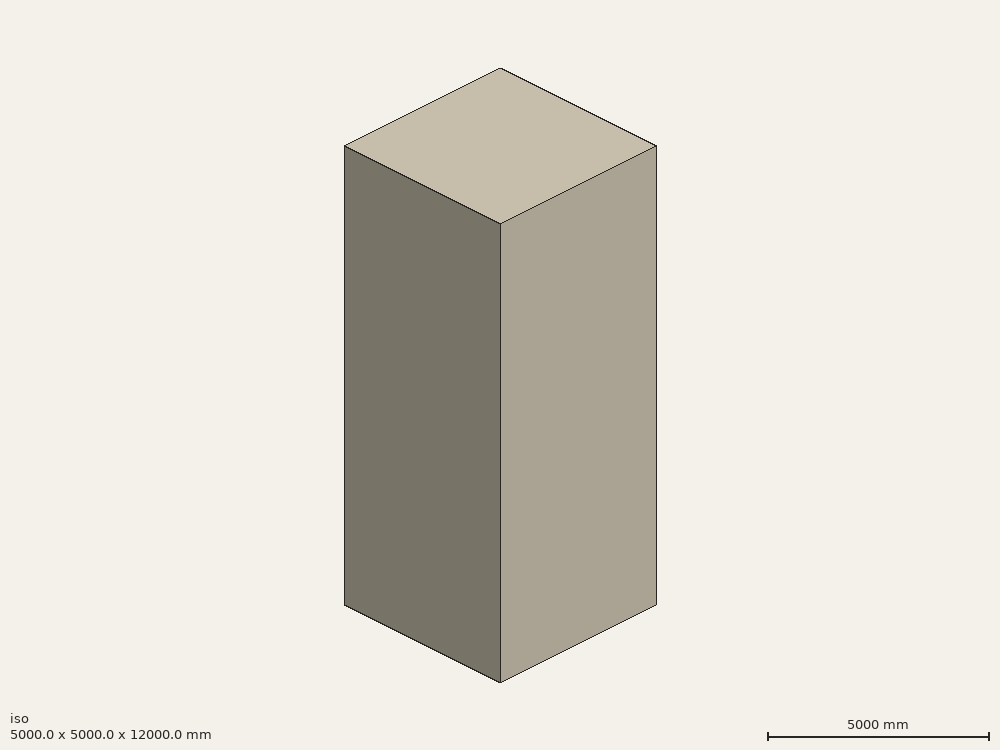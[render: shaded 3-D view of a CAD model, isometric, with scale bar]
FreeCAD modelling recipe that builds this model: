
FCSTD DOCUMENT  (FreeCAD 1.0R39109 (Git))
Label: revolveTester-6
License: All rights reserved
LicenseURL: http://en.wikipedia.org/wiki/All_rights_reserved
objects: App::DocumentObjectGroupPython×1248, App::Part×2, Part::FeaturePython×1, Sketcher::SketchObject×1, Part::Revolution×1, Part::Cylinder×1, Part::Cut×1
note: 6 computed .brp shape members not serialized (recipe doc carries the construction recipe); baked Part::Feature solids carry a one-line shape summary decoded from their .brp

FEATURE [App::DocumentObjectGroupPython] HALFPI  # scripted group (container) (typed FeaturePython)
  name = HALFPI
  value = pi/2.
FEATURE [App::DocumentObjectGroupPython] PI  # scripted group (container) (typed FeaturePython)
  name = PI
  value = 1.*pi
FEATURE [App::DocumentObjectGroupPython] TWOPI  # scripted group (container) (typed FeaturePython)
  name = TWOPI
  value = 2.*pi
FEATURE [App::DocumentObjectGroupPython] Constants  # scripted group (container) (typed FeaturePython)
  Group = -> [HALFPI,PI,TWOPI]
FEATURE [App::DocumentObjectGroupPython] Variables  # scripted group (container) (typed FeaturePython)
FEATURE [App::DocumentObjectGroupPython] Quantities  # scripted group (container) (typed FeaturePython)
FEATURE [App::DocumentObjectGroupPython] Isotopes  # scripted group (container) (typed FeaturePython)
FEATURE [App::DocumentObjectGroupPython] Elements  # scripted group (container) (typed FeaturePython)
FEATURE [App::DocumentObjectGroupPython] G4Isotopes  # scripted group (container) (typed FeaturePython)
FEATURE [App::DocumentObjectGroupPython] H_element  # scripted group (container) (typed FeaturePython)
  Z = 1
  atom_value = 1.008
  formula = H
  name = H_element
FEATURE [App::DocumentObjectGroupPython] He_element  # scripted group (container) (typed FeaturePython)
  Z = 2
  atom_value = 4.0026
  formula = He
  name = He_element
FEATURE [App::DocumentObjectGroupPython] Li_element  # scripted group (container) (typed FeaturePython)
  Z = 3
  atom_value = 6.94
  formula = Li
  name = Li_element
FEATURE [App::DocumentObjectGroupPython] Be_element  # scripted group (container) (typed FeaturePython)
  Z = 4
  atom_value = 9.01218
  formula = Be
  name = Be_element
FEATURE [App::DocumentObjectGroupPython] B_element  # scripted group (container) (typed FeaturePython)
  Z = 5
  atom_value = 10.81
  formula = B
  name = B_element
FEATURE [App::DocumentObjectGroupPython] C_element  # scripted group (container) (typed FeaturePython)
  Z = 6
  atom_value = 12.011
  formula = C
  name = C_element
FEATURE [App::DocumentObjectGroupPython] N_element  # scripted group (container) (typed FeaturePython)
  Z = 7
  atom_value = 14.007
  formula = N
  name = N_element
FEATURE [App::DocumentObjectGroupPython] O_element  # scripted group (container) (typed FeaturePython)
  Z = 8
  atom_value = 15.999
  formula = O
  name = O_element
FEATURE [App::DocumentObjectGroupPython] F_element  # scripted group (container) (typed FeaturePython)
  Z = 9
  atom_value = 18.9984
  formula = F
  name = F_element
FEATURE [App::DocumentObjectGroupPython] Ne_element  # scripted group (container) (typed FeaturePython)
  Z = 10
  atom_value = 20.1797
  formula = Ne
  name = Ne_element
FEATURE [App::DocumentObjectGroupPython] Na_element  # scripted group (container) (typed FeaturePython)
  Z = 11
  atom_value = 22.9898
  formula = Na
  name = Na_element
FEATURE [App::DocumentObjectGroupPython] Mg_element  # scripted group (container) (typed FeaturePython)
  Z = 12
  atom_value = 24.305
  formula = Mg
  name = Mg_element
FEATURE [App::DocumentObjectGroupPython] Al_element  # scripted group (container) (typed FeaturePython)
  Z = 13
  atom_value = 26.9815
  formula = Al
  name = Al_element
FEATURE [App::DocumentObjectGroupPython] Si_element  # scripted group (container) (typed FeaturePython)
  Z = 14
  atom_value = 28.085
  formula = Si
  name = Si_element
FEATURE [App::DocumentObjectGroupPython] P_element  # scripted group (container) (typed FeaturePython)
  Z = 15
  atom_value = 30.9738
  formula = P
  name = P_element
FEATURE [App::DocumentObjectGroupPython] S_element  # scripted group (container) (typed FeaturePython)
  Z = 16
  atom_value = 32.06
  formula = S
  name = S_element
FEATURE [App::DocumentObjectGroupPython] Cl_element  # scripted group (container) (typed FeaturePython)
  Z = 17
  atom_value = 35.45
  formula = Cl
  name = Cl_element
FEATURE [App::DocumentObjectGroupPython] Ar_element  # scripted group (container) (typed FeaturePython)
  Z = 18
  atom_value = 39.95
  formula = Ar
  name = Ar_element
FEATURE [App::DocumentObjectGroupPython] K_element  # scripted group (container) (typed FeaturePython)
  Z = 19
  atom_value = 39.0983
  formula = K
  name = K_element
FEATURE [App::DocumentObjectGroupPython] Ca_element  # scripted group (container) (typed FeaturePython)
  Z = 20
  atom_value = 40.078
  formula = Ca
  name = Ca_element
FEATURE [App::DocumentObjectGroupPython] Sc_element  # scripted group (container) (typed FeaturePython)
  Z = 21
  atom_value = 44.9559
  formula = Sc
  name = Sc_element
FEATURE [App::DocumentObjectGroupPython] Ti_element  # scripted group (container) (typed FeaturePython)
  Z = 22
  atom_value = 47.867
  formula = Ti
  name = Ti_element
FEATURE [App::DocumentObjectGroupPython] V_element  # scripted group (container) (typed FeaturePython)
  Z = 23
  atom_value = 50.9415
  formula = V
  name = V_element
FEATURE [App::DocumentObjectGroupPython] Cr_element  # scripted group (container) (typed FeaturePython)
  Z = 24
  atom_value = 51.9961
  formula = Cr
  name = Cr_element
FEATURE [App::DocumentObjectGroupPython] Mn_element  # scripted group (container) (typed FeaturePython)
  Z = 25
  atom_value = 54.938
  formula = Mn
  name = Mn_element
FEATURE [App::DocumentObjectGroupPython] Fe_element  # scripted group (container) (typed FeaturePython)
  Z = 26
  atom_value = 55.845
  formula = Fe
  name = Fe_element
FEATURE [App::DocumentObjectGroupPython] Co_element  # scripted group (container) (typed FeaturePython)
  Z = 27
  atom_value = 58.9332
  formula = Co
  name = Co_element
FEATURE [App::DocumentObjectGroupPython] Ni_element  # scripted group (container) (typed FeaturePython)
  Z = 28
  atom_value = 58.6934
  formula = Ni
  name = Ni_element
FEATURE [App::DocumentObjectGroupPython] Cu_element  # scripted group (container) (typed FeaturePython)
  Z = 29
  atom_value = 63.546
  formula = Cu
  name = Cu_element
FEATURE [App::DocumentObjectGroupPython] Zn_element  # scripted group (container) (typed FeaturePython)
  Z = 30
  atom_value = 65.38
  formula = Zn
  name = Zn_element
FEATURE [App::DocumentObjectGroupPython] Ga_element  # scripted group (container) (typed FeaturePython)
  Z = 31
  atom_value = 69.723
  formula = Ga
  name = Ga_element
FEATURE [App::DocumentObjectGroupPython] Ge_element  # scripted group (container) (typed FeaturePython)
  Z = 32
  atom_value = 72.63
  formula = Ge
  name = Ge_element
FEATURE [App::DocumentObjectGroupPython] As_element  # scripted group (container) (typed FeaturePython)
  Z = 33
  atom_value = 74.9216
  formula = As
  name = As_element
FEATURE [App::DocumentObjectGroupPython] Se_element  # scripted group (container) (typed FeaturePython)
  Z = 34
  atom_value = 78.971
  formula = Se
  name = Se_element
FEATURE [App::DocumentObjectGroupPython] Br_element  # scripted group (container) (typed FeaturePython)
  Z = 35
  atom_value = 79.904
  formula = Br
  name = Br_element
FEATURE [App::DocumentObjectGroupPython] Kr_element  # scripted group (container) (typed FeaturePython)
  Z = 36
  atom_value = 83.798
  formula = Kr
  name = Kr_element
FEATURE [App::DocumentObjectGroupPython] Rb_element  # scripted group (container) (typed FeaturePython)
  Z = 37
  atom_value = 85.4678
  formula = Rb
  name = Rb_element
FEATURE [App::DocumentObjectGroupPython] Sr_element  # scripted group (container) (typed FeaturePython)
  Z = 38
  atom_value = 87.62
  formula = Sr
  name = Sr_element
FEATURE [App::DocumentObjectGroupPython] Y_element  # scripted group (container) (typed FeaturePython)
  Z = 39
  atom_value = 88.9058
  formula = Y
  name = Y_element
FEATURE [App::DocumentObjectGroupPython] Zr_element  # scripted group (container) (typed FeaturePython)
  Z = 40
  atom_value = 91.224
  formula = Zr
  name = Zr_element
FEATURE [App::DocumentObjectGroupPython] Nb_element  # scripted group (container) (typed FeaturePython)
  Z = 41
  atom_value = 92.9064
  formula = Nb
  name = Nb_element
FEATURE [App::DocumentObjectGroupPython] Mo_element  # scripted group (container) (typed FeaturePython)
  Z = 42
  atom_value = 95.95
  formula = Mo
  name = Mo_element
FEATURE [App::DocumentObjectGroupPython] Tc_element  # scripted group (container) (typed FeaturePython)
  Z = 43
  atom_value = 97
  formula = Tc
  name = Tc_element
FEATURE [App::DocumentObjectGroupPython] Ru_element  # scripted group (container) (typed FeaturePython)
  Z = 44
  atom_value = 101.07
  formula = Ru
  name = Ru_element
FEATURE [App::DocumentObjectGroupPython] Rh_element  # scripted group (container) (typed FeaturePython)
  Z = 45
  atom_value = 102.905
  formula = Rh
  name = Rh_element
FEATURE [App::DocumentObjectGroupPython] Pd_element  # scripted group (container) (typed FeaturePython)
  Z = 46
  atom_value = 106.42
  formula = Pd
  name = Pd_element
FEATURE [App::DocumentObjectGroupPython] Ag_element  # scripted group (container) (typed FeaturePython)
  Z = 47
  atom_value = 107.868
  formula = Ag
  name = Ag_element
FEATURE [App::DocumentObjectGroupPython] Cd_element  # scripted group (container) (typed FeaturePython)
  Z = 48
  atom_value = 112.414
  formula = Cd
  name = Cd_element
FEATURE [App::DocumentObjectGroupPython] In_element  # scripted group (container) (typed FeaturePython)
  Z = 49
  atom_value = 114.818
  formula = In
  name = In_element
FEATURE [App::DocumentObjectGroupPython] Sn_element  # scripted group (container) (typed FeaturePython)
  Z = 50
  atom_value = 118.71
  formula = Sn
  name = Sn_element
FEATURE [App::DocumentObjectGroupPython] Sb_element  # scripted group (container) (typed FeaturePython)
  Z = 51
  atom_value = 121.76
  formula = Sb
  name = Sb_element
FEATURE [App::DocumentObjectGroupPython] Te_element  # scripted group (container) (typed FeaturePython)
  Z = 52
  atom_value = 127.6
  formula = Te
  name = Te_element
FEATURE [App::DocumentObjectGroupPython] I_element  # scripted group (container) (typed FeaturePython)
  Z = 53
  atom_value = 126.904
  formula = I
  name = I_element
FEATURE [App::DocumentObjectGroupPython] Xe_element  # scripted group (container) (typed FeaturePython)
  Z = 54
  atom_value = 131.293
  formula = Xe
  name = Xe_element
FEATURE [App::DocumentObjectGroupPython] Cs_element  # scripted group (container) (typed FeaturePython)
  Z = 55
  atom_value = 132.905
  formula = Cs
  name = Cs_element
FEATURE [App::DocumentObjectGroupPython] Ba_element  # scripted group (container) (typed FeaturePython)
  Z = 56
  atom_value = 137.327
  formula = Ba
  name = Ba_element
FEATURE [App::DocumentObjectGroupPython] La_element  # scripted group (container) (typed FeaturePython)
  Z = 57
  atom_value = 138.905
  formula = La
  name = La_element
FEATURE [App::DocumentObjectGroupPython] Ce_element  # scripted group (container) (typed FeaturePython)
  Z = 58
  atom_value = 140.116
  formula = Ce
  name = Ce_element
FEATURE [App::DocumentObjectGroupPython] Pr_element  # scripted group (container) (typed FeaturePython)
  Z = 59
  atom_value = 140.908
  formula = Pr
  name = Pr_element
FEATURE [App::DocumentObjectGroupPython] Nd_element  # scripted group (container) (typed FeaturePython)
  Z = 60
  atom_value = 144.242
  formula = Nd
  name = Nd_element
FEATURE [App::DocumentObjectGroupPython] Pm_element  # scripted group (container) (typed FeaturePython)
  Z = 61
  atom_value = 145
  formula = Pm
  name = Pm_element
FEATURE [App::DocumentObjectGroupPython] Sm_element  # scripted group (container) (typed FeaturePython)
  Z = 62
  atom_value = 150.36
  formula = Sm
  name = Sm_element
FEATURE [App::DocumentObjectGroupPython] Eu_element  # scripted group (container) (typed FeaturePython)
  Z = 63
  atom_value = 151.964
  formula = Eu
  name = Eu_element
FEATURE [App::DocumentObjectGroupPython] Gd_element  # scripted group (container) (typed FeaturePython)
  Z = 64
  atom_value = 157.25
  formula = Gd
  name = Gd_element
FEATURE [App::DocumentObjectGroupPython] Tb_element  # scripted group (container) (typed FeaturePython)
  Z = 65
  atom_value = 158.925
  formula = Tb
  name = Tb_element
FEATURE [App::DocumentObjectGroupPython] Dy_element  # scripted group (container) (typed FeaturePython)
  Z = 66
  atom_value = 162.5
  formula = Dy
  name = Dy_element
FEATURE [App::DocumentObjectGroupPython] Ho_element  # scripted group (container) (typed FeaturePython)
  Z = 67
  atom_value = 164.93
  formula = Ho
  name = Ho_element
FEATURE [App::DocumentObjectGroupPython] Er_element  # scripted group (container) (typed FeaturePython)
  Z = 68
  atom_value = 167.259
  formula = Er
  name = Er_element
FEATURE [App::DocumentObjectGroupPython] Tm_element  # scripted group (container) (typed FeaturePython)
  Z = 69
  atom_value = 168.934
  formula = Tm
  name = Tm_element
FEATURE [App::DocumentObjectGroupPython] Yb_element  # scripted group (container) (typed FeaturePython)
  Z = 70
  atom_value = 173.045
  formula = Yb
  name = Yb_element
FEATURE [App::DocumentObjectGroupPython] Lu_element  # scripted group (container) (typed FeaturePython)
  Z = 71
  atom_value = 174.967
  formula = Lu
  name = Lu_element
FEATURE [App::DocumentObjectGroupPython] Hf_element  # scripted group (container) (typed FeaturePython)
  Z = 72
  atom_value = 178.49
  formula = Hf
  name = Hf_element
FEATURE [App::DocumentObjectGroupPython] Ta_element  # scripted group (container) (typed FeaturePython)
  Z = 73
  atom_value = 180.948
  formula = Ta
  name = Ta_element
FEATURE [App::DocumentObjectGroupPython] W_element  # scripted group (container) (typed FeaturePython)
  Z = 74
  atom_value = 183.84
  formula = W
  name = W_element
FEATURE [App::DocumentObjectGroupPython] Re_element  # scripted group (container) (typed FeaturePython)
  Z = 75
  atom_value = 186.207
  formula = Re
  name = Re_element
FEATURE [App::DocumentObjectGroupPython] Os_element  # scripted group (container) (typed FeaturePython)
  Z = 76
  atom_value = 190.23
  formula = Os
  name = Os_element
FEATURE [App::DocumentObjectGroupPython] Ir_element  # scripted group (container) (typed FeaturePython)
  Z = 77
  atom_value = 192.217
  formula = Ir
  name = Ir_element
FEATURE [App::DocumentObjectGroupPython] Pt_element  # scripted group (container) (typed FeaturePython)
  Z = 78
  atom_value = 195.084
  formula = Pt
  name = Pt_element
FEATURE [App::DocumentObjectGroupPython] Au_element  # scripted group (container) (typed FeaturePython)
  Z = 79
  atom_value = 196.967
  formula = Au
  name = Au_element
FEATURE [App::DocumentObjectGroupPython] Hg_element  # scripted group (container) (typed FeaturePython)
  Z = 80
  atom_value = 200.592
  formula = Hg
  name = Hg_element
FEATURE [App::DocumentObjectGroupPython] Tl_element  # scripted group (container) (typed FeaturePython)
  Z = 81
  atom_value = 204.38
  formula = Tl
  name = Tl_element
FEATURE [App::DocumentObjectGroupPython] Pb_element  # scripted group (container) (typed FeaturePython)
  Z = 82
  atom_value = 207.2
  formula = Pb
  name = Pb_element
FEATURE [App::DocumentObjectGroupPython] Bi_element  # scripted group (container) (typed FeaturePython)
  Z = 83
  atom_value = 208.98
  formula = Bi
  name = Bi_element
FEATURE [App::DocumentObjectGroupPython] Po_element  # scripted group (container) (typed FeaturePython)
  Z = 84
  atom_value = 209
  formula = Po
  name = Po_element
FEATURE [App::DocumentObjectGroupPython] At_element  # scripted group (container) (typed FeaturePython)
  Z = 85
  atom_value = 210
  formula = At
  name = At_element
FEATURE [App::DocumentObjectGroupPython] Rn_element  # scripted group (container) (typed FeaturePython)
  Z = 86
  atom_value = 222
  formula = Rn
  name = Rn_element
FEATURE [App::DocumentObjectGroupPython] Fr_element  # scripted group (container) (typed FeaturePython)
  Z = 87
  atom_value = 223
  formula = Fr
  name = Fr_element
FEATURE [App::DocumentObjectGroupPython] Ra_element  # scripted group (container) (typed FeaturePython)
  Z = 88
  atom_value = 226
  formula = Ra
  name = Ra_element
FEATURE [App::DocumentObjectGroupPython] Ac_element  # scripted group (container) (typed FeaturePython)
  Z = 89
  atom_value = 227
  formula = Ac
  name = Ac_element
FEATURE [App::DocumentObjectGroupPython] Th_element  # scripted group (container) (typed FeaturePython)
  Z = 90
  atom_value = 232.038
  formula = Th
  name = Th_element
FEATURE [App::DocumentObjectGroupPython] Pa_element  # scripted group (container) (typed FeaturePython)
  Z = 91
  atom_value = 231.036
  formula = Pa
  name = Pa_element
FEATURE [App::DocumentObjectGroupPython] U_element  # scripted group (container) (typed FeaturePython)
  Z = 92
  atom_value = 238.029
  formula = U
  name = U_element
FEATURE [App::DocumentObjectGroupPython] Np_element  # scripted group (container) (typed FeaturePython)
  Z = 93
  atom_value = 237
  formula = Np
  name = Np_element
FEATURE [App::DocumentObjectGroupPython] Pu_element  # scripted group (container) (typed FeaturePython)
  Z = 94
  atom_value = 244
  formula = Pu
  name = Pu_element
FEATURE [App::DocumentObjectGroupPython] Am_element  # scripted group (container) (typed FeaturePython)
  Z = 95
  atom_value = 243
  formula = Am
  name = Am_element
FEATURE [App::DocumentObjectGroupPython] Cm_element  # scripted group (container) (typed FeaturePython)
  Z = 96
  atom_value = 247
  formula = Cm
  name = Cm_element
FEATURE [App::DocumentObjectGroupPython] Bk_element  # scripted group (container) (typed FeaturePython)
  Z = 97
  atom_value = 247
  formula = Bk
  name = Bk_element
FEATURE [App::DocumentObjectGroupPython] Cf_element  # scripted group (container) (typed FeaturePython)
  Z = 98
  atom_value = 251
  formula = Cf
  name = Cf_element
FEATURE [App::DocumentObjectGroupPython] G4Elements  # scripted group (container) (typed FeaturePython)
  Group = -> [H_element,He_element,Li_element,Be_element,B_element,C_element,N_element,O_element,F_element,Ne_element,Na_element,Mg_element,Al_element,Si_element,P_element,S_element,Cl_element,Ar_element,K_element,Ca_element,Sc_element,Ti_element,V_element,Cr_element,Mn_element,Fe_element,Co_element,Ni_element,Cu_element,Zn_element,Ga_element,Ge_element,As_element,Se_element,Br_element,Kr_element,Rb_element,+61 more]
FEATURE [App::DocumentObjectGroupPython] H_element001  label="H_element : 0.101"  # scripted group (container) (typed FeaturePython)
  n = 0.101327
FEATURE [App::DocumentObjectGroupPython] C_element001  label="C_element : 0.775"  # scripted group (container) (typed FeaturePython)
  n = 0.7755
FEATURE [App::DocumentObjectGroupPython] N_element001  label="N_element : 0.035"  # scripted group (container) (typed FeaturePython)
  n = 0.035057
FEATURE [App::DocumentObjectGroupPython] O_element001  label="O_element : 0.052"  # scripted group (container) (typed FeaturePython)
  n = 0.0523159
FEATURE [App::DocumentObjectGroupPython] F_element001  label="F_element : 0.017"  # scripted group (container) (typed FeaturePython)
  n = 0.017422
FEATURE [App::DocumentObjectGroupPython] Ca_element001  label="Ca_element : 0.018"  # scripted group (container) (typed FeaturePython)
  n = 0.018378
FEATURE [App::DocumentObjectGroupPython] G4_A_150_TISSUE  label="G4_A-150_TISSUE"  # scripted group (container) (typed FeaturePython)
  Dunit = g/cm3
  Dvalue = 1.127
  Group = -> [H_element001,C_element001,N_element001,O_element001,F_element001,Ca_element001]
  conduct = 2
  density = 1
  expand = 3
  formula = G4_A-150_TISSUE
  name = G4_A-150_TISSUE
  specific = 4
FEATURE [App::DocumentObjectGroupPython] C_element002  label="C_element : 3"  # scripted group (container) (typed FeaturePython)
  n = 3
  ref = C_element
FEATURE [App::DocumentObjectGroupPython] H_element002  label="H_element : 6"  # scripted group (container) (typed FeaturePython)
  n = 6
  ref = H_element
FEATURE [App::DocumentObjectGroupPython] O_element002  label="O_element : 1"  # scripted group (container) (typed FeaturePython)
  n = 1
  ref = O_element
FEATURE [App::DocumentObjectGroupPython] G4_ACETONE  # scripted group (container) (typed FeaturePython)
  Dunit = g/cm3
  Dvalue = 0.7899
  Group = -> [C_element002,H_element002,O_element002]
  conduct = 2
  density = 1
  expand = 3
  formula = G4_ACETONE
  name = G4_ACETONE
  specific = 4
FEATURE [App::DocumentObjectGroupPython] C_element003  label="C_element : 2"  # scripted group (container) (typed FeaturePython)
  n = 2
  ref = C_element
FEATURE [App::DocumentObjectGroupPython] H_element003  label="H_element : 2"  # scripted group (container) (typed FeaturePython)
  n = 2
  ref = H_element
FEATURE [App::DocumentObjectGroupPython] G4_ACETYLENE  # scripted group (container) (typed FeaturePython)
  Dunit = g/cm3
  Dvalue = 0.0010967
  Group = -> [C_element003,H_element003]
  conduct = 2
  density = 1
  expand = 3
  formula = G4_ACETYLENE
  name = G4_ACETYLENE
  specific = 4
FEATURE [App::DocumentObjectGroupPython] C_element004  label="C_element : 5"  # scripted group (container) (typed FeaturePython)
  n = 5
  ref = C_element
FEATURE [App::DocumentObjectGroupPython] H_element004  label="H_element : 5"  # scripted group (container) (typed FeaturePython)
  n = 5
  ref = H_element
FEATURE [App::DocumentObjectGroupPython] N_element002  label="N_element : 5"  # scripted group (container) (typed FeaturePython)
  n = 5
  ref = N_element
FEATURE [App::DocumentObjectGroupPython] G4_ADENINE  # scripted group (container) (typed FeaturePython)
  Dunit = g/cm3
  Dvalue = 1.6
  Group = -> [C_element004,H_element004,N_element002]
  conduct = 2
  density = 1
  expand = 3
  formula = G4_ADENINE
  name = G4_ADENINE
  specific = 4
FEATURE [App::DocumentObjectGroupPython] H_element005  label="H_element : 0.114"  # scripted group (container) (typed FeaturePython)
  n = 0.114
FEATURE [App::DocumentObjectGroupPython] C_element005  label="C_element : 0.598"  # scripted group (container) (typed FeaturePython)
  n = 0.598
FEATURE [App::DocumentObjectGroupPython] N_element003  label="N_element : 0.007"  # scripted group (container) (typed FeaturePython)
  n = 0.007
FEATURE [App::DocumentObjectGroupPython] O_element003  label="O_element : 0.278"  # scripted group (container) (typed FeaturePython)
  n = 0.278
FEATURE [App::DocumentObjectGroupPython] Na_element001  label="Na_element : 0.001"  # scripted group (container) (typed FeaturePython)
  n = 0.001
FEATURE [App::DocumentObjectGroupPython] S_element001  label="S_element : 0.001"  # scripted group (container) (typed FeaturePython)
  n = 0.001
FEATURE [App::DocumentObjectGroupPython] Cl_element001  label="Cl_element : 0.001"  # scripted group (container) (typed FeaturePython)
  n = 0.001
FEATURE [App::DocumentObjectGroupPython] G4_ADIPOSE_TISSUE_ICRP  # scripted group (container) (typed FeaturePython)
  Dunit = g/cm3
  Dvalue = 0.95
  Group = -> [H_element005,C_element005,N_element003,O_element003,Na_element001,S_element001,Cl_element001]
  conduct = 2
  density = 1
  expand = 3
  formula = G4_ADIPOSE_TISSUE_ICRP
  name = G4_ADIPOSE_TISSUE_ICRP
  specific = 4
FEATURE [App::DocumentObjectGroupPython] C_element006  label="C_element : 0.000"  # scripted group (container) (typed FeaturePython)
  n = 0.000124
FEATURE [App::DocumentObjectGroupPython] N_element004  label="N_element : 0.755"  # scripted group (container) (typed FeaturePython)
  n = 0.755268
FEATURE [App::DocumentObjectGroupPython] O_element004  label="O_element : 0.232"  # scripted group (container) (typed FeaturePython)
  n = 0.231781
FEATURE [App::DocumentObjectGroupPython] Ar_element001  label="Ar_element : 0.013"  # scripted group (container) (typed FeaturePython)
  n = 0.012827
FEATURE [App::DocumentObjectGroupPython] G4_AIR  # scripted group (container) (typed FeaturePython)
  Dunit = g/cm3
  Dvalue = 0.00120479
  Group = -> [C_element006,N_element004,O_element004,Ar_element001]
  conduct = 2
  density = 1
  expand = 3
  formula = G4_AIR
  name = G4_AIR
  specific = 4
FEATURE [App::DocumentObjectGroupPython] C_element007  label="C_element : 006"  # scripted group (container) (typed FeaturePython)
  n = 3
  ref = C_element
FEATURE [App::DocumentObjectGroupPython] H_element006  label="H_element : 7"  # scripted group (container) (typed FeaturePython)
  n = 7
  ref = H_element
FEATURE [App::DocumentObjectGroupPython] N_element005  label="N_element : 1"  # scripted group (container) (typed FeaturePython)
  n = 1
  ref = N_element
FEATURE [App::DocumentObjectGroupPython] O_element005  label="O_element : 2"  # scripted group (container) (typed FeaturePython)
  n = 2
  ref = O_element
FEATURE [App::DocumentObjectGroupPython] G4_ALANINE  # scripted group (container) (typed FeaturePython)
  Dunit = g/cm3
  Dvalue = 1.42
  Group = -> [C_element007,H_element006,N_element005,O_element005]
  conduct = 2
  density = 1
  expand = 3
  formula = G4_ALANINE
  name = G4_ALANINE
  specific = 4
FEATURE [App::DocumentObjectGroupPython] Al_element001  label="Al_element : 2"  # scripted group (container) (typed FeaturePython)
  n = 2
  ref = Al_element
FEATURE [App::DocumentObjectGroupPython] O_element006  label="O_element : 3"  # scripted group (container) (typed FeaturePython)
  n = 3
  ref = O_element
FEATURE [App::DocumentObjectGroupPython] G4_ALUMINUM_OXIDE  # scripted group (container) (typed FeaturePython)
  Dunit = g/cm3
  Dvalue = 3.97
  Group = -> [Al_element001,O_element006]
  conduct = 2
  density = 1
  expand = 3
  formula = G4_ALUMINUM_OXIDE
  name = G4_ALUMINUM_OXIDE
  specific = 4
FEATURE [App::DocumentObjectGroupPython] H_element007  label="H_element : 0.106"  # scripted group (container) (typed FeaturePython)
  n = 0.10593
FEATURE [App::DocumentObjectGroupPython] C_element008  label="C_element : 0.789"  # scripted group (container) (typed FeaturePython)
  n = 0.788974
FEATURE [App::DocumentObjectGroupPython] O_element007  label="O_element : 0.105"  # scripted group (container) (typed FeaturePython)
  n = 0.105096
FEATURE [App::DocumentObjectGroupPython] G4_AMBER  # scripted group (container) (typed FeaturePython)
  Dunit = g/cm3
  Dvalue = 1.1
  Group = -> [H_element007,C_element008,O_element007]
  conduct = 2
  density = 1
  expand = 3
  formula = G4_AMBER
  name = G4_AMBER
  specific = 4
FEATURE [App::DocumentObjectGroupPython] N_element006  label="N_element : 006"  # scripted group (container) (typed FeaturePython)
  n = 1
  ref = N_element
FEATURE [App::DocumentObjectGroupPython] H_element008  label="H_element : 3"  # scripted group (container) (typed FeaturePython)
  n = 3
  ref = H_element
FEATURE [App::DocumentObjectGroupPython] G4_AMMONIA  # scripted group (container) (typed FeaturePython)
  Dunit = g/cm3
  Dvalue = 0.000826019
  Group = -> [N_element006,H_element008]
  conduct = 2
  density = 1
  expand = 3
  formula = G4_AMMONIA
  name = G4_AMMONIA
  specific = 4
FEATURE [App::DocumentObjectGroupPython] C_element009  label="C_element : 6"  # scripted group (container) (typed FeaturePython)
  n = 6
  ref = C_element
FEATURE [App::DocumentObjectGroupPython] H_element009  label="H_element : 008"  # scripted group (container) (typed FeaturePython)
  n = 7
  ref = H_element
FEATURE [App::DocumentObjectGroupPython] N_element007  label="N_element : 007"  # scripted group (container) (typed FeaturePython)
  n = 1
  ref = N_element
FEATURE [App::DocumentObjectGroupPython] G4_ANILINE  # scripted group (container) (typed FeaturePython)
  Dunit = g/cm3
  Dvalue = 1.0235
  Group = -> [C_element009,H_element009,N_element007]
  conduct = 2
  density = 1
  expand = 3
  formula = G4_ANILINE
  name = G4_ANILINE
  specific = 4
FEATURE [App::DocumentObjectGroupPython] C_element010  label="C_element : 14"  # scripted group (container) (typed FeaturePython)
  n = 14
  ref = C_element
FEATURE [App::DocumentObjectGroupPython] H_element010  label="H_element : 10"  # scripted group (container) (typed FeaturePython)
  n = 10
  ref = H_element
FEATURE [App::DocumentObjectGroupPython] G4_ANTHRACENE  # scripted group (container) (typed FeaturePython)
  Dunit = g/cm3
  Dvalue = 1.283
  Group = -> [C_element010,H_element010]
  conduct = 2
  density = 1
  expand = 3
  formula = G4_ANTHRACENE
  name = G4_ANTHRACENE
  specific = 4
FEATURE [App::DocumentObjectGroupPython] H_element011  label="H_element : 0.065"  # scripted group (container) (typed FeaturePython)
  n = 0.0654709
FEATURE [App::DocumentObjectGroupPython] C_element011  label="C_element : 0.537"  # scripted group (container) (typed FeaturePython)
  n = 0.536944
FEATURE [App::DocumentObjectGroupPython] N_element008  label="N_element : 0.021"  # scripted group (container) (typed FeaturePython)
  n = 0.0215
FEATURE [App::DocumentObjectGroupPython] O_element008  label="O_element : 0.032"  # scripted group (container) (typed FeaturePython)
  n = 0.032085
FEATURE [App::DocumentObjectGroupPython] F_element002  label="F_element : 0.167"  # scripted group (container) (typed FeaturePython)
  n = 0.167411
FEATURE [App::DocumentObjectGroupPython] Ca_element002  label="Ca_element : 0.177"  # scripted group (container) (typed FeaturePython)
  n = 0.176589
FEATURE [App::DocumentObjectGroupPython] G4_B_100_BONE  label="G4_B-100_BONE"  # scripted group (container) (typed FeaturePython)
  Dunit = g/cm3
  Dvalue = 1.45
  Group = -> [H_element011,C_element011,N_element008,O_element008,F_element002,Ca_element002]
  conduct = 2
  density = 1
  expand = 3
  formula = G4_B-100_BONE
  name = G4_B-100_BONE
  specific = 4
FEATURE [App::DocumentObjectGroupPython] H_element012  label="H_element : 0.057"  # scripted group (container) (typed FeaturePython)
  n = 0.057441
FEATURE [App::DocumentObjectGroupPython] C_element012  label="C_element : 0.790"  # scripted group (container) (typed FeaturePython)
  n = 0.774591
FEATURE [App::DocumentObjectGroupPython] O_element009  label="O_element : 0.168"  # scripted group (container) (typed FeaturePython)
  n = 0.167968
FEATURE [App::DocumentObjectGroupPython] G4_BAKELITE  # scripted group (container) (typed FeaturePython)
  Dunit = g/cm3
  Dvalue = 1.25
  Group = -> [H_element012,C_element012,O_element009]
  conduct = 2
  density = 1
  expand = 3
  formula = G4_BAKELITE
  name = G4_BAKELITE
  specific = 4
FEATURE [App::DocumentObjectGroupPython] Ba_element001  label="Ba_element : 1"  # scripted group (container) (typed FeaturePython)
  n = 1
  ref = Ba_element
FEATURE [App::DocumentObjectGroupPython] F_element003  label="F_element : 2"  # scripted group (container) (typed FeaturePython)
  n = 2
  ref = F_element
FEATURE [App::DocumentObjectGroupPython] G4_BARIUM_FLUORIDE  # scripted group (container) (typed FeaturePython)
  Dunit = g/cm3
  Dvalue = 4.89
  Group = -> [Ba_element001,F_element003]
  conduct = 2
  density = 1
  expand = 3
  formula = G4_BARIUM_FLUORIDE
  name = G4_BARIUM_FLUORIDE
  specific = 4
FEATURE [App::DocumentObjectGroupPython] Ba_element002  label="Ba_element : 002"  # scripted group (container) (typed FeaturePython)
  n = 1
  ref = Ba_element
FEATURE [App::DocumentObjectGroupPython] S_element002  label="S_element : 1"  # scripted group (container) (typed FeaturePython)
  n = 1
  ref = S_element
FEATURE [App::DocumentObjectGroupPython] O_element010  label="O_element : 4"  # scripted group (container) (typed FeaturePython)
  n = 4
  ref = O_element
FEATURE [App::DocumentObjectGroupPython] G4_BARIUM_SULFATE  # scripted group (container) (typed FeaturePython)
  Dunit = g/cm3
  Dvalue = 4.5
  Group = -> [Ba_element002,S_element002,O_element010]
  conduct = 2
  density = 1
  expand = 3
  formula = G4_BARIUM_SULFATE
  name = G4_BARIUM_SULFATE
  specific = 4
FEATURE [App::DocumentObjectGroupPython] C_element013  label="C_element : 007"  # scripted group (container) (typed FeaturePython)
  n = 6
  ref = C_element
FEATURE [App::DocumentObjectGroupPython] H_element013  label="H_element : 009"  # scripted group (container) (typed FeaturePython)
  n = 6
  ref = H_element
FEATURE [App::DocumentObjectGroupPython] G4_BENZENE  # scripted group (container) (typed FeaturePython)
  Dunit = g/cm3
  Dvalue = 0.87865
  Group = -> [C_element013,H_element013]
  conduct = 2
  density = 1
  expand = 3
  formula = G4_BENZENE
  name = G4_BENZENE
  specific = 4
FEATURE [App::DocumentObjectGroupPython] Be_element001  label="Be_element : 1"  # scripted group (container) (typed FeaturePython)
  n = 1
  ref = Be_element
FEATURE [App::DocumentObjectGroupPython] O_element011  label="O_element : 005"  # scripted group (container) (typed FeaturePython)
  n = 1
  ref = O_element
FEATURE [App::DocumentObjectGroupPython] G4_BERYLLIUM_OXIDE  # scripted group (container) (typed FeaturePython)
  Dunit = g/cm3
  Dvalue = 3.01
  Group = -> [Be_element001,O_element011]
  conduct = 2
  density = 1
  expand = 3
  formula = G4_BERYLLIUM_OXIDE
  name = G4_BERYLLIUM_OXIDE
  specific = 4
FEATURE [App::DocumentObjectGroupPython] Bi_element001  label="Bi_element : 4"  # scripted group (container) (typed FeaturePython)
  n = 4
  ref = Bi_element
FEATURE [App::DocumentObjectGroupPython] Ge_element001  label="Ge_element : 3"  # scripted group (container) (typed FeaturePython)
  n = 3
  ref = Ge_element
FEATURE [App::DocumentObjectGroupPython] O_element012  label="O_element : 12"  # scripted group (container) (typed FeaturePython)
  n = 12
  ref = O_element
FEATURE [App::DocumentObjectGroupPython] G4_BGO  # scripted group (container) (typed FeaturePython)
  Dunit = g/cm3
  Dvalue = 7.13
  Group = -> [Bi_element001,Ge_element001,O_element012]
  conduct = 2
  density = 1
  expand = 3
  formula = G4_BGO
  name = G4_BGO
  specific = 4
FEATURE [App::DocumentObjectGroupPython] H_element014  label="H_element : 0.102"  # scripted group (container) (typed FeaturePython)
  n = 0.102
FEATURE [App::DocumentObjectGroupPython] C_element014  label="C_element : 0.110"  # scripted group (container) (typed FeaturePython)
  n = 0.11
FEATURE [App::DocumentObjectGroupPython] N_element009  label="N_element : 0.033"  # scripted group (container) (typed FeaturePython)
  n = 0.033
FEATURE [App::DocumentObjectGroupPython] O_element013  label="O_element : 0.745"  # scripted group (container) (typed FeaturePython)
  n = 0.745
FEATURE [App::DocumentObjectGroupPython] Na_element002  label="Na_element : 0.002"  # scripted group (container) (typed FeaturePython)
  n = 0.001
FEATURE [App::DocumentObjectGroupPython] P_element001  label="P_element : 0.001"  # scripted group (container) (typed FeaturePython)
  n = 0.001
FEATURE [App::DocumentObjectGroupPython] S_element003  label="S_element : 0.002"  # scripted group (container) (typed FeaturePython)
  n = 0.002
FEATURE [App::DocumentObjectGroupPython] Cl_element002  label="Cl_element : 0.003"  # scripted group (container) (typed FeaturePython)
  n = 0.003
FEATURE [App::DocumentObjectGroupPython] K_element001  label="K_element : 0.002"  # scripted group (container) (typed FeaturePython)
  n = 0.002
FEATURE [App::DocumentObjectGroupPython] Fe_element001  label="Fe_element : 0.001"  # scripted group (container) (typed FeaturePython)
  n = 0.001
FEATURE [App::DocumentObjectGroupPython] G4_BLOOD_ICRP  # scripted group (container) (typed FeaturePython)
  Dunit = g/cm3
  Dvalue = 1.06
  Group = -> [H_element014,C_element014,N_element009,O_element013,Na_element002,P_element001,S_element003,Cl_element002,K_element001,Fe_element001]
  conduct = 2
  density = 1
  expand = 3
  formula = G4_BLOOD_ICRP
  name = G4_BLOOD_ICRP
  specific = 4
FEATURE [App::DocumentObjectGroupPython] H_element015  label="H_element : 0.064"  # scripted group (container) (typed FeaturePython)
  n = 0.064
FEATURE [App::DocumentObjectGroupPython] C_element015  label="C_element : 0.278"  # scripted group (container) (typed FeaturePython)
  n = 0.278
FEATURE [App::DocumentObjectGroupPython] N_element010  label="N_element : 0.027"  # scripted group (container) (typed FeaturePython)
  n = 0.027
FEATURE [App::DocumentObjectGroupPython] O_element014  label="O_element : 0.410"  # scripted group (container) (typed FeaturePython)
  n = 0.41
FEATURE [App::DocumentObjectGroupPython] Mg_element001  label="Mg_element : 0.002"  # scripted group (container) (typed FeaturePython)
  n = 0.002
FEATURE [App::DocumentObjectGroupPython] P_element002  label="P_element : 0.070"  # scripted group (container) (typed FeaturePython)
  n = 0.07
FEATURE [App::DocumentObjectGroupPython] S_element004  label="S_element : 0.003"  # scripted group (container) (typed FeaturePython)
  n = 0.002
FEATURE [App::DocumentObjectGroupPython] Ca_element003  label="Ca_element : 0.147"  # scripted group (container) (typed FeaturePython)
  n = 0.147
FEATURE [App::DocumentObjectGroupPython] G4_BONE_COMPACT_ICRU  # scripted group (container) (typed FeaturePython)
  Dunit = g/cm3
  Dvalue = 1.85
  Group = -> [H_element015,C_element015,N_element010,O_element014,Mg_element001,P_element002,S_element004,Ca_element003]
  conduct = 2
  density = 1
  expand = 3
  formula = G4_BONE_COMPACT_ICRU
  name = G4_BONE_COMPACT_ICRU
  specific = 4
FEATURE [App::DocumentObjectGroupPython] H_element016  label="H_element : 0.034"  # scripted group (container) (typed FeaturePython)
  n = 0.034
FEATURE [App::DocumentObjectGroupPython] C_element016  label="C_element : 0.155"  # scripted group (container) (typed FeaturePython)
  n = 0.155
FEATURE [App::DocumentObjectGroupPython] N_element011  label="N_element : 0.042"  # scripted group (container) (typed FeaturePython)
  n = 0.042
FEATURE [App::DocumentObjectGroupPython] O_element015  label="O_element : 0.435"  # scripted group (container) (typed FeaturePython)
  n = 0.435
FEATURE [App::DocumentObjectGroupPython] Na_element003  label="Na_element : 0.003"  # scripted group (container) (typed FeaturePython)
  n = 0.001
FEATURE [App::DocumentObjectGroupPython] Mg_element002  label="Mg_element : 0.003"  # scripted group (container) (typed FeaturePython)
  n = 0.002
FEATURE [App::DocumentObjectGroupPython] P_element003  label="P_element : 0.103"  # scripted group (container) (typed FeaturePython)
  n = 0.103
FEATURE [App::DocumentObjectGroupPython] S_element005  label="S_element : 0.004"  # scripted group (container) (typed FeaturePython)
  n = 0.003
FEATURE [App::DocumentObjectGroupPython] Ca_element004  label="Ca_element : 0.225"  # scripted group (container) (typed FeaturePython)
  n = 0.225
FEATURE [App::DocumentObjectGroupPython] G4_BONE_CORTICAL_ICRP  # scripted group (container) (typed FeaturePython)
  Dunit = g/cm3
  Dvalue = 1.92
  Group = -> [H_element016,C_element016,N_element011,O_element015,Na_element003,Mg_element002,P_element003,S_element005,Ca_element004]
  conduct = 2
  density = 1
  expand = 3
  formula = G4_BONE_CORTICAL_ICRP
  name = G4_BONE_CORTICAL_ICRP
  specific = 4
FEATURE [App::DocumentObjectGroupPython] B_element001  label="B_element : 4"  # scripted group (container) (typed FeaturePython)
  n = 4
  ref = B_element
FEATURE [App::DocumentObjectGroupPython] C_element017  label="C_element : 1"  # scripted group (container) (typed FeaturePython)
  n = 1
  ref = C_element
FEATURE [App::DocumentObjectGroupPython] G4_BORON_CARBIDE  # scripted group (container) (typed FeaturePython)
  Dunit = g/cm3
  Dvalue = 2.52
  Group = -> [B_element001,C_element017]
  conduct = 2
  density = 1
  expand = 3
  formula = G4_BORON_CARBIDE
  name = G4_BORON_CARBIDE
  specific = 4
FEATURE [App::DocumentObjectGroupPython] B_element002  label="B_element : 2"  # scripted group (container) (typed FeaturePython)
  n = 2
  ref = B_element
FEATURE [App::DocumentObjectGroupPython] O_element016  label="O_element : 006"  # scripted group (container) (typed FeaturePython)
  n = 3
  ref = O_element
FEATURE [App::DocumentObjectGroupPython] G4_BORON_OXIDE  # scripted group (container) (typed FeaturePython)
  Dunit = g/cm3
  Dvalue = 1.812
  Group = -> [B_element002,O_element016]
  conduct = 2
  density = 1
  expand = 3
  formula = G4_BORON_OXIDE
  name = G4_BORON_OXIDE
  specific = 4
FEATURE [App::DocumentObjectGroupPython] H_element017  label="H_element : 0.107"  # scripted group (container) (typed FeaturePython)
  n = 0.107
FEATURE [App::DocumentObjectGroupPython] C_element018  label="C_element : 0.145"  # scripted group (container) (typed FeaturePython)
  n = 0.145
FEATURE [App::DocumentObjectGroupPython] N_element012  label="N_element : 0.022"  # scripted group (container) (typed FeaturePython)
  n = 0.022
FEATURE [App::DocumentObjectGroupPython] O_element017  label="O_element : 0.712"  # scripted group (container) (typed FeaturePython)
  n = 0.712
FEATURE [App::DocumentObjectGroupPython] Na_element004  label="Na_element : 0.004"  # scripted group (container) (typed FeaturePython)
  n = 0.002
FEATURE [App::DocumentObjectGroupPython] P_element004  label="P_element : 0.004"  # scripted group (container) (typed FeaturePython)
  n = 0.004
FEATURE [App::DocumentObjectGroupPython] S_element006  label="S_element : 0.005"  # scripted group (container) (typed FeaturePython)
  n = 0.002
FEATURE [App::DocumentObjectGroupPython] Cl_element003  label="Cl_element : 0.004"  # scripted group (container) (typed FeaturePython)
  n = 0.003
FEATURE [App::DocumentObjectGroupPython] K_element002  label="K_element : 0.003"  # scripted group (container) (typed FeaturePython)
  n = 0.003
FEATURE [App::DocumentObjectGroupPython] G4_BRAIN_ICRP  # scripted group (container) (typed FeaturePython)
  Dunit = g/cm3
  Dvalue = 1.04
  Group = -> [H_element017,C_element018,N_element012,O_element017,Na_element004,P_element004,S_element006,Cl_element003,K_element002]
  conduct = 2
  density = 1
  expand = 3
  formula = G4_BRAIN_ICRP
  name = G4_BRAIN_ICRP
  specific = 4
FEATURE [App::DocumentObjectGroupPython] C_element019  label="C_element : 4"  # scripted group (container) (typed FeaturePython)
  n = 4
  ref = C_element
FEATURE [App::DocumentObjectGroupPython] H_element018  label="H_element : 010"  # scripted group (container) (typed FeaturePython)
  n = 10
  ref = H_element
FEATURE [App::DocumentObjectGroupPython] G4_BUTANE  # scripted group (container) (typed FeaturePython)
  Dunit = g/cm3
  Dvalue = 0.00249343
  Group = -> [C_element019,H_element018]
  conduct = 2
  density = 1
  expand = 3
  formula = G4_BUTANE
  name = G4_BUTANE
  specific = 4
FEATURE [App::DocumentObjectGroupPython] C_element020  label="C_element : 008"  # scripted group (container) (typed FeaturePython)
  n = 4
  ref = C_element
FEATURE [App::DocumentObjectGroupPython] H_element019  label="H_element : 011"  # scripted group (container) (typed FeaturePython)
  n = 10
  ref = H_element
FEATURE [App::DocumentObjectGroupPython] O_element018  label="O_element : 007"  # scripted group (container) (typed FeaturePython)
  n = 1
  ref = O_element
FEATURE [App::DocumentObjectGroupPython] G4_N_BUTYL_ALCOHOL  label="G4_N-BUTYL_ALCOHOL"  # scripted group (container) (typed FeaturePython)
  Dunit = g/cm3
  Dvalue = 0.8098
  Group = -> [C_element020,H_element019,O_element018]
  conduct = 2
  density = 1
  expand = 3
  formula = G4_N-BUTYL_ALCOHOL
  name = G4_N-BUTYL_ALCOHOL
  specific = 4
FEATURE [App::DocumentObjectGroupPython] H_element020  label="H_element : 0.025"  # scripted group (container) (typed FeaturePython)
  n = 0.02468
FEATURE [App::DocumentObjectGroupPython] C_element021  label="C_element : 0.502"  # scripted group (container) (typed FeaturePython)
  n = 0.501611
FEATURE [App::DocumentObjectGroupPython] O_element019  label="O_element : 0.005"  # scripted group (container) (typed FeaturePython)
  n = 0.004527
FEATURE [App::DocumentObjectGroupPython] F_element004  label="F_element : 0.465"  # scripted group (container) (typed FeaturePython)
  n = 0.465209
FEATURE [App::DocumentObjectGroupPython] Si_element001  label="Si_element : 0.004"  # scripted group (container) (typed FeaturePython)
  n = 0.003973
FEATURE [App::DocumentObjectGroupPython] G4_C_552  label="G4_C-552"  # scripted group (container) (typed FeaturePython)
  Dunit = g/cm3
  Dvalue = 1.76
  Group = -> [H_element020,C_element021,O_element019,F_element004,Si_element001]
  conduct = 2
  density = 1
  expand = 3
  formula = G4_C-552
  name = G4_C-552
  specific = 4
FEATURE [App::DocumentObjectGroupPython] Cd_element001  label="Cd_element : 1"  # scripted group (container) (typed FeaturePython)
  n = 1
  ref = Cd_element
FEATURE [App::DocumentObjectGroupPython] Te_element001  label="Te_element : 1"  # scripted group (container) (typed FeaturePython)
  n = 1
  ref = Te_element
FEATURE [App::DocumentObjectGroupPython] G4_CADMIUM_TELLURIDE  # scripted group (container) (typed FeaturePython)
  Dunit = g/cm3
  Dvalue = 6.2
  Group = -> [Cd_element001,Te_element001]
  conduct = 2
  density = 1
  expand = 3
  formula = G4_CADMIUM_TELLURIDE
  name = G4_CADMIUM_TELLURIDE
  specific = 4
FEATURE [App::DocumentObjectGroupPython] Cd_element002  label="Cd_element : 002"  # scripted group (container) (typed FeaturePython)
  n = 1
  ref = Cd_element
FEATURE [App::DocumentObjectGroupPython] W_element001  label="W_element : 1"  # scripted group (container) (typed FeaturePython)
  n = 1
  ref = W_element
FEATURE [App::DocumentObjectGroupPython] O_element020  label="O_element : 008"  # scripted group (container) (typed FeaturePython)
  n = 4
  ref = O_element
FEATURE [App::DocumentObjectGroupPython] G4_CADMIUM_TUNGSTATE  # scripted group (container) (typed FeaturePython)
  Dunit = g/cm3
  Dvalue = 7.9
  Group = -> [Cd_element002,W_element001,O_element020]
  conduct = 2
  density = 1
  expand = 3
  formula = G4_CADMIUM_TUNGSTATE
  name = G4_CADMIUM_TUNGSTATE
  specific = 4
FEATURE [App::DocumentObjectGroupPython] Ca_element005  label="Ca_element : 1"  # scripted group (container) (typed FeaturePython)
  n = 1
  ref = Ca_element
FEATURE [App::DocumentObjectGroupPython] C_element022  label="C_element : 009"  # scripted group (container) (typed FeaturePython)
  n = 1
  ref = C_element
FEATURE [App::DocumentObjectGroupPython] O_element021  label="O_element : 009"  # scripted group (container) (typed FeaturePython)
  n = 3
  ref = O_element
FEATURE [App::DocumentObjectGroupPython] G4_CALCIUM_CARBONATE  # scripted group (container) (typed FeaturePython)
  Dunit = g/cm3
  Dvalue = 2.8
  Group = -> [Ca_element005,C_element022,O_element021]
  conduct = 2
  density = 1
  expand = 3
  formula = G4_CALCIUM_CARBONATE
  name = G4_CALCIUM_CARBONATE
  specific = 4
FEATURE [App::DocumentObjectGroupPython] Ca_element006  label="Ca_element : 002"  # scripted group (container) (typed FeaturePython)
  n = 1
  ref = Ca_element
FEATURE [App::DocumentObjectGroupPython] F_element005  label="F_element : 003"  # scripted group (container) (typed FeaturePython)
  n = 2
  ref = F_element
FEATURE [App::DocumentObjectGroupPython] G4_CALCIUM_FLUORIDE  # scripted group (container) (typed FeaturePython)
  Dunit = g/cm3
  Dvalue = 3.18
  Group = -> [Ca_element006,F_element005]
  conduct = 2
  density = 1
  expand = 3
  formula = G4_CALCIUM_FLUORIDE
  name = G4_CALCIUM_FLUORIDE
  specific = 4
FEATURE [App::DocumentObjectGroupPython] Ca_element007  label="Ca_element : 003"  # scripted group (container) (typed FeaturePython)
  n = 1
  ref = Ca_element
FEATURE [App::DocumentObjectGroupPython] O_element022  label="O_element : 010"  # scripted group (container) (typed FeaturePython)
  n = 1
  ref = O_element
FEATURE [App::DocumentObjectGroupPython] G4_CALCIUM_OXIDE  # scripted group (container) (typed FeaturePython)
  Dunit = g/cm3
  Dvalue = 3.3
  Group = -> [Ca_element007,O_element022]
  conduct = 2
  density = 1
  expand = 3
  formula = G4_CALCIUM_OXIDE
  name = G4_CALCIUM_OXIDE
  specific = 4
FEATURE [App::DocumentObjectGroupPython] Ca_element008  label="Ca_element : 004"  # scripted group (container) (typed FeaturePython)
  n = 1
  ref = Ca_element
FEATURE [App::DocumentObjectGroupPython] S_element007  label="S_element : 002"  # scripted group (container) (typed FeaturePython)
  n = 1
  ref = S_element
FEATURE [App::DocumentObjectGroupPython] O_element023  label="O_element : 011"  # scripted group (container) (typed FeaturePython)
  n = 4
  ref = O_element
FEATURE [App::DocumentObjectGroupPython] G4_CALCIUM_SULFATE  # scripted group (container) (typed FeaturePython)
  Dunit = g/cm3
  Dvalue = 2.96
  Group = -> [Ca_element008,S_element007,O_element023]
  conduct = 2
  density = 1
  expand = 3
  formula = G4_CALCIUM_SULFATE
  name = G4_CALCIUM_SULFATE
  specific = 4
FEATURE [App::DocumentObjectGroupPython] Ca_element009  label="Ca_element : 005"  # scripted group (container) (typed FeaturePython)
  n = 1
  ref = Ca_element
FEATURE [App::DocumentObjectGroupPython] W_element002  label="W_element : 002"  # scripted group (container) (typed FeaturePython)
  n = 1
  ref = W_element
FEATURE [App::DocumentObjectGroupPython] O_element024  label="O_element : 012"  # scripted group (container) (typed FeaturePython)
  n = 4
  ref = O_element
FEATURE [App::DocumentObjectGroupPython] G4_CALCIUM_TUNGSTATE  # scripted group (container) (typed FeaturePython)
  Dunit = g/cm3
  Dvalue = 6.062
  Group = -> [Ca_element009,W_element002,O_element024]
  conduct = 2
  density = 1
  expand = 3
  formula = G4_CALCIUM_TUNGSTATE
  name = G4_CALCIUM_TUNGSTATE
  specific = 4
FEATURE [App::DocumentObjectGroupPython] C_element023  label="C_element : 010"  # scripted group (container) (typed FeaturePython)
  n = 1
  ref = C_element
FEATURE [App::DocumentObjectGroupPython] O_element025  label="O_element : 013"  # scripted group (container) (typed FeaturePython)
  n = 2
  ref = O_element
FEATURE [App::DocumentObjectGroupPython] G4_CARBON_DIOXIDE  # scripted group (container) (typed FeaturePython)
  Dunit = g/cm3
  Dvalue = 0.00184212
  Group = -> [C_element023,O_element025]
  conduct = 2
  density = 1
  expand = 3
  formula = G4_CARBON_DIOXIDE
  name = G4_CARBON_DIOXIDE
  specific = 4
FEATURE [App::DocumentObjectGroupPython] C_element024  label="C_element : 011"  # scripted group (container) (typed FeaturePython)
  n = 1
  ref = C_element
FEATURE [App::DocumentObjectGroupPython] Cl_element004  label="Cl_element : 4"  # scripted group (container) (typed FeaturePython)
  n = 4
  ref = Cl_element
FEATURE [App::DocumentObjectGroupPython] G4_CARBON_TETRACHLORIDE  # scripted group (container) (typed FeaturePython)
  Dunit = g/cm3
  Dvalue = 1.594
  Group = -> [C_element024,Cl_element004]
  conduct = 2
  density = 1
  expand = 3
  formula = G4_CARBON_TETRACHLORIDE
  name = G4_CARBON_TETRACHLORIDE
  specific = 4
FEATURE [App::DocumentObjectGroupPython] C_element025  label="C_element : 012"  # scripted group (container) (typed FeaturePython)
  n = 6
  ref = C_element
FEATURE [App::DocumentObjectGroupPython] H_element021  label="H_element : 012"  # scripted group (container) (typed FeaturePython)
  n = 10
  ref = H_element
FEATURE [App::DocumentObjectGroupPython] O_element026  label="O_element : 5"  # scripted group (container) (typed FeaturePython)
  n = 5
  ref = O_element
FEATURE [App::DocumentObjectGroupPython] G4_CELLULOSE_CELLOPHANE  # scripted group (container) (typed FeaturePython)
  Dunit = g/cm3
  Dvalue = 1.42
  Group = -> [C_element025,H_element021,O_element026]
  conduct = 2
  density = 1
  expand = 3
  formula = G4_CELLULOSE_CELLOPHANE
  name = G4_CELLULOSE_CELLOPHANE
  specific = 4
FEATURE [App::DocumentObjectGroupPython] H_element022  label="H_element : 0.067"  # scripted group (container) (typed FeaturePython)
  n = 0.067125
FEATURE [App::DocumentObjectGroupPython] C_element026  label="C_element : 0.545"  # scripted group (container) (typed FeaturePython)
  n = 0.545403
FEATURE [App::DocumentObjectGroupPython] O_element027  label="O_element : 0.387"  # scripted group (container) (typed FeaturePython)
  n = 0.387472
FEATURE [App::DocumentObjectGroupPython] G4_CELLULOSE_BUTYRATE  # scripted group (container) (typed FeaturePython)
  Dunit = g/cm3
  Dvalue = 1.2
  Group = -> [H_element022,C_element026,O_element027]
  conduct = 2
  density = 1
  expand = 3
  formula = G4_CELLULOSE_BUTYRATE
  name = G4_CELLULOSE_BUTYRATE
  specific = 4
FEATURE [App::DocumentObjectGroupPython] H_element023  label="H_element : 0.029"  # scripted group (container) (typed FeaturePython)
  n = 0.029216
FEATURE [App::DocumentObjectGroupPython] C_element027  label="C_element : 0.271"  # scripted group (container) (typed FeaturePython)
  n = 0.271296
FEATURE [App::DocumentObjectGroupPython] N_element013  label="N_element : 0.121"  # scripted group (container) (typed FeaturePython)
  n = 0.121276
FEATURE [App::DocumentObjectGroupPython] O_element028  label="O_element : 0.578"  # scripted group (container) (typed FeaturePython)
  n = 0.578212
FEATURE [App::DocumentObjectGroupPython] G4_CELLULOSE_NITRATE  # scripted group (container) (typed FeaturePython)
  Dunit = g/cm3
  Dvalue = 1.49
  Group = -> [H_element023,C_element027,N_element013,O_element028]
  conduct = 2
  density = 1
  expand = 3
  formula = G4_CELLULOSE_NITRATE
  name = G4_CELLULOSE_NITRATE
  specific = 4
FEATURE [App::DocumentObjectGroupPython] H_element024  label="H_element : 0.108"  # scripted group (container) (typed FeaturePython)
  n = 0.107596
FEATURE [App::DocumentObjectGroupPython] N_element014  label="N_element : 0.001"  # scripted group (container) (typed FeaturePython)
  n = 0.0008
FEATURE [App::DocumentObjectGroupPython] O_element029  label="O_element : 0.875"  # scripted group (container) (typed FeaturePython)
  n = 0.874976
FEATURE [App::DocumentObjectGroupPython] S_element008  label="S_element : 0.015"  # scripted group (container) (typed FeaturePython)
  n = 0.014627
FEATURE [App::DocumentObjectGroupPython] Ce_element001  label="Ce_element : 0.002"  # scripted group (container) (typed FeaturePython)
  n = 0.002001
FEATURE [App::DocumentObjectGroupPython] G4_CERIC_SULFATE  # scripted group (container) (typed FeaturePython)
  Dunit = g/cm3
  Dvalue = 1.03
  Group = -> [H_element024,N_element014,O_element029,S_element008,Ce_element001]
  conduct = 2
  density = 1
  expand = 3
  formula = G4_CERIC_SULFATE
  name = G4_CERIC_SULFATE
  specific = 4
FEATURE [App::DocumentObjectGroupPython] Cs_element001  label="Cs_element : 1"  # scripted group (container) (typed FeaturePython)
  n = 1
  ref = Cs_element
FEATURE [App::DocumentObjectGroupPython] F_element006  label="F_element : 1"  # scripted group (container) (typed FeaturePython)
  n = 1
  ref = F_element
FEATURE [App::DocumentObjectGroupPython] G4_CESIUM_FLUORIDE  # scripted group (container) (typed FeaturePython)
  Dunit = g/cm3
  Dvalue = 4.115
  Group = -> [Cs_element001,F_element006]
  conduct = 2
  density = 1
  expand = 3
  formula = G4_CESIUM_FLUORIDE
  name = G4_CESIUM_FLUORIDE
  specific = 4
FEATURE [App::DocumentObjectGroupPython] Cs_element002  label="Cs_element : 002"  # scripted group (container) (typed FeaturePython)
  n = 1
  ref = Cs_element
FEATURE [App::DocumentObjectGroupPython] I_element001  label="I_element : 1"  # scripted group (container) (typed FeaturePython)
  n = 1
  ref = I_element
FEATURE [App::DocumentObjectGroupPython] G4_CESIUM_IODIDE  # scripted group (container) (typed FeaturePython)
  Dunit = g/cm3
  Dvalue = 4.51
  Group = -> [Cs_element002,I_element001]
  conduct = 2
  density = 1
  expand = 3
  formula = G4_CESIUM_IODIDE
  name = G4_CESIUM_IODIDE
  specific = 4
FEATURE [App::DocumentObjectGroupPython] C_element028  label="C_element : 013"  # scripted group (container) (typed FeaturePython)
  n = 6
  ref = C_element
FEATURE [App::DocumentObjectGroupPython] H_element025  label="H_element : 013"  # scripted group (container) (typed FeaturePython)
  n = 5
  ref = H_element
FEATURE [App::DocumentObjectGroupPython] Cl_element005  label="Cl_element : 1"  # scripted group (container) (typed FeaturePython)
  n = 1
  ref = Cl_element
FEATURE [App::DocumentObjectGroupPython] G4_CHLOROBENZENE  # scripted group (container) (typed FeaturePython)
  Dunit = g/cm3
  Dvalue = 1.1058
  Group = -> [C_element028,H_element025,Cl_element005]
  conduct = 2
  density = 1
  expand = 3
  formula = G4_CHLOROBENZENE
  name = G4_CHLOROBENZENE
  specific = 4
FEATURE [App::DocumentObjectGroupPython] C_element029  label="C_element : 014"  # scripted group (container) (typed FeaturePython)
  n = 1
  ref = C_element
FEATURE [App::DocumentObjectGroupPython] H_element026  label="H_element : 1"  # scripted group (container) (typed FeaturePython)
  n = 1
  ref = H_element
FEATURE [App::DocumentObjectGroupPython] Cl_element006  label="Cl_element : 3"  # scripted group (container) (typed FeaturePython)
  n = 3
  ref = Cl_element
FEATURE [App::DocumentObjectGroupPython] G4_CHLOROFORM  # scripted group (container) (typed FeaturePython)
  Dunit = g/cm3
  Dvalue = 1.4832
  Group = -> [C_element029,H_element026,Cl_element006]
  conduct = 2
  density = 1
  expand = 3
  formula = G4_CHLOROFORM
  name = G4_CHLOROFORM
  specific = 4
FEATURE [App::DocumentObjectGroupPython] H_element027  label="H_element : 0.010"  # scripted group (container) (typed FeaturePython)
  n = 0.01
FEATURE [App::DocumentObjectGroupPython] C_element030  label="C_element : 0.001"  # scripted group (container) (typed FeaturePython)
  n = 0.001
FEATURE [App::DocumentObjectGroupPython] O_element030  label="O_element : 0.529"  # scripted group (container) (typed FeaturePython)
  n = 0.529107
FEATURE [App::DocumentObjectGroupPython] Na_element005  label="Na_element : 0.016"  # scripted group (container) (typed FeaturePython)
  n = 0.016
FEATURE [App::DocumentObjectGroupPython] Mg_element003  label="Mg_element : 0.004"  # scripted group (container) (typed FeaturePython)
  n = 0.002
FEATURE [App::DocumentObjectGroupPython] Al_element002  label="Al_element : 0.034"  # scripted group (container) (typed FeaturePython)
  n = 0.033872
FEATURE [App::DocumentObjectGroupPython] Si_element002  label="Si_element : 0.337"  # scripted group (container) (typed FeaturePython)
  n = 0.337021
FEATURE [App::DocumentObjectGroupPython] K_element003  label="K_element : 0.013"  # scripted group (container) (typed FeaturePython)
  n = 0.013
FEATURE [App::DocumentObjectGroupPython] Ca_element010  label="Ca_element : 0.044"  # scripted group (container) (typed FeaturePython)
  n = 0.044
FEATURE [App::DocumentObjectGroupPython] Fe_element002  label="Fe_element : 0.014"  # scripted group (container) (typed FeaturePython)
  n = 0.014
FEATURE [App::DocumentObjectGroupPython] G4_CONCRETE  # scripted group (container) (typed FeaturePython)
  Dunit = g/cm3
  Dvalue = 2.3
  Group = -> [H_element027,C_element030,O_element030,Na_element005,Mg_element003,Al_element002,Si_element002,K_element003,Ca_element010,Fe_element002]
  conduct = 2
  density = 1
  expand = 3
  formula = G4_CONCRETE
  name = G4_CONCRETE
  specific = 4
FEATURE [App::DocumentObjectGroupPython] C_element031  label="C_element : 015"  # scripted group (container) (typed FeaturePython)
  n = 6
  ref = C_element
FEATURE [App::DocumentObjectGroupPython] H_element028  label="H_element : 12"  # scripted group (container) (typed FeaturePython)
  n = 12
  ref = H_element
FEATURE [App::DocumentObjectGroupPython] G4_CYCLOHEXANE  # scripted group (container) (typed FeaturePython)
  Dunit = g/cm3
  Dvalue = 0.779
  Group = -> [C_element031,H_element028]
  conduct = 2
  density = 1
  expand = 3
  formula = G4_CYCLOHEXANE
  name = G4_CYCLOHEXANE
  specific = 4
FEATURE [App::DocumentObjectGroupPython] C_element032  label="C_element : 016"  # scripted group (container) (typed FeaturePython)
  n = 6
  ref = C_element
FEATURE [App::DocumentObjectGroupPython] H_element029  label="H_element : 4"  # scripted group (container) (typed FeaturePython)
  n = 4
  ref = H_element
FEATURE [App::DocumentObjectGroupPython] Cl_element007  label="Cl_element : 2"  # scripted group (container) (typed FeaturePython)
  n = 2
  ref = Cl_element
FEATURE [App::DocumentObjectGroupPython] G4_1_2_DICHLOROBENZENE  label="G4_1.2-DICHLOROBENZENE"  # scripted group (container) (typed FeaturePython)
  Dunit = g/cm3
  Dvalue = 1.3048
  Group = -> [C_element032,H_element029,Cl_element007]
  conduct = 2
  density = 1
  expand = 3
  formula = G4_1.2-DICHLOROBENZENE
  name = G4_1.2-DICHLOROBENZENE
  specific = 4
FEATURE [App::DocumentObjectGroupPython] C_element033  label="C_element : 017"  # scripted group (container) (typed FeaturePython)
  n = 4
  ref = C_element
FEATURE [App::DocumentObjectGroupPython] H_element030  label="H_element : 8"  # scripted group (container) (typed FeaturePython)
  n = 8
  ref = H_element
FEATURE [App::DocumentObjectGroupPython] O_element031  label="O_element : 014"  # scripted group (container) (typed FeaturePython)
  n = 1
  ref = O_element
FEATURE [App::DocumentObjectGroupPython] Cl_element008  label="Cl_element : 005"  # scripted group (container) (typed FeaturePython)
  n = 2
  ref = Cl_element
FEATURE [App::DocumentObjectGroupPython] G4_DICHLORODIETHYL_ETHER  # scripted group (container) (typed FeaturePython)
  Dunit = g/cm3
  Dvalue = 1.2199
  Group = -> [C_element033,H_element030,O_element031,Cl_element008]
  conduct = 2
  density = 1
  expand = 3
  formula = G4_DICHLORODIETHYL_ETHER
  name = G4_DICHLORODIETHYL_ETHER
  specific = 4
FEATURE [App::DocumentObjectGroupPython] C_element034  label="C_element : 018"  # scripted group (container) (typed FeaturePython)
  n = 2
  ref = C_element
FEATURE [App::DocumentObjectGroupPython] H_element031  label="H_element : 014"  # scripted group (container) (typed FeaturePython)
  n = 4
  ref = H_element
FEATURE [App::DocumentObjectGroupPython] Cl_element009  label="Cl_element : 006"  # scripted group (container) (typed FeaturePython)
  n = 2
  ref = Cl_element
FEATURE [App::DocumentObjectGroupPython] G4_1_2_DICHLOROETHANE  label="G4_1.2-DICHLOROETHANE"  # scripted group (container) (typed FeaturePython)
  Dunit = g/cm3
  Dvalue = 1.2351
  Group = -> [C_element034,H_element031,Cl_element009]
  conduct = 2
  density = 1
  expand = 3
  formula = G4_1.2-DICHLOROETHANE
  name = G4_1.2-DICHLOROETHANE
  specific = 4
FEATURE [App::DocumentObjectGroupPython] C_element035  label="C_element : 019"  # scripted group (container) (typed FeaturePython)
  n = 4
  ref = C_element
FEATURE [App::DocumentObjectGroupPython] H_element032  label="H_element : 015"  # scripted group (container) (typed FeaturePython)
  n = 10
  ref = H_element
FEATURE [App::DocumentObjectGroupPython] O_element032  label="O_element : 015"  # scripted group (container) (typed FeaturePython)
  n = 1
  ref = O_element
FEATURE [App::DocumentObjectGroupPython] G4_DIETHYL_ETHER  # scripted group (container) (typed FeaturePython)
  Dunit = g/cm3
  Dvalue = 0.71378
  Group = -> [C_element035,H_element032,O_element032]
  conduct = 2
  density = 1
  expand = 3
  formula = G4_DIETHYL_ETHER
  name = G4_DIETHYL_ETHER
  specific = 4
FEATURE [App::DocumentObjectGroupPython] C_element036  label="C_element : 020"  # scripted group (container) (typed FeaturePython)
  n = 3
  ref = C_element
FEATURE [App::DocumentObjectGroupPython] H_element033  label="H_element : 016"  # scripted group (container) (typed FeaturePython)
  n = 7
  ref = H_element
FEATURE [App::DocumentObjectGroupPython] N_element015  label="N_element : 008"  # scripted group (container) (typed FeaturePython)
  n = 1
  ref = N_element
FEATURE [App::DocumentObjectGroupPython] O_element033  label="O_element : 016"  # scripted group (container) (typed FeaturePython)
  n = 1
  ref = O_element
FEATURE [App::DocumentObjectGroupPython] G4_N_N_DIMETHYL_FORMAMIDE  label="G4_N.N-DIMETHYL_FORMAMIDE"  # scripted group (container) (typed FeaturePython)
  Dunit = g/cm3
  Dvalue = 0.9487
  Group = -> [C_element036,H_element033,N_element015,O_element033]
  conduct = 2
  density = 1
  expand = 3
  formula = G4_N.N-DIMETHYL_FORMAMIDE
  name = G4_N.N-DIMETHYL_FORMAMIDE
  specific = 4
FEATURE [App::DocumentObjectGroupPython] C_element037  label="C_element : 021"  # scripted group (container) (typed FeaturePython)
  n = 2
  ref = C_element
FEATURE [App::DocumentObjectGroupPython] H_element034  label="H_element : 017"  # scripted group (container) (typed FeaturePython)
  n = 6
  ref = H_element
FEATURE [App::DocumentObjectGroupPython] O_element034  label="O_element : 017"  # scripted group (container) (typed FeaturePython)
  n = 1
  ref = O_element
FEATURE [App::DocumentObjectGroupPython] S_element009  label="S_element : 003"  # scripted group (container) (typed FeaturePython)
  n = 1
  ref = S_element
FEATURE [App::DocumentObjectGroupPython] G4_DIMETHYL_SULFOXIDE  # scripted group (container) (typed FeaturePython)
  Dunit = g/cm3
  Dvalue = 1.1014
  Group = -> [C_element037,H_element034,O_element034,S_element009]
  conduct = 2
  density = 1
  expand = 3
  formula = G4_DIMETHYL_SULFOXIDE
  name = G4_DIMETHYL_SULFOXIDE
  specific = 4
FEATURE [App::DocumentObjectGroupPython] C_element038  label="C_element : 022"  # scripted group (container) (typed FeaturePython)
  n = 2
  ref = C_element
FEATURE [App::DocumentObjectGroupPython] H_element035  label="H_element : 018"  # scripted group (container) (typed FeaturePython)
  n = 6
  ref = H_element
FEATURE [App::DocumentObjectGroupPython] G4_ETHANE  # scripted group (container) (typed FeaturePython)
  Dunit = g/cm3
  Dvalue = 0.00125324
  Group = -> [C_element038,H_element035]
  conduct = 2
  density = 1
  expand = 3
  formula = G4_ETHANE
  name = G4_ETHANE
  specific = 4
FEATURE [App::DocumentObjectGroupPython] C_element039  label="C_element : 023"  # scripted group (container) (typed FeaturePython)
  n = 2
  ref = C_element
FEATURE [App::DocumentObjectGroupPython] H_element036  label="H_element : 019"  # scripted group (container) (typed FeaturePython)
  n = 6
  ref = H_element
FEATURE [App::DocumentObjectGroupPython] O_element035  label="O_element : 018"  # scripted group (container) (typed FeaturePython)
  n = 1
  ref = O_element
FEATURE [App::DocumentObjectGroupPython] G4_ETHYL_ALCOHOL  # scripted group (container) (typed FeaturePython)
  Dunit = g/cm3
  Dvalue = 0.7893
  Group = -> [C_element039,H_element036,O_element035]
  conduct = 2
  density = 1
  expand = 3
  formula = G4_ETHYL_ALCOHOL
  name = G4_ETHYL_ALCOHOL
  specific = 4
FEATURE [App::DocumentObjectGroupPython] H_element037  label="H_element : 0.090"  # scripted group (container) (typed FeaturePython)
  n = 0.090027
FEATURE [App::DocumentObjectGroupPython] C_element040  label="C_element : 0.585"  # scripted group (container) (typed FeaturePython)
  n = 0.585182
FEATURE [App::DocumentObjectGroupPython] O_element036  label="O_element : 0.325"  # scripted group (container) (typed FeaturePython)
  n = 0.324791
FEATURE [App::DocumentObjectGroupPython] G4_ETHYL_CELLULOSE  # scripted group (container) (typed FeaturePython)
  Dunit = g/cm3
  Dvalue = 1.13
  Group = -> [H_element037,C_element040,O_element036]
  conduct = 2
  density = 1
  expand = 3
  formula = G4_ETHYL_CELLULOSE
  name = G4_ETHYL_CELLULOSE
  specific = 4
FEATURE [App::DocumentObjectGroupPython] C_element041  label="C_element : 024"  # scripted group (container) (typed FeaturePython)
  n = 2
  ref = C_element
FEATURE [App::DocumentObjectGroupPython] H_element038  label="H_element : 020"  # scripted group (container) (typed FeaturePython)
  n = 4
  ref = H_element
FEATURE [App::DocumentObjectGroupPython] G4_ETHYLENE  # scripted group (container) (typed FeaturePython)
  Dunit = g/cm3
  Dvalue = 0.00117497
  Group = -> [C_element041,H_element038]
  conduct = 2
  density = 1
  expand = 3
  formula = G4_ETHYLENE
  name = G4_ETHYLENE
  specific = 4
FEATURE [App::DocumentObjectGroupPython] H_element039  label="H_element : 0.096"  # scripted group (container) (typed FeaturePython)
  n = 0.096
FEATURE [App::DocumentObjectGroupPython] C_element042  label="C_element : 0.195"  # scripted group (container) (typed FeaturePython)
  n = 0.195
FEATURE [App::DocumentObjectGroupPython] N_element016  label="N_element : 0.057"  # scripted group (container) (typed FeaturePython)
  n = 0.057
FEATURE [App::DocumentObjectGroupPython] O_element037  label="O_element : 0.646"  # scripted group (container) (typed FeaturePython)
  n = 0.646
FEATURE [App::DocumentObjectGroupPython] Na_element006  label="Na_element : 0.017"  # scripted group (container) (typed FeaturePython)
  n = 0.001
FEATURE [App::DocumentObjectGroupPython] P_element005  label="P_element : 0.104"  # scripted group (container) (typed FeaturePython)
  n = 0.001
FEATURE [App::DocumentObjectGroupPython] S_element010  label="S_element : 0.016"  # scripted group (container) (typed FeaturePython)
  n = 0.003
FEATURE [App::DocumentObjectGroupPython] Cl_element010  label="Cl_element : 0.005"  # scripted group (container) (typed FeaturePython)
  n = 0.001
FEATURE [App::DocumentObjectGroupPython] G4_EYE_LENS_ICRP  # scripted group (container) (typed FeaturePython)
  Dunit = g/cm3
  Dvalue = 1.07
  Group = -> [H_element039,C_element042,N_element016,O_element037,Na_element006,P_element005,S_element010,Cl_element010]
  conduct = 2
  density = 1
  expand = 3
  formula = G4_EYE_LENS_ICRP
  name = G4_EYE_LENS_ICRP
  specific = 4
FEATURE [App::DocumentObjectGroupPython] Fe_element003  label="Fe_element : 2"  # scripted group (container) (typed FeaturePython)
  n = 2
  ref = Fe_element
FEATURE [App::DocumentObjectGroupPython] O_element038  label="O_element : 019"  # scripted group (container) (typed FeaturePython)
  n = 3
  ref = O_element
FEATURE [App::DocumentObjectGroupPython] G4_FERRIC_OXIDE  # scripted group (container) (typed FeaturePython)
  Dunit = g/cm3
  Dvalue = 5.2
  Group = -> [Fe_element003,O_element038]
  conduct = 2
  density = 1
  expand = 3
  formula = G4_FERRIC_OXIDE
  name = G4_FERRIC_OXIDE
  specific = 4
FEATURE [App::DocumentObjectGroupPython] Fe_element004  label="Fe_element : 1"  # scripted group (container) (typed FeaturePython)
  n = 1
  ref = Fe_element
FEATURE [App::DocumentObjectGroupPython] B_element003  label="B_element : 1"  # scripted group (container) (typed FeaturePython)
  n = 1
  ref = B_element
FEATURE [App::DocumentObjectGroupPython] G4_FERROBORIDE  # scripted group (container) (typed FeaturePython)
  Dunit = g/cm3
  Dvalue = 7.15
  Group = -> [Fe_element004,B_element003]
  conduct = 2
  density = 1
  expand = 3
  formula = G4_FERROBORIDE
  name = G4_FERROBORIDE
  specific = 4
FEATURE [App::DocumentObjectGroupPython] Fe_element005  label="Fe_element : 003"  # scripted group (container) (typed FeaturePython)
  n = 1
  ref = Fe_element
FEATURE [App::DocumentObjectGroupPython] O_element039  label="O_element : 020"  # scripted group (container) (typed FeaturePython)
  n = 1
  ref = O_element
FEATURE [App::DocumentObjectGroupPython] G4_FERROUS_OXIDE  # scripted group (container) (typed FeaturePython)
  Dunit = g/cm3
  Dvalue = 5.7
  Group = -> [Fe_element005,O_element039]
  conduct = 2
  density = 1
  expand = 3
  formula = G4_FERROUS_OXIDE
  name = G4_FERROUS_OXIDE
  specific = 4
FEATURE [App::DocumentObjectGroupPython] H_element040  label="H_element : 0.115"  # scripted group (container) (typed FeaturePython)
  n = 0.108259
FEATURE [App::DocumentObjectGroupPython] N_element017  label="N_element : 0.000"  # scripted group (container) (typed FeaturePython)
  n = 2.7e-05
FEATURE [App::DocumentObjectGroupPython] O_element040  label="O_element : 0.879"  # scripted group (container) (typed FeaturePython)
  n = 0.878636
FEATURE [App::DocumentObjectGroupPython] Na_element007  label="Na_element : 0.000"  # scripted group (container) (typed FeaturePython)
  n = 2.2e-05
FEATURE [App::DocumentObjectGroupPython] S_element011  label="S_element : 0.013"  # scripted group (container) (typed FeaturePython)
  n = 0.012968
FEATURE [App::DocumentObjectGroupPython] Cl_element011  label="Cl_element : 0.000"  # scripted group (container) (typed FeaturePython)
  n = 3.4e-05
FEATURE [App::DocumentObjectGroupPython] Fe_element006  label="Fe_element : 0.000"  # scripted group (container) (typed FeaturePython)
  n = 5.4e-05
FEATURE [App::DocumentObjectGroupPython] G4_FERROUS_SULFATE  # scripted group (container) (typed FeaturePython)
  Dunit = g/cm3
  Dvalue = 1.024
  Group = -> [H_element040,N_element017,O_element040,Na_element007,S_element011,Cl_element011,Fe_element006]
  conduct = 2
  density = 1
  expand = 3
  formula = G4_FERROUS_SULFATE
  name = G4_FERROUS_SULFATE
  specific = 4
FEATURE [App::DocumentObjectGroupPython] C_element043  label="C_element : 0.099"  # scripted group (container) (typed FeaturePython)
  n = 0.099335
FEATURE [App::DocumentObjectGroupPython] F_element007  label="F_element : 0.314"  # scripted group (container) (typed FeaturePython)
  n = 0.314247
FEATURE [App::DocumentObjectGroupPython] Cl_element012  label="Cl_element : 0.586"  # scripted group (container) (typed FeaturePython)
  n = 0.586418
FEATURE [App::DocumentObjectGroupPython] G4_FREON_12  label="G4_FREON-12"  # scripted group (container) (typed FeaturePython)
  Dunit = g/cm3
  Dvalue = 1.12
  Group = -> [C_element043,F_element007,Cl_element012]
  conduct = 2
  density = 1
  expand = 3
  formula = G4_FREON-12
  name = G4_FREON-12
  specific = 4
FEATURE [App::DocumentObjectGroupPython] C_element044  label="C_element : 0.057"  # scripted group (container) (typed FeaturePython)
  n = 0.057245
FEATURE [App::DocumentObjectGroupPython] F_element008  label="F_element : 0.181"  # scripted group (container) (typed FeaturePython)
  n = 0.181096
FEATURE [App::DocumentObjectGroupPython] Br_element001  label="Br_element : 0.762"  # scripted group (container) (typed FeaturePython)
  n = 0.761659
FEATURE [App::DocumentObjectGroupPython] G4_FREON_12B2  label="G4_FREON-12B2"  # scripted group (container) (typed FeaturePython)
  Dunit = g/cm3
  Dvalue = 1.8
  Group = -> [C_element044,F_element008,Br_element001]
  conduct = 2
  density = 1
  expand = 3
  formula = G4_FREON-12B2
  name = G4_FREON-12B2
  specific = 4
FEATURE [App::DocumentObjectGroupPython] C_element045  label="C_element : 0.115"  # scripted group (container) (typed FeaturePython)
  n = 0.114983
FEATURE [App::DocumentObjectGroupPython] F_element009  label="F_element : 0.546"  # scripted group (container) (typed FeaturePython)
  n = 0.545621
FEATURE [App::DocumentObjectGroupPython] Cl_element013  label="Cl_element : 0.339"  # scripted group (container) (typed FeaturePython)
  n = 0.339396
FEATURE [App::DocumentObjectGroupPython] G4_FREON_13  label="G4_FREON-13"  # scripted group (container) (typed FeaturePython)
  Dunit = g/cm3
  Dvalue = 0.95
  Group = -> [C_element045,F_element009,Cl_element013]
  conduct = 2
  density = 1
  expand = 3
  formula = G4_FREON-13
  name = G4_FREON-13
  specific = 4
FEATURE [App::DocumentObjectGroupPython] C_element046  label="C_element : 025"  # scripted group (container) (typed FeaturePython)
  n = 1
  ref = C_element
FEATURE [App::DocumentObjectGroupPython] F_element010  label="F_element : 3"  # scripted group (container) (typed FeaturePython)
  n = 3
  ref = F_element
FEATURE [App::DocumentObjectGroupPython] Br_element002  label="Br_element : 1"  # scripted group (container) (typed FeaturePython)
  n = 1
  ref = Br_element
FEATURE [App::DocumentObjectGroupPython] G4_FREON_13B1  label="G4_FREON-13B1"  # scripted group (container) (typed FeaturePython)
  Dunit = g/cm3
  Dvalue = 1.5
  Group = -> [C_element046,F_element010,Br_element002]
  conduct = 2
  density = 1
  expand = 3
  formula = G4_FREON-13B1
  name = G4_FREON-13B1
  specific = 4
FEATURE [App::DocumentObjectGroupPython] C_element047  label="C_element : 0.061"  # scripted group (container) (typed FeaturePython)
  n = 0.061309
FEATURE [App::DocumentObjectGroupPython] F_element011  label="F_element : 0.291"  # scripted group (container) (typed FeaturePython)
  n = 0.290924
FEATURE [App::DocumentObjectGroupPython] I_element002  label="I_element : 0.648"  # scripted group (container) (typed FeaturePython)
  n = 0.647767
FEATURE [App::DocumentObjectGroupPython] G4_FREON_13I1  label="G4_FREON-13I1"  # scripted group (container) (typed FeaturePython)
  Dunit = g/cm3
  Dvalue = 1.8
  Group = -> [C_element047,F_element011,I_element002]
  conduct = 2
  density = 1
  expand = 3
  formula = G4_FREON-13I1
  name = G4_FREON-13I1
  specific = 4
FEATURE [App::DocumentObjectGroupPython] Gd_element001  label="Gd_element : 2"  # scripted group (container) (typed FeaturePython)
  n = 2
  ref = Gd_element
FEATURE [App::DocumentObjectGroupPython] O_element041  label="O_element : 021"  # scripted group (container) (typed FeaturePython)
  n = 2
  ref = O_element
FEATURE [App::DocumentObjectGroupPython] S_element012  label="S_element : 004"  # scripted group (container) (typed FeaturePython)
  n = 1
  ref = S_element
FEATURE [App::DocumentObjectGroupPython] G4_GADOLINIUM_OXYSULFIDE  # scripted group (container) (typed FeaturePython)
  Dunit = g/cm3
  Dvalue = 7.44
  Group = -> [Gd_element001,O_element041,S_element012]
  conduct = 2
  density = 1
  expand = 3
  formula = G4_GADOLINIUM_OXYSULFIDE
  name = G4_GADOLINIUM_OXYSULFIDE
  specific = 4
FEATURE [App::DocumentObjectGroupPython] Ga_element001  label="Ga_element : 1"  # scripted group (container) (typed FeaturePython)
  n = 1
  ref = Ga_element
FEATURE [App::DocumentObjectGroupPython] As_element001  label="As_element : 1"  # scripted group (container) (typed FeaturePython)
  n = 1
  ref = As_element
FEATURE [App::DocumentObjectGroupPython] G4_GALLIUM_ARSENIDE  # scripted group (container) (typed FeaturePython)
  Dunit = g/cm3
  Dvalue = 5.31
  Group = -> [Ga_element001,As_element001]
  conduct = 2
  density = 1
  expand = 3
  formula = G4_GALLIUM_ARSENIDE
  name = G4_GALLIUM_ARSENIDE
  specific = 4
FEATURE [App::DocumentObjectGroupPython] H_element041  label="H_element : 0.081"  # scripted group (container) (typed FeaturePython)
  n = 0.08118
FEATURE [App::DocumentObjectGroupPython] C_element048  label="C_element : 0.416"  # scripted group (container) (typed FeaturePython)
  n = 0.41606
FEATURE [App::DocumentObjectGroupPython] N_element018  label="N_element : 0.111"  # scripted group (container) (typed FeaturePython)
  n = 0.11124
FEATURE [App::DocumentObjectGroupPython] O_element042  label="O_element : 0.381"  # scripted group (container) (typed FeaturePython)
  n = 0.38064
FEATURE [App::DocumentObjectGroupPython] S_element013  label="S_element : 0.011"  # scripted group (container) (typed FeaturePython)
  n = 0.01088
FEATURE [App::DocumentObjectGroupPython] G4_GEL_PHOTO_EMULSION  # scripted group (container) (typed FeaturePython)
  Dunit = g/cm3
  Dvalue = 1.2914
  Group = -> [H_element041,C_element048,N_element018,O_element042,S_element013]
  conduct = 2
  density = 1
  expand = 3
  formula = G4_GEL_PHOTO_EMULSION
  name = G4_GEL_PHOTO_EMULSION
  specific = 4
FEATURE [App::DocumentObjectGroupPython] B_element004  label="B_element : 0.040"  # scripted group (container) (typed FeaturePython)
  n = 0.0400639
FEATURE [App::DocumentObjectGroupPython] O_element043  label="O_element : 0.540"  # scripted group (container) (typed FeaturePython)
  n = 0.539561
FEATURE [App::DocumentObjectGroupPython] Na_element008  label="Na_element : 0.028"  # scripted group (container) (typed FeaturePython)
  n = 0.0281909
FEATURE [App::DocumentObjectGroupPython] Al_element003  label="Al_element : 0.012"  # scripted group (container) (typed FeaturePython)
  n = 0.011644
FEATURE [App::DocumentObjectGroupPython] Si_element003  label="Si_element : 0.377"  # scripted group (container) (typed FeaturePython)
  n = 0.377219
FEATURE [App::DocumentObjectGroupPython] K_element004  label="K_element : 0.014"  # scripted group (container) (typed FeaturePython)
  n = 0.00332099
FEATURE [App::DocumentObjectGroupPython] G4_Pyrex_Glass  # scripted group (container) (typed FeaturePython)
  Dunit = g/cm3
  Dvalue = 2.23
  Group = -> [B_element004,O_element043,Na_element008,Al_element003,Si_element003,K_element004]
  conduct = 2
  density = 1
  expand = 3
  formula = G4_Pyrex_Glass
  name = G4_Pyrex_Glass
  specific = 4
FEATURE [App::DocumentObjectGroupPython] O_element044  label="O_element : 0.156"  # scripted group (container) (typed FeaturePython)
  n = 0.156453
FEATURE [App::DocumentObjectGroupPython] Si_element004  label="Si_element : 0.081"  # scripted group (container) (typed FeaturePython)
  n = 0.080866
FEATURE [App::DocumentObjectGroupPython] Ti_element001  label="Ti_element : 0.008"  # scripted group (container) (typed FeaturePython)
  n = 0.008092
FEATURE [App::DocumentObjectGroupPython] As_element002  label="As_element : 0.003"  # scripted group (container) (typed FeaturePython)
  n = 0.002651
FEATURE [App::DocumentObjectGroupPython] Pb_element001  label="Pb_element : 0.752"  # scripted group (container) (typed FeaturePython)
  n = 0.751938
FEATURE [App::DocumentObjectGroupPython] G4_GLASS_LEAD  # scripted group (container) (typed FeaturePython)
  Dunit = g/cm3
  Dvalue = 6.22
  Group = -> [O_element044,Si_element004,Ti_element001,As_element002,Pb_element001]
  conduct = 2
  density = 1
  expand = 3
  formula = G4_GLASS_LEAD
  name = G4_GLASS_LEAD
  specific = 4
FEATURE [App::DocumentObjectGroupPython] O_element045  label="O_element : 0.460"  # scripted group (container) (typed FeaturePython)
  n = 0.4598
FEATURE [App::DocumentObjectGroupPython] Na_element009  label="Na_element : 0.096"  # scripted group (container) (typed FeaturePython)
  n = 0.0964411
FEATURE [App::DocumentObjectGroupPython] Si_element005  label="Si_element : 0.378"  # scripted group (container) (typed FeaturePython)
  n = 0.336553
FEATURE [App::DocumentObjectGroupPython] Ca_element011  label="Ca_element : 0.107"  # scripted group (container) (typed FeaturePython)
  n = 0.107205
FEATURE [App::DocumentObjectGroupPython] G4_GLASS_PLATE  # scripted group (container) (typed FeaturePython)
  Dunit = g/cm3
  Dvalue = 2.4
  Group = -> [O_element045,Na_element009,Si_element005,Ca_element011]
  conduct = 2
  density = 1
  expand = 3
  formula = G4_GLASS_PLATE
  name = G4_GLASS_PLATE
  specific = 4
FEATURE [App::DocumentObjectGroupPython] C_element049  label="C_element : 026"  # scripted group (container) (typed FeaturePython)
  n = 5
  ref = C_element
FEATURE [App::DocumentObjectGroupPython] H_element042  label="H_element : 021"  # scripted group (container) (typed FeaturePython)
  n = 10
  ref = H_element
FEATURE [App::DocumentObjectGroupPython] N_element019  label="N_element : 2"  # scripted group (container) (typed FeaturePython)
  n = 2
  ref = N_element
FEATURE [App::DocumentObjectGroupPython] O_element046  label="O_element : 022"  # scripted group (container) (typed FeaturePython)
  n = 3
  ref = O_element
FEATURE [App::DocumentObjectGroupPython] G4_GLUTAMINE  # scripted group (container) (typed FeaturePython)
  Dunit = g/cm3
  Dvalue = 1.46
  Group = -> [C_element049,H_element042,N_element019,O_element046]
  conduct = 2
  density = 1
  expand = 3
  formula = G4_GLUTAMINE
  name = G4_GLUTAMINE
  specific = 4
FEATURE [App::DocumentObjectGroupPython] C_element050  label="C_element : 027"  # scripted group (container) (typed FeaturePython)
  n = 3
  ref = C_element
FEATURE [App::DocumentObjectGroupPython] H_element043  label="H_element : 022"  # scripted group (container) (typed FeaturePython)
  n = 8
  ref = H_element
FEATURE [App::DocumentObjectGroupPython] O_element047  label="O_element : 023"  # scripted group (container) (typed FeaturePython)
  n = 3
  ref = O_element
FEATURE [App::DocumentObjectGroupPython] G4_GLYCEROL  # scripted group (container) (typed FeaturePython)
  Dunit = g/cm3
  Dvalue = 1.2613
  Group = -> [C_element050,H_element043,O_element047]
  conduct = 2
  density = 1
  expand = 3
  formula = G4_GLYCEROL
  name = G4_GLYCEROL
  specific = 4
FEATURE [App::DocumentObjectGroupPython] C_element051  label="C_element : 028"  # scripted group (container) (typed FeaturePython)
  n = 5
  ref = C_element
FEATURE [App::DocumentObjectGroupPython] H_element044  label="H_element : 023"  # scripted group (container) (typed FeaturePython)
  n = 5
  ref = H_element
FEATURE [App::DocumentObjectGroupPython] N_element020  label="N_element : 009"  # scripted group (container) (typed FeaturePython)
  n = 5
  ref = N_element
FEATURE [App::DocumentObjectGroupPython] O_element048  label="O_element : 024"  # scripted group (container) (typed FeaturePython)
  n = 1
  ref = O_element
FEATURE [App::DocumentObjectGroupPython] G4_GUANINE  # scripted group (container) (typed FeaturePython)
  Dunit = g/cm3
  Dvalue = 2.2
  Group = -> [C_element051,H_element044,N_element020,O_element048]
  conduct = 2
  density = 1
  expand = 3
  formula = G4_GUANINE
  name = G4_GUANINE
  specific = 4
FEATURE [App::DocumentObjectGroupPython] Ca_element012  label="Ca_element : 006"  # scripted group (container) (typed FeaturePython)
  n = 1
  ref = Ca_element
FEATURE [App::DocumentObjectGroupPython] S_element014  label="S_element : 005"  # scripted group (container) (typed FeaturePython)
  n = 1
  ref = S_element
FEATURE [App::DocumentObjectGroupPython] O_element049  label="O_element : 6"  # scripted group (container) (typed FeaturePython)
  n = 6
  ref = O_element
FEATURE [App::DocumentObjectGroupPython] H_element045  label="H_element : 024"  # scripted group (container) (typed FeaturePython)
  n = 4
  ref = H_element
FEATURE [App::DocumentObjectGroupPython] G4_GYPSUM  # scripted group (container) (typed FeaturePython)
  Dunit = g/cm3
  Dvalue = 2.32
  Group = -> [Ca_element012,S_element014,O_element049,H_element045]
  conduct = 2
  density = 1
  expand = 3
  formula = G4_GYPSUM
  name = G4_GYPSUM
  specific = 4
FEATURE [App::DocumentObjectGroupPython] C_element052  label="C_element : 7"  # scripted group (container) (typed FeaturePython)
  n = 7
  ref = C_element
FEATURE [App::DocumentObjectGroupPython] H_element046  label="H_element : 16"  # scripted group (container) (typed FeaturePython)
  n = 16
  ref = H_element
FEATURE [App::DocumentObjectGroupPython] G4_N_HEPTANE  label="G4_N-HEPTANE"  # scripted group (container) (typed FeaturePython)
  Dunit = g/cm3
  Dvalue = 0.68376
  Group = -> [C_element052,H_element046]
  conduct = 2
  density = 1
  expand = 3
  formula = G4_N-HEPTANE
  name = G4_N-HEPTANE
  specific = 4
FEATURE [App::DocumentObjectGroupPython] C_element053  label="C_element : 029"  # scripted group (container) (typed FeaturePython)
  n = 6
  ref = C_element
FEATURE [App::DocumentObjectGroupPython] H_element047  label="H_element : 14"  # scripted group (container) (typed FeaturePython)
  n = 14
  ref = H_element
FEATURE [App::DocumentObjectGroupPython] G4_N_HEXANE  label="G4_N-HEXANE"  # scripted group (container) (typed FeaturePython)
  Dunit = g/cm3
  Dvalue = 0.6603
  Group = -> [C_element053,H_element047]
  conduct = 2
  density = 1
  expand = 3
  formula = G4_N-HEXANE
  name = G4_N-HEXANE
  specific = 4
FEATURE [App::DocumentObjectGroupPython] C_element054  label="C_element : 22"  # scripted group (container) (typed FeaturePython)
  n = 22
  ref = C_element
FEATURE [App::DocumentObjectGroupPython] H_element048  label="H_element : 025"  # scripted group (container) (typed FeaturePython)
  n = 10
  ref = H_element
FEATURE [App::DocumentObjectGroupPython] N_element021  label="N_element : 010"  # scripted group (container) (typed FeaturePython)
  n = 2
  ref = N_element
FEATURE [App::DocumentObjectGroupPython] O_element050  label="O_element : 025"  # scripted group (container) (typed FeaturePython)
  n = 5
  ref = O_element
FEATURE [App::DocumentObjectGroupPython] G4_KAPTON  # scripted group (container) (typed FeaturePython)
  Dunit = g/cm3
  Dvalue = 1.42
  Group = -> [C_element054,H_element048,N_element021,O_element050]
  conduct = 2
  density = 1
  expand = 3
  formula = G4_KAPTON
  name = G4_KAPTON
  specific = 4
FEATURE [App::DocumentObjectGroupPython] La_element001  label="La_element : 1"  # scripted group (container) (typed FeaturePython)
  n = 1
  ref = La_element
FEATURE [App::DocumentObjectGroupPython] Br_element003  label="Br_element : 002"  # scripted group (container) (typed FeaturePython)
  n = 1
  ref = Br_element
FEATURE [App::DocumentObjectGroupPython] O_element051  label="O_element : 026"  # scripted group (container) (typed FeaturePython)
  n = 1
  ref = O_element
FEATURE [App::DocumentObjectGroupPython] G4_LANTHANUM_OXYBROMIDE  # scripted group (container) (typed FeaturePython)
  Dunit = g/cm3
  Dvalue = 6.28
  Group = -> [La_element001,Br_element003,O_element051]
  conduct = 2
  density = 1
  expand = 3
  formula = G4_LANTHANUM_OXYBROMIDE
  name = G4_LANTHANUM_OXYBROMIDE
  specific = 4
FEATURE [App::DocumentObjectGroupPython] La_element002  label="La_element : 2"  # scripted group (container) (typed FeaturePython)
  n = 2
  ref = La_element
FEATURE [App::DocumentObjectGroupPython] O_element052  label="O_element : 027"  # scripted group (container) (typed FeaturePython)
  n = 2
  ref = O_element
FEATURE [App::DocumentObjectGroupPython] S_element015  label="S_element : 006"  # scripted group (container) (typed FeaturePython)
  n = 1
  ref = S_element
FEATURE [App::DocumentObjectGroupPython] G4_LANTHANUM_OXYSULFIDE  # scripted group (container) (typed FeaturePython)
  Dunit = g/cm3
  Dvalue = 5.86
  Group = -> [La_element002,O_element052,S_element015]
  conduct = 2
  density = 1
  expand = 3
  formula = G4_LANTHANUM_OXYSULFIDE
  name = G4_LANTHANUM_OXYSULFIDE
  specific = 4
FEATURE [App::DocumentObjectGroupPython] O_element053  label="O_element : 0.072"  # scripted group (container) (typed FeaturePython)
  n = 0.071682
FEATURE [App::DocumentObjectGroupPython] Pb_element002  label="Pb_element : 0.928"  # scripted group (container) (typed FeaturePython)
  n = 0.928318
FEATURE [App::DocumentObjectGroupPython] G4_LEAD_OXIDE  # scripted group (container) (typed FeaturePython)
  Dunit = g/cm3
  Dvalue = 9.53
  Group = -> [O_element053,Pb_element002]
  conduct = 2
  density = 1
  expand = 3
  formula = G4_LEAD_OXIDE
  name = G4_LEAD_OXIDE
  specific = 4
FEATURE [App::DocumentObjectGroupPython] Li_element001  label="Li_element : 1"  # scripted group (container) (typed FeaturePython)
  n = 1
  ref = Li_element
FEATURE [App::DocumentObjectGroupPython] N_element022  label="N_element : 011"  # scripted group (container) (typed FeaturePython)
  n = 1
  ref = N_element
FEATURE [App::DocumentObjectGroupPython] H_element049  label="H_element : 026"  # scripted group (container) (typed FeaturePython)
  n = 2
  ref = H_element
FEATURE [App::DocumentObjectGroupPython] G4_LITHIUM_AMIDE  # scripted group (container) (typed FeaturePython)
  Dunit = g/cm3
  Dvalue = 1.178
  Group = -> [Li_element001,N_element022,H_element049]
  conduct = 2
  density = 1
  expand = 3
  formula = G4_LITHIUM_AMIDE
  name = G4_LITHIUM_AMIDE
  specific = 4
FEATURE [App::DocumentObjectGroupPython] Li_element002  label="Li_element : 2"  # scripted group (container) (typed FeaturePython)
  n = 2
  ref = Li_element
FEATURE [App::DocumentObjectGroupPython] C_element055  label="C_element : 030"  # scripted group (container) (typed FeaturePython)
  n = 1
  ref = C_element
FEATURE [App::DocumentObjectGroupPython] O_element054  label="O_element : 028"  # scripted group (container) (typed FeaturePython)
  n = 3
  ref = O_element
FEATURE [App::DocumentObjectGroupPython] G4_LITHIUM_CARBONATE  # scripted group (container) (typed FeaturePython)
  Dunit = g/cm3
  Dvalue = 2.11
  Group = -> [Li_element002,C_element055,O_element054]
  conduct = 2
  density = 1
  expand = 3
  formula = G4_LITHIUM_CARBONATE
  name = G4_LITHIUM_CARBONATE
  specific = 4
FEATURE [App::DocumentObjectGroupPython] Li_element003  label="Li_element : 003"  # scripted group (container) (typed FeaturePython)
  n = 1
  ref = Li_element
FEATURE [App::DocumentObjectGroupPython] F_element012  label="F_element : 004"  # scripted group (container) (typed FeaturePython)
  n = 1
  ref = F_element
FEATURE [App::DocumentObjectGroupPython] G4_LITHIUM_FLUORIDE  # scripted group (container) (typed FeaturePython)
  Dunit = g/cm3
  Dvalue = 2.635
  Group = -> [Li_element003,F_element012]
  conduct = 2
  density = 1
  expand = 3
  formula = G4_LITHIUM_FLUORIDE
  name = G4_LITHIUM_FLUORIDE
  specific = 4
FEATURE [App::DocumentObjectGroupPython] Li_element004  label="Li_element : 004"  # scripted group (container) (typed FeaturePython)
  n = 1
  ref = Li_element
FEATURE [App::DocumentObjectGroupPython] H_element050  label="H_element : 027"  # scripted group (container) (typed FeaturePython)
  n = 1
  ref = H_element
FEATURE [App::DocumentObjectGroupPython] G4_LITHIUM_HYDRIDE  # scripted group (container) (typed FeaturePython)
  Dunit = g/cm3
  Dvalue = 0.82
  Group = -> [Li_element004,H_element050]
  conduct = 2
  density = 1
  expand = 3
  formula = G4_LITHIUM_HYDRIDE
  name = G4_LITHIUM_HYDRIDE
  specific = 4
FEATURE [App::DocumentObjectGroupPython] Li_element005  label="Li_element : 005"  # scripted group (container) (typed FeaturePython)
  n = 1
  ref = Li_element
FEATURE [App::DocumentObjectGroupPython] I_element003  label="I_element : 002"  # scripted group (container) (typed FeaturePython)
  n = 1
  ref = I_element
FEATURE [App::DocumentObjectGroupPython] G4_LITHIUM_IODIDE  # scripted group (container) (typed FeaturePython)
  Dunit = g/cm3
  Dvalue = 3.494
  Group = -> [Li_element005,I_element003]
  conduct = 2
  density = 1
  expand = 3
  formula = G4_LITHIUM_IODIDE
  name = G4_LITHIUM_IODIDE
  specific = 4
FEATURE [App::DocumentObjectGroupPython] Li_element006  label="Li_element : 006"  # scripted group (container) (typed FeaturePython)
  n = 2
  ref = Li_element
FEATURE [App::DocumentObjectGroupPython] O_element055  label="O_element : 029"  # scripted group (container) (typed FeaturePython)
  n = 1
  ref = O_element
FEATURE [App::DocumentObjectGroupPython] G4_LITHIUM_OXIDE  # scripted group (container) (typed FeaturePython)
  Dunit = g/cm3
  Dvalue = 2.013
  Group = -> [Li_element006,O_element055]
  conduct = 2
  density = 1
  expand = 3
  formula = G4_LITHIUM_OXIDE
  name = G4_LITHIUM_OXIDE
  specific = 4
FEATURE [App::DocumentObjectGroupPython] Li_element007  label="Li_element : 007"  # scripted group (container) (typed FeaturePython)
  n = 2
  ref = Li_element
FEATURE [App::DocumentObjectGroupPython] B_element005  label="B_element : 005"  # scripted group (container) (typed FeaturePython)
  n = 4
  ref = B_element
FEATURE [App::DocumentObjectGroupPython] O_element056  label="O_element : 7"  # scripted group (container) (typed FeaturePython)
  n = 7
  ref = O_element
FEATURE [App::DocumentObjectGroupPython] G4_LITHIUM_TETRABORATE  # scripted group (container) (typed FeaturePython)
  Dunit = g/cm3
  Dvalue = 2.44
  Group = -> [Li_element007,B_element005,O_element056]
  conduct = 2
  density = 1
  expand = 3
  formula = G4_LITHIUM_TETRABORATE
  name = G4_LITHIUM_TETRABORATE
  specific = 4
FEATURE [App::DocumentObjectGroupPython] H_element051  label="H_element : 0.105"  # scripted group (container) (typed FeaturePython)
  n = 0.105
FEATURE [App::DocumentObjectGroupPython] C_element056  label="C_element : 0.083"  # scripted group (container) (typed FeaturePython)
  n = 0.083
FEATURE [App::DocumentObjectGroupPython] N_element023  label="N_element : 0.023"  # scripted group (container) (typed FeaturePython)
  n = 0.023
FEATURE [App::DocumentObjectGroupPython] O_element057  label="O_element : 0.779"  # scripted group (container) (typed FeaturePython)
  n = 0.779
FEATURE [App::DocumentObjectGroupPython] Na_element010  label="Na_element : 0.097"  # scripted group (container) (typed FeaturePython)
  n = 0.002
FEATURE [App::DocumentObjectGroupPython] P_element006  label="P_element : 0.105"  # scripted group (container) (typed FeaturePython)
  n = 0.001
FEATURE [App::DocumentObjectGroupPython] S_element016  label="S_element : 0.017"  # scripted group (container) (typed FeaturePython)
  n = 0.002
FEATURE [App::DocumentObjectGroupPython] Cl_element014  label="Cl_element : 0.587"  # scripted group (container) (typed FeaturePython)
  n = 0.003
FEATURE [App::DocumentObjectGroupPython] K_element005  label="K_element : 0.015"  # scripted group (container) (typed FeaturePython)
  n = 0.002
FEATURE [App::DocumentObjectGroupPython] G4_LUNG_ICRP  # scripted group (container) (typed FeaturePython)
  Dunit = g/cm3
  Dvalue = 1.04
  Group = -> [H_element051,C_element056,N_element023,O_element057,Na_element010,P_element006,S_element016,Cl_element014,K_element005]
  conduct = 2
  density = 1
  expand = 3
  formula = G4_LUNG_ICRP
  name = G4_LUNG_ICRP
  specific = 4
FEATURE [App::DocumentObjectGroupPython] H_element052  label="H_element : 0.116"  # scripted group (container) (typed FeaturePython)
  n = 0.114318
FEATURE [App::DocumentObjectGroupPython] C_element057  label="C_element : 0.656"  # scripted group (container) (typed FeaturePython)
  n = 0.655824
FEATURE [App::DocumentObjectGroupPython] O_element058  label="O_element : 0.092"  # scripted group (container) (typed FeaturePython)
  n = 0.0921831
FEATURE [App::DocumentObjectGroupPython] Mg_element004  label="Mg_element : 0.135"  # scripted group (container) (typed FeaturePython)
  n = 0.134792
FEATURE [App::DocumentObjectGroupPython] Ca_element013  label="Ca_element : 0.003"  # scripted group (container) (typed FeaturePython)
  n = 0.002883
FEATURE [App::DocumentObjectGroupPython] G4_M3_WAX  # scripted group (container) (typed FeaturePython)
  Dunit = g/cm3
  Dvalue = 1.05
  Group = -> [H_element052,C_element057,O_element058,Mg_element004,Ca_element013]
  conduct = 2
  density = 1
  expand = 3
  formula = G4_M3_WAX
  name = G4_M3_WAX
  specific = 4
FEATURE [App::DocumentObjectGroupPython] Mg_element005  label="Mg_element : 1"  # scripted group (container) (typed FeaturePython)
  n = 1
  ref = Mg_element
FEATURE [App::DocumentObjectGroupPython] C_element058  label="C_element : 031"  # scripted group (container) (typed FeaturePython)
  n = 1
  ref = C_element
FEATURE [App::DocumentObjectGroupPython] O_element059  label="O_element : 030"  # scripted group (container) (typed FeaturePython)
  n = 3
  ref = O_element
FEATURE [App::DocumentObjectGroupPython] G4_MAGNESIUM_CARBONATE  # scripted group (container) (typed FeaturePython)
  Dunit = g/cm3
  Dvalue = 2.958
  Group = -> [Mg_element005,C_element058,O_element059]
  conduct = 2
  density = 1
  expand = 3
  formula = G4_MAGNESIUM_CARBONATE
  name = G4_MAGNESIUM_CARBONATE
  specific = 4
FEATURE [App::DocumentObjectGroupPython] Mg_element006  label="Mg_element : 002"  # scripted group (container) (typed FeaturePython)
  n = 1
  ref = Mg_element
FEATURE [App::DocumentObjectGroupPython] F_element013  label="F_element : 005"  # scripted group (container) (typed FeaturePython)
  n = 2
  ref = F_element
FEATURE [App::DocumentObjectGroupPython] G4_MAGNESIUM_FLUORIDE  # scripted group (container) (typed FeaturePython)
  Dunit = g/cm3
  Dvalue = 3
  Group = -> [Mg_element006,F_element013]
  conduct = 2
  density = 1
  expand = 3
  formula = G4_MAGNESIUM_FLUORIDE
  name = G4_MAGNESIUM_FLUORIDE
  specific = 4
FEATURE [App::DocumentObjectGroupPython] Mg_element007  label="Mg_element : 003"  # scripted group (container) (typed FeaturePython)
  n = 1
  ref = Mg_element
FEATURE [App::DocumentObjectGroupPython] O_element060  label="O_element : 031"  # scripted group (container) (typed FeaturePython)
  n = 1
  ref = O_element
FEATURE [App::DocumentObjectGroupPython] G4_MAGNESIUM_OXIDE  # scripted group (container) (typed FeaturePython)
  Dunit = g/cm3
  Dvalue = 3.58
  Group = -> [Mg_element007,O_element060]
  conduct = 2
  density = 1
  expand = 3
  formula = G4_MAGNESIUM_OXIDE
  name = G4_MAGNESIUM_OXIDE
  specific = 4
FEATURE [App::DocumentObjectGroupPython] Mg_element008  label="Mg_element : 004"  # scripted group (container) (typed FeaturePython)
  n = 1
  ref = Mg_element
FEATURE [App::DocumentObjectGroupPython] B_element006  label="B_element : 006"  # scripted group (container) (typed FeaturePython)
  n = 4
  ref = B_element
FEATURE [App::DocumentObjectGroupPython] O_element061  label="O_element : 032"  # scripted group (container) (typed FeaturePython)
  n = 7
  ref = O_element
FEATURE [App::DocumentObjectGroupPython] G4_MAGNESIUM_TETRABORATE  # scripted group (container) (typed FeaturePython)
  Dunit = g/cm3
  Dvalue = 2.53
  Group = -> [Mg_element008,B_element006,O_element061]
  conduct = 2
  density = 1
  expand = 3
  formula = G4_MAGNESIUM_TETRABORATE
  name = G4_MAGNESIUM_TETRABORATE
  specific = 4
FEATURE [App::DocumentObjectGroupPython] Hg_element001  label="Hg_element : 1"  # scripted group (container) (typed FeaturePython)
  n = 1
  ref = Hg_element
FEATURE [App::DocumentObjectGroupPython] I_element004  label="I_element : 2"  # scripted group (container) (typed FeaturePython)
  n = 2
  ref = I_element
FEATURE [App::DocumentObjectGroupPython] G4_MERCURIC_IODIDE  # scripted group (container) (typed FeaturePython)
  Dunit = g/cm3
  Dvalue = 6.36
  Group = -> [Hg_element001,I_element004]
  conduct = 2
  density = 1
  expand = 3
  formula = G4_MERCURIC_IODIDE
  name = G4_MERCURIC_IODIDE
  specific = 4
FEATURE [App::DocumentObjectGroupPython] C_element059  label="C_element : 032"  # scripted group (container) (typed FeaturePython)
  n = 1
  ref = C_element
FEATURE [App::DocumentObjectGroupPython] H_element053  label="H_element : 028"  # scripted group (container) (typed FeaturePython)
  n = 4
  ref = H_element
FEATURE [App::DocumentObjectGroupPython] G4_METHANE  # scripted group (container) (typed FeaturePython)
  Dunit = g/cm3
  Dvalue = 0.000667151
  Group = -> [C_element059,H_element053]
  conduct = 2
  density = 1
  expand = 3
  formula = G4_METHANE
  name = G4_METHANE
  specific = 4
FEATURE [App::DocumentObjectGroupPython] C_element060  label="C_element : 033"  # scripted group (container) (typed FeaturePython)
  n = 1
  ref = C_element
FEATURE [App::DocumentObjectGroupPython] H_element054  label="H_element : 029"  # scripted group (container) (typed FeaturePython)
  n = 4
  ref = H_element
FEATURE [App::DocumentObjectGroupPython] O_element062  label="O_element : 033"  # scripted group (container) (typed FeaturePython)
  n = 1
  ref = O_element
FEATURE [App::DocumentObjectGroupPython] G4_METHANOL  # scripted group (container) (typed FeaturePython)
  Dunit = g/cm3
  Dvalue = 0.7914
  Group = -> [C_element060,H_element054,O_element062]
  conduct = 2
  density = 1
  expand = 3
  formula = G4_METHANOL
  name = G4_METHANOL
  specific = 4
FEATURE [App::DocumentObjectGroupPython] H_element055  label="H_element : 0.134"  # scripted group (container) (typed FeaturePython)
  n = 0.13404
FEATURE [App::DocumentObjectGroupPython] C_element061  label="C_element : 0.778"  # scripted group (container) (typed FeaturePython)
  n = 0.77796
FEATURE [App::DocumentObjectGroupPython] O_element063  label="O_element : 0.035"  # scripted group (container) (typed FeaturePython)
  n = 0.03502
FEATURE [App::DocumentObjectGroupPython] Mg_element009  label="Mg_element : 0.039"  # scripted group (container) (typed FeaturePython)
  n = 0.038594
FEATURE [App::DocumentObjectGroupPython] Ti_element002  label="Ti_element : 0.014"  # scripted group (container) (typed FeaturePython)
  n = 0.014386
FEATURE [App::DocumentObjectGroupPython] G4_MIX_D_WAX  # scripted group (container) (typed FeaturePython)
  Dunit = g/cm3
  Dvalue = 0.99
  Group = -> [H_element055,C_element061,O_element063,Mg_element009,Ti_element002]
  conduct = 2
  density = 1
  expand = 3
  formula = G4_MIX_D_WAX
  name = G4_MIX_D_WAX
  specific = 4
FEATURE [App::DocumentObjectGroupPython] H_element056  label="H_element : 0.135"  # scripted group (container) (typed FeaturePython)
  n = 0.081192
FEATURE [App::DocumentObjectGroupPython] C_element062  label="C_element : 0.583"  # scripted group (container) (typed FeaturePython)
  n = 0.583442
FEATURE [App::DocumentObjectGroupPython] N_element024  label="N_element : 0.018"  # scripted group (container) (typed FeaturePython)
  n = 0.017798
FEATURE [App::DocumentObjectGroupPython] O_element064  label="O_element : 0.186"  # scripted group (container) (typed FeaturePython)
  n = 0.186381
FEATURE [App::DocumentObjectGroupPython] Mg_element010  label="Mg_element : 0.130"  # scripted group (container) (typed FeaturePython)
  n = 0.130287
FEATURE [App::DocumentObjectGroupPython] Cl_element015  label="Cl_element : 0.588"  # scripted group (container) (typed FeaturePython)
  n = 0.0009
FEATURE [App::DocumentObjectGroupPython] G4_MS20_TISSUE  # scripted group (container) (typed FeaturePython)
  Dunit = g/cm3
  Dvalue = 1
  Group = -> [H_element056,C_element062,N_element024,O_element064,Mg_element010,Cl_element015]
  conduct = 2
  density = 1
  expand = 3
  formula = G4_MS20_TISSUE
  name = G4_MS20_TISSUE
  specific = 4
FEATURE [App::DocumentObjectGroupPython] H_element057  label="H_element : 0.136"  # scripted group (container) (typed FeaturePython)
  n = 0.102
FEATURE [App::DocumentObjectGroupPython] C_element063  label="C_element : 0.143"  # scripted group (container) (typed FeaturePython)
  n = 0.143
FEATURE [App::DocumentObjectGroupPython] N_element025  label="N_element : 0.034"  # scripted group (container) (typed FeaturePython)
  n = 0.034
FEATURE [App::DocumentObjectGroupPython] O_element065  label="O_element : 0.710"  # scripted group (container) (typed FeaturePython)
  n = 0.71
FEATURE [App::DocumentObjectGroupPython] Na_element011  label="Na_element : 0.098"  # scripted group (container) (typed FeaturePython)
  n = 0.001
FEATURE [App::DocumentObjectGroupPython] P_element007  label="P_element : 0.002"  # scripted group (container) (typed FeaturePython)
  n = 0.002
FEATURE [App::DocumentObjectGroupPython] S_element017  label="S_element : 0.018"  # scripted group (container) (typed FeaturePython)
  n = 0.003
FEATURE [App::DocumentObjectGroupPython] Cl_element016  label="Cl_element : 0.589"  # scripted group (container) (typed FeaturePython)
  n = 0.001
FEATURE [App::DocumentObjectGroupPython] K_element006  label="K_element : 0.004"  # scripted group (container) (typed FeaturePython)
  n = 0.004
FEATURE [App::DocumentObjectGroupPython] G4_MUSCLE_SKELETAL_ICRP  # scripted group (container) (typed FeaturePython)
  Dunit = g/cm3
  Dvalue = 1.05
  Group = -> [H_element057,C_element063,N_element025,O_element065,Na_element011,P_element007,S_element017,Cl_element016,K_element006]
  conduct = 2
  density = 1
  expand = 3
  formula = G4_MUSCLE_SKELETAL_ICRP
  name = G4_MUSCLE_SKELETAL_ICRP
  specific = 4
FEATURE [App::DocumentObjectGroupPython] H_element058  label="H_element : 0.137"  # scripted group (container) (typed FeaturePython)
  n = 0.102102
FEATURE [App::DocumentObjectGroupPython] C_element064  label="C_element : 0.123"  # scripted group (container) (typed FeaturePython)
  n = 0.123123
FEATURE [App::DocumentObjectGroupPython] N_element026  label="N_element : 0.756"  # scripted group (container) (typed FeaturePython)
  n = 0.035035
FEATURE [App::DocumentObjectGroupPython] O_element066  label="O_element : 0.730"  # scripted group (container) (typed FeaturePython)
  n = 0.72973
FEATURE [App::DocumentObjectGroupPython] Na_element012  label="Na_element : 0.099"  # scripted group (container) (typed FeaturePython)
  n = 0.001001
FEATURE [App::DocumentObjectGroupPython] P_element008  label="P_element : 0.106"  # scripted group (container) (typed FeaturePython)
  n = 0.002002
FEATURE [App::DocumentObjectGroupPython] S_element018  label="S_element : 0.019"  # scripted group (container) (typed FeaturePython)
  n = 0.004004
FEATURE [App::DocumentObjectGroupPython] K_element007  label="K_element : 0.016"  # scripted group (container) (typed FeaturePython)
  n = 0.003003
FEATURE [App::DocumentObjectGroupPython] G4_MUSCLE_STRIATED_ICRU  # scripted group (container) (typed FeaturePython)
  Dunit = g/cm3
  Dvalue = 1.04
  Group = -> [H_element058,C_element064,N_element026,O_element066,Na_element012,P_element008,S_element018,K_element007]
  conduct = 2
  density = 1
  expand = 3
  formula = G4_MUSCLE_STRIATED_ICRU
  name = G4_MUSCLE_STRIATED_ICRU
  specific = 4
FEATURE [App::DocumentObjectGroupPython] H_element059  label="H_element : 0.098"  # scripted group (container) (typed FeaturePython)
  n = 0.0982341
FEATURE [App::DocumentObjectGroupPython] C_element065  label="C_element : 0.156"  # scripted group (container) (typed FeaturePython)
  n = 0.156214
FEATURE [App::DocumentObjectGroupPython] N_element027  label="N_element : 0.757"  # scripted group (container) (typed FeaturePython)
  n = 0.035451
FEATURE [App::DocumentObjectGroupPython] O_element067  label="O_element : 0.880"  # scripted group (container) (typed FeaturePython)
  n = 0.710101
FEATURE [App::DocumentObjectGroupPython] G4_MUSCLE_WITH_SUCROSE  # scripted group (container) (typed FeaturePython)
  Dunit = g/cm3
  Dvalue = 1.11
  Group = -> [H_element059,C_element065,N_element027,O_element067]
  conduct = 2
  density = 1
  expand = 3
  formula = G4_MUSCLE_WITH_SUCROSE
  name = G4_MUSCLE_WITH_SUCROSE
  specific = 4
FEATURE [App::DocumentObjectGroupPython] H_element060  label="H_element : 0.138"  # scripted group (container) (typed FeaturePython)
  n = 0.101969
FEATURE [App::DocumentObjectGroupPython] C_element066  label="C_element : 0.120"  # scripted group (container) (typed FeaturePython)
  n = 0.120058
FEATURE [App::DocumentObjectGroupPython] N_element028  label="N_element : 0.758"  # scripted group (container) (typed FeaturePython)
  n = 0.035451
FEATURE [App::DocumentObjectGroupPython] O_element068  label="O_element : 0.743"  # scripted group (container) (typed FeaturePython)
  n = 0.742522
FEATURE [App::DocumentObjectGroupPython] G4_MUSCLE_WITHOUT_SUCROSE  # scripted group (container) (typed FeaturePython)
  Dunit = g/cm3
  Dvalue = 1.07
  Group = -> [H_element060,C_element066,N_element028,O_element068]
  conduct = 2
  density = 1
  expand = 3
  formula = G4_MUSCLE_WITHOUT_SUCROSE
  name = G4_MUSCLE_WITHOUT_SUCROSE
  specific = 4
FEATURE [App::DocumentObjectGroupPython] C_element067  label="C_element : 10"  # scripted group (container) (typed FeaturePython)
  n = 10
  ref = C_element
FEATURE [App::DocumentObjectGroupPython] H_element061  label="H_element : 030"  # scripted group (container) (typed FeaturePython)
  n = 8
  ref = H_element
FEATURE [App::DocumentObjectGroupPython] G4_NAPHTHALENE  # scripted group (container) (typed FeaturePython)
  Dunit = g/cm3
  Dvalue = 1.145
  Group = -> [C_element067,H_element061]
  conduct = 2
  density = 1
  expand = 3
  formula = G4_NAPHTHALENE
  name = G4_NAPHTHALENE
  specific = 4
FEATURE [App::DocumentObjectGroupPython] C_element068  label="C_element : 034"  # scripted group (container) (typed FeaturePython)
  n = 6
  ref = C_element
FEATURE [App::DocumentObjectGroupPython] H_element062  label="H_element : 031"  # scripted group (container) (typed FeaturePython)
  n = 5
  ref = H_element
FEATURE [App::DocumentObjectGroupPython] N_element029  label="N_element : 012"  # scripted group (container) (typed FeaturePython)
  n = 1
  ref = N_element
FEATURE [App::DocumentObjectGroupPython] O_element069  label="O_element : 034"  # scripted group (container) (typed FeaturePython)
  n = 2
  ref = O_element
FEATURE [App::DocumentObjectGroupPython] G4_NITROBENZENE  # scripted group (container) (typed FeaturePython)
  Dunit = g/cm3
  Dvalue = 1.19867
  Group = -> [C_element068,H_element062,N_element029,O_element069]
  conduct = 2
  density = 1
  expand = 3
  formula = G4_NITROBENZENE
  name = G4_NITROBENZENE
  specific = 4
FEATURE [App::DocumentObjectGroupPython] N_element030  label="N_element : 013"  # scripted group (container) (typed FeaturePython)
  n = 2
  ref = N_element
FEATURE [App::DocumentObjectGroupPython] O_element070  label="O_element : 035"  # scripted group (container) (typed FeaturePython)
  n = 1
  ref = O_element
FEATURE [App::DocumentObjectGroupPython] G4_NITROUS_OXIDE  # scripted group (container) (typed FeaturePython)
  Dunit = g/cm3
  Dvalue = 0.00183094
  Group = -> [N_element030,O_element070]
  conduct = 2
  density = 1
  expand = 3
  formula = G4_NITROUS_OXIDE
  name = G4_NITROUS_OXIDE
  specific = 4
FEATURE [App::DocumentObjectGroupPython] H_element063  label="H_element : 0.104"  # scripted group (container) (typed FeaturePython)
  n = 0.103509
FEATURE [App::DocumentObjectGroupPython] C_element069  label="C_element : 0.648"  # scripted group (container) (typed FeaturePython)
  n = 0.648416
FEATURE [App::DocumentObjectGroupPython] N_element031  label="N_element : 0.100"  # scripted group (container) (typed FeaturePython)
  n = 0.0995361
FEATURE [App::DocumentObjectGroupPython] O_element071  label="O_element : 0.149"  # scripted group (container) (typed FeaturePython)
  n = 0.148539
FEATURE [App::DocumentObjectGroupPython] G4_NYLON_8062  label="G4_NYLON-8062"  # scripted group (container) (typed FeaturePython)
  Dunit = g/cm3
  Dvalue = 1.08
  Group = -> [H_element063,C_element069,N_element031,O_element071]
  conduct = 2
  density = 1
  expand = 3
  formula = G4_NYLON-8062
  name = G4_NYLON-8062
  specific = 4
FEATURE [App::DocumentObjectGroupPython] C_element070  label="C_element : 035"  # scripted group (container) (typed FeaturePython)
  n = 6
  ref = C_element
FEATURE [App::DocumentObjectGroupPython] H_element064  label="H_element : 11"  # scripted group (container) (typed FeaturePython)
  n = 11
  ref = H_element
FEATURE [App::DocumentObjectGroupPython] N_element032  label="N_element : 014"  # scripted group (container) (typed FeaturePython)
  n = 1
  ref = N_element
FEATURE [App::DocumentObjectGroupPython] O_element072  label="O_element : 036"  # scripted group (container) (typed FeaturePython)
  n = 1
  ref = O_element
FEATURE [App::DocumentObjectGroupPython] G4_NYLON_6_6  label="G4_NYLON-6-6"  # scripted group (container) (typed FeaturePython)
  Dunit = g/cm3
  Dvalue = 1.14
  Group = -> [C_element070,H_element064,N_element032,O_element072]
  conduct = 2
  density = 1
  expand = 3
  formula = G4_NYLON-6-6
  name = G4_NYLON-6-6
  specific = 4
FEATURE [App::DocumentObjectGroupPython] H_element065  label="H_element : 0.139"  # scripted group (container) (typed FeaturePython)
  n = 0.107062
FEATURE [App::DocumentObjectGroupPython] C_element071  label="C_element : 0.680"  # scripted group (container) (typed FeaturePython)
  n = 0.680449
FEATURE [App::DocumentObjectGroupPython] N_element033  label="N_element : 0.099"  # scripted group (container) (typed FeaturePython)
  n = 0.099189
FEATURE [App::DocumentObjectGroupPython] O_element073  label="O_element : 0.113"  # scripted group (container) (typed FeaturePython)
  n = 0.1133
FEATURE [App::DocumentObjectGroupPython] G4_NYLON_6_10  label="G4_NYLON-6-10"  # scripted group (container) (typed FeaturePython)
  Dunit = g/cm3
  Dvalue = 1.14
  Group = -> [H_element065,C_element071,N_element033,O_element073]
  conduct = 2
  density = 1
  expand = 3
  formula = G4_NYLON-6-10
  name = G4_NYLON-6-10
  specific = 4
FEATURE [App::DocumentObjectGroupPython] H_element066  label="H_element : 0.140"  # scripted group (container) (typed FeaturePython)
  n = 0.115476
FEATURE [App::DocumentObjectGroupPython] C_element072  label="C_element : 0.721"  # scripted group (container) (typed FeaturePython)
  n = 0.720818
FEATURE [App::DocumentObjectGroupPython] N_element034  label="N_element : 0.076"  # scripted group (container) (typed FeaturePython)
  n = 0.0764169
FEATURE [App::DocumentObjectGroupPython] O_element074  label="O_element : 0.087"  # scripted group (container) (typed FeaturePython)
  n = 0.0872889
FEATURE [App::DocumentObjectGroupPython] G4_NYLON_11_RILSAN  label="G4_NYLON-11_RILSAN"  # scripted group (container) (typed FeaturePython)
  Dunit = g/cm3
  Dvalue = 1.425
  Group = -> [H_element066,C_element072,N_element034,O_element074]
  conduct = 2
  density = 1
  expand = 3
  formula = G4_NYLON-11_RILSAN
  name = G4_NYLON-11_RILSAN
  specific = 4
FEATURE [App::DocumentObjectGroupPython] C_element073  label="C_element : 8"  # scripted group (container) (typed FeaturePython)
  n = 8
  ref = C_element
FEATURE [App::DocumentObjectGroupPython] H_element067  label="H_element : 18"  # scripted group (container) (typed FeaturePython)
  n = 18
  ref = H_element
FEATURE [App::DocumentObjectGroupPython] G4_OCTANE  # scripted group (container) (typed FeaturePython)
  Dunit = g/cm3
  Dvalue = 0.7026
  Group = -> [C_element073,H_element067]
  conduct = 2
  density = 1
  expand = 3
  formula = G4_OCTANE
  name = G4_OCTANE
  specific = 4
FEATURE [App::DocumentObjectGroupPython] C_element074  label="C_element : 25"  # scripted group (container) (typed FeaturePython)
  n = 25
  ref = C_element
FEATURE [App::DocumentObjectGroupPython] H_element068  label="H_element : 52"  # scripted group (container) (typed FeaturePython)
  n = 52
  ref = H_element
FEATURE [App::DocumentObjectGroupPython] G4_PARAFFIN  # scripted group (container) (typed FeaturePython)
  Dunit = g/cm3
  Dvalue = 0.93
  Group = -> [C_element074,H_element068]
  conduct = 2
  density = 1
  expand = 3
  formula = G4_PARAFFIN
  name = G4_PARAFFIN
  specific = 4
FEATURE [App::DocumentObjectGroupPython] C_element075  label="C_element : 036"  # scripted group (container) (typed FeaturePython)
  n = 5
  ref = C_element
FEATURE [App::DocumentObjectGroupPython] H_element069  label="H_element : 032"  # scripted group (container) (typed FeaturePython)
  n = 12
  ref = H_element
FEATURE [App::DocumentObjectGroupPython] G4_N_PENTANE  label="G4_N-PENTANE"  # scripted group (container) (typed FeaturePython)
  Dunit = g/cm3
  Dvalue = 0.6262
  Group = -> [C_element075,H_element069]
  conduct = 2
  density = 1
  expand = 3
  formula = G4_N-PENTANE
  name = G4_N-PENTANE
  specific = 4
FEATURE [App::DocumentObjectGroupPython] H_element070  label="H_element : 0.014"  # scripted group (container) (typed FeaturePython)
  n = 0.0141
FEATURE [App::DocumentObjectGroupPython] C_element076  label="C_element : 0.072"  # scripted group (container) (typed FeaturePython)
  n = 0.072261
FEATURE [App::DocumentObjectGroupPython] N_element035  label="N_element : 0.019"  # scripted group (container) (typed FeaturePython)
  n = 0.01932
FEATURE [App::DocumentObjectGroupPython] O_element075  label="O_element : 0.066"  # scripted group (container) (typed FeaturePython)
  n = 0.066101
FEATURE [App::DocumentObjectGroupPython] S_element019  label="S_element : 0.020"  # scripted group (container) (typed FeaturePython)
  n = 0.00189
FEATURE [App::DocumentObjectGroupPython] Br_element004  label="Br_element : 0.349"  # scripted group (container) (typed FeaturePython)
  n = 0.349103
FEATURE [App::DocumentObjectGroupPython] Ag_element001  label="Ag_element : 0.474"  # scripted group (container) (typed FeaturePython)
  n = 0.474105
FEATURE [App::DocumentObjectGroupPython] I_element005  label="I_element : 0.003"  # scripted group (container) (typed FeaturePython)
  n = 0.00312
FEATURE [App::DocumentObjectGroupPython] G4_PHOTO_EMULSION  # scripted group (container) (typed FeaturePython)
  Dunit = g/cm3
  Dvalue = 3.815
  Group = -> [H_element070,C_element076,N_element035,O_element075,S_element019,Br_element004,Ag_element001,I_element005]
  conduct = 2
  density = 1
  expand = 3
  formula = G4_PHOTO_EMULSION
  name = G4_PHOTO_EMULSION
  specific = 4
FEATURE [App::DocumentObjectGroupPython] C_element077  label="C_element : 9"  # scripted group (container) (typed FeaturePython)
  n = 9
  ref = C_element
FEATURE [App::DocumentObjectGroupPython] H_element071  label="H_element : 033"  # scripted group (container) (typed FeaturePython)
  n = 10
  ref = H_element
FEATURE [App::DocumentObjectGroupPython] G4_PLASTIC_SC_VINYLTOLUENE  # scripted group (container) (typed FeaturePython)
  Dunit = g/cm3
  Dvalue = 1.032
  Group = -> [C_element077,H_element071]
  conduct = 2
  density = 1
  expand = 3
  formula = G4_PLASTIC_SC_VINYLTOLUENE
  name = G4_PLASTIC_SC_VINYLTOLUENE
  specific = 4
FEATURE [App::DocumentObjectGroupPython] Pu_element001  label="Pu_element : 1"  # scripted group (container) (typed FeaturePython)
  n = 1
  ref = Pu_element
FEATURE [App::DocumentObjectGroupPython] O_element076  label="O_element : 037"  # scripted group (container) (typed FeaturePython)
  n = 2
  ref = O_element
FEATURE [App::DocumentObjectGroupPython] G4_PLUTONIUM_DIOXIDE  # scripted group (container) (typed FeaturePython)
  Dunit = g/cm3
  Dvalue = 11.46
  Group = -> [Pu_element001,O_element076]
  conduct = 2
  density = 1
  expand = 3
  formula = G4_PLUTONIUM_DIOXIDE
  name = G4_PLUTONIUM_DIOXIDE
  specific = 4
FEATURE [App::DocumentObjectGroupPython] C_element078  label="C_element : 037"  # scripted group (container) (typed FeaturePython)
  n = 3
  ref = C_element
FEATURE [App::DocumentObjectGroupPython] H_element072  label="H_element : 034"  # scripted group (container) (typed FeaturePython)
  n = 3
  ref = H_element
FEATURE [App::DocumentObjectGroupPython] N_element036  label="N_element : 015"  # scripted group (container) (typed FeaturePython)
  n = 1
  ref = N_element
FEATURE [App::DocumentObjectGroupPython] G4_POLYACRYLONITRILE  # scripted group (container) (typed FeaturePython)
  Dunit = g/cm3
  Dvalue = 1.17
  Group = -> [C_element078,H_element072,N_element036]
  conduct = 2
  density = 1
  expand = 3
  formula = G4_POLYACRYLONITRILE
  name = G4_POLYACRYLONITRILE
  specific = 4
FEATURE [App::DocumentObjectGroupPython] C_element079  label="C_element : 16"  # scripted group (container) (typed FeaturePython)
  n = 16
  ref = C_element
FEATURE [App::DocumentObjectGroupPython] H_element073  label="H_element : 035"  # scripted group (container) (typed FeaturePython)
  n = 14
  ref = H_element
FEATURE [App::DocumentObjectGroupPython] O_element077  label="O_element : 038"  # scripted group (container) (typed FeaturePython)
  n = 3
  ref = O_element
FEATURE [App::DocumentObjectGroupPython] G4_POLYCARBONATE  # scripted group (container) (typed FeaturePython)
  Dunit = g/cm3
  Dvalue = 1.2
  Group = -> [C_element079,H_element073,O_element077]
  conduct = 2
  density = 1
  expand = 3
  formula = G4_POLYCARBONATE
  name = G4_POLYCARBONATE
  specific = 4
FEATURE [App::DocumentObjectGroupPython] C_element080  label="C_element : 038"  # scripted group (container) (typed FeaturePython)
  n = 8
  ref = C_element
FEATURE [App::DocumentObjectGroupPython] H_element074  label="H_element : 036"  # scripted group (container) (typed FeaturePython)
  n = 7
  ref = H_element
FEATURE [App::DocumentObjectGroupPython] Cl_element017  label="Cl_element : 007"  # scripted group (container) (typed FeaturePython)
  n = 1
  ref = Cl_element
FEATURE [App::DocumentObjectGroupPython] G4_POLYCHLOROSTYRENE  # scripted group (container) (typed FeaturePython)
  Dunit = g/cm3
  Dvalue = 1.3
  Group = -> [C_element080,H_element074,Cl_element017]
  conduct = 2
  density = 1
  expand = 3
  formula = G4_POLYCHLOROSTYRENE
  name = G4_POLYCHLOROSTYRENE
  specific = 4
FEATURE [App::DocumentObjectGroupPython] C_element081  label="C_element : 039"  # scripted group (container) (typed FeaturePython)
  n = 1
  ref = C_element
FEATURE [App::DocumentObjectGroupPython] H_element075  label="H_element : 037"  # scripted group (container) (typed FeaturePython)
  n = 2
  ref = H_element
FEATURE [App::DocumentObjectGroupPython] G4_POLYETHYLENE  # scripted group (container) (typed FeaturePython)
  Dunit = g/cm3
  Dvalue = 0.94
  Group = -> [C_element081,H_element075]
  conduct = 2
  density = 1
  expand = 3
  formula = G4_POLYETHYLENE
  name = G4_POLYETHYLENE
  specific = 4
FEATURE [App::DocumentObjectGroupPython] C_element082  label="C_element : 040"  # scripted group (container) (typed FeaturePython)
  n = 10
  ref = C_element
FEATURE [App::DocumentObjectGroupPython] H_element076  label="H_element : 038"  # scripted group (container) (typed FeaturePython)
  n = 8
  ref = H_element
FEATURE [App::DocumentObjectGroupPython] O_element078  label="O_element : 039"  # scripted group (container) (typed FeaturePython)
  n = 4
  ref = O_element
FEATURE [App::DocumentObjectGroupPython] G4_MYLAR  # scripted group (container) (typed FeaturePython)
  Dunit = g/cm3
  Dvalue = 1.4
  Group = -> [C_element082,H_element076,O_element078]
  conduct = 2
  density = 1
  expand = 3
  formula = G4_MYLAR
  name = G4_MYLAR
  specific = 4
FEATURE [App::DocumentObjectGroupPython] C_element083  label="C_element : 041"  # scripted group (container) (typed FeaturePython)
  n = 5
  ref = C_element
FEATURE [App::DocumentObjectGroupPython] H_element077  label="H_element : 039"  # scripted group (container) (typed FeaturePython)
  n = 8
  ref = H_element
FEATURE [App::DocumentObjectGroupPython] O_element079  label="O_element : 040"  # scripted group (container) (typed FeaturePython)
  n = 2
  ref = O_element
FEATURE [App::DocumentObjectGroupPython] G4_PLEXIGLASS  # scripted group (container) (typed FeaturePython)
  Dunit = g/cm3
  Dvalue = 1.19
  Group = -> [C_element083,H_element077,O_element079]
  conduct = 2
  density = 1
  expand = 3
  formula = G4_PLEXIGLASS
  name = G4_PLEXIGLASS
  specific = 4
FEATURE [App::DocumentObjectGroupPython] C_element084  label="C_element : 042"  # scripted group (container) (typed FeaturePython)
  n = 1
  ref = C_element
FEATURE [App::DocumentObjectGroupPython] H_element078  label="H_element : 040"  # scripted group (container) (typed FeaturePython)
  n = 2
  ref = H_element
FEATURE [App::DocumentObjectGroupPython] O_element080  label="O_element : 041"  # scripted group (container) (typed FeaturePython)
  n = 1
  ref = O_element
FEATURE [App::DocumentObjectGroupPython] G4_POLYOXYMETHYLENE  # scripted group (container) (typed FeaturePython)
  Dunit = g/cm3
  Dvalue = 1.425
  Group = -> [C_element084,H_element078,O_element080]
  conduct = 2
  density = 1
  expand = 3
  formula = G4_POLYOXYMETHYLENE
  name = G4_POLYOXYMETHYLENE
  specific = 4
FEATURE [App::DocumentObjectGroupPython] C_element085  label="C_element : 043"  # scripted group (container) (typed FeaturePython)
  n = 2
  ref = C_element
FEATURE [App::DocumentObjectGroupPython] H_element079  label="H_element : 041"  # scripted group (container) (typed FeaturePython)
  n = 4
  ref = H_element
FEATURE [App::DocumentObjectGroupPython] G4_POLYPROPYLENE  # scripted group (container) (typed FeaturePython)
  Dunit = g/cm3
  Dvalue = 0.9
  Group = -> [C_element085,H_element079]
  conduct = 2
  density = 1
  expand = 3
  formula = G4_POLYPROPYLENE
  name = G4_POLYPROPYLENE
  specific = 4
FEATURE [App::DocumentObjectGroupPython] C_element086  label="C_element : 044"  # scripted group (container) (typed FeaturePython)
  n = 8
  ref = C_element
FEATURE [App::DocumentObjectGroupPython] H_element080  label="H_element : 042"  # scripted group (container) (typed FeaturePython)
  n = 8
  ref = H_element
FEATURE [App::DocumentObjectGroupPython] G4_POLYSTYRENE  # scripted group (container) (typed FeaturePython)
  Dunit = g/cm3
  Dvalue = 1.06
  Group = -> [C_element086,H_element080]
  conduct = 2
  density = 1
  expand = 3
  formula = G4_POLYSTYRENE
  name = G4_POLYSTYRENE
  specific = 4
FEATURE [App::DocumentObjectGroupPython] C_element087  label="C_element : 045"  # scripted group (container) (typed FeaturePython)
  n = 2
  ref = C_element
FEATURE [App::DocumentObjectGroupPython] F_element014  label="F_element : 4"  # scripted group (container) (typed FeaturePython)
  n = 4
  ref = F_element
FEATURE [App::DocumentObjectGroupPython] G4_TEFLON  # scripted group (container) (typed FeaturePython)
  Dunit = g/cm3
  Dvalue = 2.2
  Group = -> [C_element087,F_element014]
  conduct = 2
  density = 1
  expand = 3
  formula = G4_TEFLON
  name = G4_TEFLON
  specific = 4
FEATURE [App::DocumentObjectGroupPython] C_element088  label="C_element : 046"  # scripted group (container) (typed FeaturePython)
  n = 2
  ref = C_element
FEATURE [App::DocumentObjectGroupPython] F_element015  label="F_element : 006"  # scripted group (container) (typed FeaturePython)
  n = 3
  ref = F_element
FEATURE [App::DocumentObjectGroupPython] Cl_element018  label="Cl_element : 008"  # scripted group (container) (typed FeaturePython)
  n = 1
  ref = Cl_element
FEATURE [App::DocumentObjectGroupPython] G4_POLYTRIFLUOROCHLOROETHYLENE  # scripted group (container) (typed FeaturePython)
  Dunit = g/cm3
  Dvalue = 2.1
  Group = -> [C_element088,F_element015,Cl_element018]
  conduct = 2
  density = 1
  expand = 3
  formula = G4_POLYTRIFLUOROCHLOROETHYLENE
  name = G4_POLYTRIFLUOROCHLOROETHYLENE
  specific = 4
FEATURE [App::DocumentObjectGroupPython] C_element089  label="C_element : 047"  # scripted group (container) (typed FeaturePython)
  n = 4
  ref = C_element
FEATURE [App::DocumentObjectGroupPython] H_element081  label="H_element : 043"  # scripted group (container) (typed FeaturePython)
  n = 6
  ref = H_element
FEATURE [App::DocumentObjectGroupPython] O_element081  label="O_element : 042"  # scripted group (container) (typed FeaturePython)
  n = 2
  ref = O_element
FEATURE [App::DocumentObjectGroupPython] G4_POLYVINYL_ACETATE  # scripted group (container) (typed FeaturePython)
  Dunit = g/cm3
  Dvalue = 1.19
  Group = -> [C_element089,H_element081,O_element081]
  conduct = 2
  density = 1
  expand = 3
  formula = G4_POLYVINYL_ACETATE
  name = G4_POLYVINYL_ACETATE
  specific = 4
FEATURE [App::DocumentObjectGroupPython] C_element090  label="C_element : 048"  # scripted group (container) (typed FeaturePython)
  n = 2
  ref = C_element
FEATURE [App::DocumentObjectGroupPython] H_element082  label="H_element : 044"  # scripted group (container) (typed FeaturePython)
  n = 4
  ref = H_element
FEATURE [App::DocumentObjectGroupPython] O_element082  label="O_element : 043"  # scripted group (container) (typed FeaturePython)
  n = 1
  ref = O_element
FEATURE [App::DocumentObjectGroupPython] G4_POLYVINYL_ALCOHOL  # scripted group (container) (typed FeaturePython)
  Dunit = g/cm3
  Dvalue = 1.3
  Group = -> [C_element090,H_element082,O_element082]
  conduct = 2
  density = 1
  expand = 3
  formula = G4_POLYVINYL_ALCOHOL
  name = G4_POLYVINYL_ALCOHOL
  specific = 4
FEATURE [App::DocumentObjectGroupPython] C_element091  label="C_element : 049"  # scripted group (container) (typed FeaturePython)
  n = 8
  ref = C_element
FEATURE [App::DocumentObjectGroupPython] H_element083  label="H_element : 045"  # scripted group (container) (typed FeaturePython)
  n = 14
  ref = H_element
FEATURE [App::DocumentObjectGroupPython] O_element083  label="O_element : 044"  # scripted group (container) (typed FeaturePython)
  n = 2
  ref = O_element
FEATURE [App::DocumentObjectGroupPython] G4_POLYVINYL_BUTYRAL  # scripted group (container) (typed FeaturePython)
  Dunit = g/cm3
  Dvalue = 1.12
  Group = -> [C_element091,H_element083,O_element083]
  conduct = 2
  density = 1
  expand = 3
  formula = G4_POLYVINYL_BUTYRAL
  name = G4_POLYVINYL_BUTYRAL
  specific = 4
FEATURE [App::DocumentObjectGroupPython] C_element092  label="C_element : 050"  # scripted group (container) (typed FeaturePython)
  n = 2
  ref = C_element
FEATURE [App::DocumentObjectGroupPython] H_element084  label="H_element : 046"  # scripted group (container) (typed FeaturePython)
  n = 3
  ref = H_element
FEATURE [App::DocumentObjectGroupPython] Cl_element019  label="Cl_element : 009"  # scripted group (container) (typed FeaturePython)
  n = 1
  ref = Cl_element
FEATURE [App::DocumentObjectGroupPython] G4_POLYVINYL_CHLORIDE  # scripted group (container) (typed FeaturePython)
  Dunit = g/cm3
  Dvalue = 1.3
  Group = -> [C_element092,H_element084,Cl_element019]
  conduct = 2
  density = 1
  expand = 3
  formula = G4_POLYVINYL_CHLORIDE
  name = G4_POLYVINYL_CHLORIDE
  specific = 4
FEATURE [App::DocumentObjectGroupPython] C_element093  label="C_element : 051"  # scripted group (container) (typed FeaturePython)
  n = 2
  ref = C_element
FEATURE [App::DocumentObjectGroupPython] H_element085  label="H_element : 047"  # scripted group (container) (typed FeaturePython)
  n = 2
  ref = H_element
FEATURE [App::DocumentObjectGroupPython] Cl_element020  label="Cl_element : 010"  # scripted group (container) (typed FeaturePython)
  n = 2
  ref = Cl_element
FEATURE [App::DocumentObjectGroupPython] G4_POLYVINYLIDENE_CHLORIDE  # scripted group (container) (typed FeaturePython)
  Dunit = g/cm3
  Dvalue = 1.7
  Group = -> [C_element093,H_element085,Cl_element020]
  conduct = 2
  density = 1
  expand = 3
  formula = G4_POLYVINYLIDENE_CHLORIDE
  name = G4_POLYVINYLIDENE_CHLORIDE
  specific = 4
FEATURE [App::DocumentObjectGroupPython] C_element094  label="C_element : 052"  # scripted group (container) (typed FeaturePython)
  n = 2
  ref = C_element
FEATURE [App::DocumentObjectGroupPython] H_element086  label="H_element : 048"  # scripted group (container) (typed FeaturePython)
  n = 2
  ref = H_element
FEATURE [App::DocumentObjectGroupPython] F_element016  label="F_element : 007"  # scripted group (container) (typed FeaturePython)
  n = 2
  ref = F_element
FEATURE [App::DocumentObjectGroupPython] G4_POLYVINYLIDENE_FLUORIDE  # scripted group (container) (typed FeaturePython)
  Dunit = g/cm3
  Dvalue = 1.76
  Group = -> [C_element094,H_element086,F_element016]
  conduct = 2
  density = 1
  expand = 3
  formula = G4_POLYVINYLIDENE_FLUORIDE
  name = G4_POLYVINYLIDENE_FLUORIDE
  specific = 4
FEATURE [App::DocumentObjectGroupPython] C_element095  label="C_element : 053"  # scripted group (container) (typed FeaturePython)
  n = 6
  ref = C_element
FEATURE [App::DocumentObjectGroupPython] H_element087  label="H_element : 9"  # scripted group (container) (typed FeaturePython)
  n = 9
  ref = H_element
FEATURE [App::DocumentObjectGroupPython] N_element037  label="N_element : 016"  # scripted group (container) (typed FeaturePython)
  n = 1
  ref = N_element
FEATURE [App::DocumentObjectGroupPython] O_element084  label="O_element : 045"  # scripted group (container) (typed FeaturePython)
  n = 1
  ref = O_element
FEATURE [App::DocumentObjectGroupPython] G4_POLYVINYL_PYRROLIDONE  # scripted group (container) (typed FeaturePython)
  Dunit = g/cm3
  Dvalue = 1.25
  Group = -> [C_element095,H_element087,N_element037,O_element084]
  conduct = 2
  density = 1
  expand = 3
  formula = G4_POLYVINYL_PYRROLIDONE
  name = G4_POLYVINYL_PYRROLIDONE
  specific = 4
FEATURE [App::DocumentObjectGroupPython] K_element008  label="K_element : 1"  # scripted group (container) (typed FeaturePython)
  n = 1
  ref = K_element
FEATURE [App::DocumentObjectGroupPython] I_element006  label="I_element : 003"  # scripted group (container) (typed FeaturePython)
  n = 1
  ref = I_element
FEATURE [App::DocumentObjectGroupPython] G4_POTASSIUM_IODIDE  # scripted group (container) (typed FeaturePython)
  Dunit = g/cm3
  Dvalue = 3.13
  Group = -> [K_element008,I_element006]
  conduct = 2
  density = 1
  expand = 3
  formula = G4_POTASSIUM_IODIDE
  name = G4_POTASSIUM_IODIDE
  specific = 4
FEATURE [App::DocumentObjectGroupPython] K_element009  label="K_element : 2"  # scripted group (container) (typed FeaturePython)
  n = 2
  ref = K_element
FEATURE [App::DocumentObjectGroupPython] O_element085  label="O_element : 046"  # scripted group (container) (typed FeaturePython)
  n = 1
  ref = O_element
FEATURE [App::DocumentObjectGroupPython] G4_POTASSIUM_OXIDE  # scripted group (container) (typed FeaturePython)
  Dunit = g/cm3
  Dvalue = 2.32
  Group = -> [K_element009,O_element085]
  conduct = 2
  density = 1
  expand = 3
  formula = G4_POTASSIUM_OXIDE
  name = G4_POTASSIUM_OXIDE
  specific = 4
FEATURE [App::DocumentObjectGroupPython] C_element096  label="C_element : 054"  # scripted group (container) (typed FeaturePython)
  n = 3
  ref = C_element
FEATURE [App::DocumentObjectGroupPython] H_element088  label="H_element : 049"  # scripted group (container) (typed FeaturePython)
  n = 8
  ref = H_element
FEATURE [App::DocumentObjectGroupPython] G4_PROPANE  # scripted group (container) (typed FeaturePython)
  Dunit = g/cm3
  Dvalue = 0.00187939
  Group = -> [C_element096,H_element088]
  conduct = 2
  density = 1
  expand = 3
  formula = G4_PROPANE
  name = G4_PROPANE
  specific = 4
FEATURE [App::DocumentObjectGroupPython] C_element097  label="C_element : 055"  # scripted group (container) (typed FeaturePython)
  n = 3
  ref = C_element
FEATURE [App::DocumentObjectGroupPython] H_element089  label="H_element : 050"  # scripted group (container) (typed FeaturePython)
  n = 8
  ref = H_element
FEATURE [App::DocumentObjectGroupPython] G4_lPROPANE  # scripted group (container) (typed FeaturePython)
  Dunit = g/cm3
  Dvalue = 0.43
  Group = -> [C_element097,H_element089]
  conduct = 2
  density = 1
  expand = 3
  formula = G4_lPROPANE
  name = G4_lPROPANE
  specific = 4
FEATURE [App::DocumentObjectGroupPython] C_element098  label="C_element : 056"  # scripted group (container) (typed FeaturePython)
  n = 3
  ref = C_element
FEATURE [App::DocumentObjectGroupPython] H_element090  label="H_element : 051"  # scripted group (container) (typed FeaturePython)
  n = 8
  ref = H_element
FEATURE [App::DocumentObjectGroupPython] O_element086  label="O_element : 047"  # scripted group (container) (typed FeaturePython)
  n = 1
  ref = O_element
FEATURE [App::DocumentObjectGroupPython] G4_N_PROPYL_ALCOHOL  label="G4_N-PROPYL_ALCOHOL"  # scripted group (container) (typed FeaturePython)
  Dunit = g/cm3
  Dvalue = 0.8035
  Group = -> [C_element098,H_element090,O_element086]
  conduct = 2
  density = 1
  expand = 3
  formula = G4_N-PROPYL_ALCOHOL
  name = G4_N-PROPYL_ALCOHOL
  specific = 4
FEATURE [App::DocumentObjectGroupPython] C_element099  label="C_element : 057"  # scripted group (container) (typed FeaturePython)
  n = 5
  ref = C_element
FEATURE [App::DocumentObjectGroupPython] H_element091  label="H_element : 052"  # scripted group (container) (typed FeaturePython)
  n = 5
  ref = H_element
FEATURE [App::DocumentObjectGroupPython] N_element038  label="N_element : 017"  # scripted group (container) (typed FeaturePython)
  n = 1
  ref = N_element
FEATURE [App::DocumentObjectGroupPython] G4_PYRIDINE  # scripted group (container) (typed FeaturePython)
  Dunit = g/cm3
  Dvalue = 0.9819
  Group = -> [C_element099,H_element091,N_element038]
  conduct = 2
  density = 1
  expand = 3
  formula = G4_PYRIDINE
  name = G4_PYRIDINE
  specific = 4
FEATURE [App::DocumentObjectGroupPython] H_element092  label="H_element : 0.144"  # scripted group (container) (typed FeaturePython)
  n = 0.143711
FEATURE [App::DocumentObjectGroupPython] C_element100  label="C_element : 0.856"  # scripted group (container) (typed FeaturePython)
  n = 0.856289
FEATURE [App::DocumentObjectGroupPython] G4_RUBBER_BUTYL  # scripted group (container) (typed FeaturePython)
  Dunit = g/cm3
  Dvalue = 0.92
  Group = -> [H_element092,C_element100]
  conduct = 2
  density = 1
  expand = 3
  formula = G4_RUBBER_BUTYL
  name = G4_RUBBER_BUTYL
  specific = 4
FEATURE [App::DocumentObjectGroupPython] H_element093  label="H_element : 0.118"  # scripted group (container) (typed FeaturePython)
  n = 0.118371
FEATURE [App::DocumentObjectGroupPython] C_element101  label="C_element : 0.882"  # scripted group (container) (typed FeaturePython)
  n = 0.881629
FEATURE [App::DocumentObjectGroupPython] G4_RUBBER_NATURAL  # scripted group (container) (typed FeaturePython)
  Dunit = g/cm3
  Dvalue = 0.92
  Group = -> [H_element093,C_element101]
  conduct = 2
  density = 1
  expand = 3
  formula = G4_RUBBER_NATURAL
  name = G4_RUBBER_NATURAL
  specific = 4
FEATURE [App::DocumentObjectGroupPython] H_element094  label="H_element : 0.145"  # scripted group (container) (typed FeaturePython)
  n = 0.05692
FEATURE [App::DocumentObjectGroupPython] C_element102  label="C_element : 0.543"  # scripted group (container) (typed FeaturePython)
  n = 0.542646
FEATURE [App::DocumentObjectGroupPython] Cl_element021  label="Cl_element : 0.400"  # scripted group (container) (typed FeaturePython)
  n = 0.400434
FEATURE [App::DocumentObjectGroupPython] G4_RUBBER_NEOPRENE  # scripted group (container) (typed FeaturePython)
  Dunit = g/cm3
  Dvalue = 1.23
  Group = -> [H_element094,C_element102,Cl_element021]
  conduct = 2
  density = 1
  expand = 3
  formula = G4_RUBBER_NEOPRENE
  name = G4_RUBBER_NEOPRENE
  specific = 4
FEATURE [App::DocumentObjectGroupPython] Si_element006  label="Si_element : 1"  # scripted group (container) (typed FeaturePython)
  n = 1
  ref = Si_element
FEATURE [App::DocumentObjectGroupPython] O_element087  label="O_element : 048"  # scripted group (container) (typed FeaturePython)
  n = 2
  ref = O_element
FEATURE [App::DocumentObjectGroupPython] G4_SILICON_DIOXIDE  # scripted group (container) (typed FeaturePython)
  Dunit = g/cm3
  Dvalue = 2.32
  Group = -> [Si_element006,O_element087]
  conduct = 2
  density = 1
  expand = 3
  formula = G4_SILICON_DIOXIDE
  name = G4_SILICON_DIOXIDE
  specific = 4
FEATURE [App::DocumentObjectGroupPython] Ag_element002  label="Ag_element : 1"  # scripted group (container) (typed FeaturePython)
  n = 1
  ref = Ag_element
FEATURE [App::DocumentObjectGroupPython] Br_element005  label="Br_element : 003"  # scripted group (container) (typed FeaturePython)
  n = 1
  ref = Br_element
FEATURE [App::DocumentObjectGroupPython] G4_SILVER_BROMIDE  # scripted group (container) (typed FeaturePython)
  Dunit = g/cm3
  Dvalue = 6.473
  Group = -> [Ag_element002,Br_element005]
  conduct = 2
  density = 1
  expand = 3
  formula = G4_SILVER_BROMIDE
  name = G4_SILVER_BROMIDE
  specific = 4
FEATURE [App::DocumentObjectGroupPython] Ag_element003  label="Ag_element : 002"  # scripted group (container) (typed FeaturePython)
  n = 1
  ref = Ag_element
FEATURE [App::DocumentObjectGroupPython] Cl_element022  label="Cl_element : 011"  # scripted group (container) (typed FeaturePython)
  n = 1
  ref = Cl_element
FEATURE [App::DocumentObjectGroupPython] G4_SILVER_CHLORIDE  # scripted group (container) (typed FeaturePython)
  Dunit = g/cm3
  Dvalue = 5.56
  Group = -> [Ag_element003,Cl_element022]
  conduct = 2
  density = 1
  expand = 3
  formula = G4_SILVER_CHLORIDE
  name = G4_SILVER_CHLORIDE
  specific = 4
FEATURE [App::DocumentObjectGroupPython] Br_element006  label="Br_element : 0.423"  # scripted group (container) (typed FeaturePython)
  n = 0.422895
FEATURE [App::DocumentObjectGroupPython] Ag_element004  label="Ag_element : 0.574"  # scripted group (container) (typed FeaturePython)
  n = 0.573748
FEATURE [App::DocumentObjectGroupPython] I_element007  label="I_element : 0.649"  # scripted group (container) (typed FeaturePython)
  n = 0.003357
FEATURE [App::DocumentObjectGroupPython] G4_SILVER_HALIDES  # scripted group (container) (typed FeaturePython)
  Dunit = g/cm3
  Dvalue = 6.47
  Group = -> [Br_element006,Ag_element004,I_element007]
  conduct = 2
  density = 1
  expand = 3
  formula = G4_SILVER_HALIDES
  name = G4_SILVER_HALIDES
  specific = 4
FEATURE [App::DocumentObjectGroupPython] Ag_element005  label="Ag_element : 003"  # scripted group (container) (typed FeaturePython)
  n = 1
  ref = Ag_element
FEATURE [App::DocumentObjectGroupPython] I_element008  label="I_element : 004"  # scripted group (container) (typed FeaturePython)
  n = 1
  ref = I_element
FEATURE [App::DocumentObjectGroupPython] G4_SILVER_IODIDE  # scripted group (container) (typed FeaturePython)
  Dunit = g/cm3
  Dvalue = 6.01
  Group = -> [Ag_element005,I_element008]
  conduct = 2
  density = 1
  expand = 3
  formula = G4_SILVER_IODIDE
  name = G4_SILVER_IODIDE
  specific = 4
FEATURE [App::DocumentObjectGroupPython] H_element095  label="H_element : 0.100"  # scripted group (container) (typed FeaturePython)
  n = 0.1
FEATURE [App::DocumentObjectGroupPython] C_element103  label="C_element : 0.204"  # scripted group (container) (typed FeaturePython)
  n = 0.204
FEATURE [App::DocumentObjectGroupPython] N_element039  label="N_element : 0.759"  # scripted group (container) (typed FeaturePython)
  n = 0.042
FEATURE [App::DocumentObjectGroupPython] O_element088  label="O_element : 0.645"  # scripted group (container) (typed FeaturePython)
  n = 0.645
FEATURE [App::DocumentObjectGroupPython] Na_element013  label="Na_element : 0.100"  # scripted group (container) (typed FeaturePython)
  n = 0.002
FEATURE [App::DocumentObjectGroupPython] P_element009  label="P_element : 0.107"  # scripted group (container) (typed FeaturePython)
  n = 0.001
FEATURE [App::DocumentObjectGroupPython] S_element020  label="S_element : 0.021"  # scripted group (container) (typed FeaturePython)
  n = 0.002
FEATURE [App::DocumentObjectGroupPython] Cl_element023  label="Cl_element : 0.590"  # scripted group (container) (typed FeaturePython)
  n = 0.003
FEATURE [App::DocumentObjectGroupPython] K_element010  label="K_element : 0.001"  # scripted group (container) (typed FeaturePython)
  n = 0.001
FEATURE [App::DocumentObjectGroupPython] G4_SKIN_ICRP  # scripted group (container) (typed FeaturePython)
  Dunit = g/cm3
  Dvalue = 1.09
  Group = -> [H_element095,C_element103,N_element039,O_element088,Na_element013,P_element009,S_element020,Cl_element023,K_element010]
  conduct = 2
  density = 1
  expand = 3
  formula = G4_SKIN_ICRP
  name = G4_SKIN_ICRP
  specific = 4
FEATURE [App::DocumentObjectGroupPython] Na_element014  label="Na_element : 2"  # scripted group (container) (typed FeaturePython)
  n = 2
  ref = Na_element
FEATURE [App::DocumentObjectGroupPython] C_element104  label="C_element : 058"  # scripted group (container) (typed FeaturePython)
  n = 1
  ref = C_element
FEATURE [App::DocumentObjectGroupPython] O_element089  label="O_element : 049"  # scripted group (container) (typed FeaturePython)
  n = 3
  ref = O_element
FEATURE [App::DocumentObjectGroupPython] G4_SODIUM_CARBONATE  # scripted group (container) (typed FeaturePython)
  Dunit = g/cm3
  Dvalue = 2.532
  Group = -> [Na_element014,C_element104,O_element089]
  conduct = 2
  density = 1
  expand = 3
  formula = G4_SODIUM_CARBONATE
  name = G4_SODIUM_CARBONATE
  specific = 4
FEATURE [App::DocumentObjectGroupPython] Na_element015  label="Na_element : 1"  # scripted group (container) (typed FeaturePython)
  n = 1
  ref = Na_element
FEATURE [App::DocumentObjectGroupPython] I_element009  label="I_element : 005"  # scripted group (container) (typed FeaturePython)
  n = 1
  ref = I_element
FEATURE [App::DocumentObjectGroupPython] G4_SODIUM_IODIDE  # scripted group (container) (typed FeaturePython)
  Dunit = g/cm3
  Dvalue = 3.667
  Group = -> [Na_element015,I_element009]
  conduct = 2
  density = 1
  expand = 3
  formula = G4_SODIUM_IODIDE
  name = G4_SODIUM_IODIDE
  specific = 4
FEATURE [App::DocumentObjectGroupPython] Na_element016  label="Na_element : 003"  # scripted group (container) (typed FeaturePython)
  n = 2
  ref = Na_element
FEATURE [App::DocumentObjectGroupPython] O_element090  label="O_element : 050"  # scripted group (container) (typed FeaturePython)
  n = 1
  ref = O_element
FEATURE [App::DocumentObjectGroupPython] G4_SODIUM_MONOXIDE  # scripted group (container) (typed FeaturePython)
  Dunit = g/cm3
  Dvalue = 2.27
  Group = -> [Na_element016,O_element090]
  conduct = 2
  density = 1
  expand = 3
  formula = G4_SODIUM_MONOXIDE
  name = G4_SODIUM_MONOXIDE
  specific = 4
FEATURE [App::DocumentObjectGroupPython] Na_element017  label="Na_element : 004"  # scripted group (container) (typed FeaturePython)
  n = 1
  ref = Na_element
FEATURE [App::DocumentObjectGroupPython] N_element040  label="N_element : 018"  # scripted group (container) (typed FeaturePython)
  n = 1
  ref = N_element
FEATURE [App::DocumentObjectGroupPython] O_element091  label="O_element : 051"  # scripted group (container) (typed FeaturePython)
  n = 3
  ref = O_element
FEATURE [App::DocumentObjectGroupPython] G4_SODIUM_NITRATE  # scripted group (container) (typed FeaturePython)
  Dunit = g/cm3
  Dvalue = 2.261
  Group = -> [Na_element017,N_element040,O_element091]
  conduct = 2
  density = 1
  expand = 3
  formula = G4_SODIUM_NITRATE
  name = G4_SODIUM_NITRATE
  specific = 4
FEATURE [App::DocumentObjectGroupPython] C_element105  label="C_element : 059"  # scripted group (container) (typed FeaturePython)
  n = 14
  ref = C_element
FEATURE [App::DocumentObjectGroupPython] H_element096  label="H_element : 053"  # scripted group (container) (typed FeaturePython)
  n = 12
  ref = H_element
FEATURE [App::DocumentObjectGroupPython] G4_STILBENE  # scripted group (container) (typed FeaturePython)
  Dunit = g/cm3
  Dvalue = 0.9707
  Group = -> [C_element105,H_element096]
  conduct = 2
  density = 1
  expand = 3
  formula = G4_STILBENE
  name = G4_STILBENE
  specific = 4
FEATURE [App::DocumentObjectGroupPython] C_element106  label="C_element : 12"  # scripted group (container) (typed FeaturePython)
  n = 12
  ref = C_element
FEATURE [App::DocumentObjectGroupPython] H_element097  label="H_element : 22"  # scripted group (container) (typed FeaturePython)
  n = 22
  ref = H_element
FEATURE [App::DocumentObjectGroupPython] O_element092  label="O_element : 11"  # scripted group (container) (typed FeaturePython)
  n = 11
  ref = O_element
FEATURE [App::DocumentObjectGroupPython] G4_SUCROSE  # scripted group (container) (typed FeaturePython)
  Dunit = g/cm3
  Dvalue = 1.5805
  Group = -> [C_element106,H_element097,O_element092]
  conduct = 2
  density = 1
  expand = 3
  formula = G4_SUCROSE
  name = G4_SUCROSE
  specific = 4
FEATURE [App::DocumentObjectGroupPython] C_element107  label="C_element : 18"  # scripted group (container) (typed FeaturePython)
  n = 18
  ref = C_element
FEATURE [App::DocumentObjectGroupPython] H_element098  label="H_element : 054"  # scripted group (container) (typed FeaturePython)
  n = 14
  ref = H_element
FEATURE [App::DocumentObjectGroupPython] G4_TERPHENYL  # scripted group (container) (typed FeaturePython)
  Dunit = g/cm3
  Dvalue = 1.24
  Group = -> [C_element107,H_element098]
  conduct = 2
  density = 1
  expand = 3
  formula = G4_TERPHENYL
  name = G4_TERPHENYL
  specific = 4
FEATURE [App::DocumentObjectGroupPython] H_element099  label="H_element : 0.146"  # scripted group (container) (typed FeaturePython)
  n = 0.106
FEATURE [App::DocumentObjectGroupPython] C_element108  label="C_element : 0.883"  # scripted group (container) (typed FeaturePython)
  n = 0.099
FEATURE [App::DocumentObjectGroupPython] N_element041  label="N_element : 0.020"  # scripted group (container) (typed FeaturePython)
  n = 0.02
FEATURE [App::DocumentObjectGroupPython] O_element093  label="O_element : 0.766"  # scripted group (container) (typed FeaturePython)
  n = 0.766
FEATURE [App::DocumentObjectGroupPython] Na_element018  label="Na_element : 0.101"  # scripted group (container) (typed FeaturePython)
  n = 0.002
FEATURE [App::DocumentObjectGroupPython] P_element010  label="P_element : 0.108"  # scripted group (container) (typed FeaturePython)
  n = 0.001
FEATURE [App::DocumentObjectGroupPython] S_element021  label="S_element : 0.022"  # scripted group (container) (typed FeaturePython)
  n = 0.002
FEATURE [App::DocumentObjectGroupPython] Cl_element024  label="Cl_element : 0.002"  # scripted group (container) (typed FeaturePython)
  n = 0.002
FEATURE [App::DocumentObjectGroupPython] K_element011  label="K_element : 0.017"  # scripted group (container) (typed FeaturePython)
  n = 0.002
FEATURE [App::DocumentObjectGroupPython] G4_TESTIS_ICRP  # scripted group (container) (typed FeaturePython)
  Dunit = g/cm3
  Dvalue = 1.04
  Group = -> [H_element099,C_element108,N_element041,O_element093,Na_element018,P_element010,S_element021,Cl_element024,K_element011]
  conduct = 2
  density = 1
  expand = 3
  formula = G4_TESTIS_ICRP
  name = G4_TESTIS_ICRP
  specific = 4
FEATURE [App::DocumentObjectGroupPython] C_element109  label="C_element : 060"  # scripted group (container) (typed FeaturePython)
  n = 2
  ref = C_element
FEATURE [App::DocumentObjectGroupPython] Cl_element025  label="Cl_element : 012"  # scripted group (container) (typed FeaturePython)
  n = 4
  ref = Cl_element
FEATURE [App::DocumentObjectGroupPython] G4_TETRACHLOROETHYLENE  # scripted group (container) (typed FeaturePython)
  Dunit = g/cm3
  Dvalue = 1.625
  Group = -> [C_element109,Cl_element025]
  conduct = 2
  density = 1
  expand = 3
  formula = G4_TETRACHLOROETHYLENE
  name = G4_TETRACHLOROETHYLENE
  specific = 4
FEATURE [App::DocumentObjectGroupPython] Tl_element001  label="Tl_element : 1"  # scripted group (container) (typed FeaturePython)
  n = 1
  ref = Tl_element
FEATURE [App::DocumentObjectGroupPython] Cl_element026  label="Cl_element : 013"  # scripted group (container) (typed FeaturePython)
  n = 1
  ref = Cl_element
FEATURE [App::DocumentObjectGroupPython] G4_THALLIUM_CHLORIDE  # scripted group (container) (typed FeaturePython)
  Dunit = g/cm3
  Dvalue = 7.004
  Group = -> [Tl_element001,Cl_element026]
  conduct = 2
  density = 1
  expand = 3
  formula = G4_THALLIUM_CHLORIDE
  name = G4_THALLIUM_CHLORIDE
  specific = 4
FEATURE [App::DocumentObjectGroupPython] H_element100  label="H_element : 0.147"  # scripted group (container) (typed FeaturePython)
  n = 0.105
FEATURE [App::DocumentObjectGroupPython] C_element110  label="C_element : 0.256"  # scripted group (container) (typed FeaturePython)
  n = 0.256
FEATURE [App::DocumentObjectGroupPython] N_element042  label="N_element : 0.760"  # scripted group (container) (typed FeaturePython)
  n = 0.027
FEATURE [App::DocumentObjectGroupPython] O_element094  label="O_element : 0.602"  # scripted group (container) (typed FeaturePython)
  n = 0.602
FEATURE [App::DocumentObjectGroupPython] Na_element019  label="Na_element : 0.102"  # scripted group (container) (typed FeaturePython)
  n = 0.001
FEATURE [App::DocumentObjectGroupPython] P_element011  label="P_element : 0.109"  # scripted group (container) (typed FeaturePython)
  n = 0.002
FEATURE [App::DocumentObjectGroupPython] S_element022  label="S_element : 0.023"  # scripted group (container) (typed FeaturePython)
  n = 0.003
FEATURE [App::DocumentObjectGroupPython] Cl_element027  label="Cl_element : 0.591"  # scripted group (container) (typed FeaturePython)
  n = 0.002
FEATURE [App::DocumentObjectGroupPython] K_element012  label="K_element : 0.018"  # scripted group (container) (typed FeaturePython)
  n = 0.002
FEATURE [App::DocumentObjectGroupPython] G4_TISSUE_SOFT_ICRP  # scripted group (container) (typed FeaturePython)
  Dunit = g/cm3
  Dvalue = 1.03
  Group = -> [H_element100,C_element110,N_element042,O_element094,Na_element019,P_element011,S_element022,Cl_element027,K_element012]
  conduct = 2
  density = 1
  expand = 3
  formula = G4_TISSUE_SOFT_ICRP
  name = G4_TISSUE_SOFT_ICRP
  specific = 4
FEATURE [App::DocumentObjectGroupPython] H_element101  label="H_element : 0.148"  # scripted group (container) (typed FeaturePython)
  n = 0.101
FEATURE [App::DocumentObjectGroupPython] C_element111  label="C_element : 0.111"  # scripted group (container) (typed FeaturePython)
  n = 0.111
FEATURE [App::DocumentObjectGroupPython] N_element043  label="N_element : 0.026"  # scripted group (container) (typed FeaturePython)
  n = 0.026
FEATURE [App::DocumentObjectGroupPython] O_element095  label="O_element : 0.762"  # scripted group (container) (typed FeaturePython)
  n = 0.762
FEATURE [App::DocumentObjectGroupPython] G4_TISSUE_SOFT_ICRU_4  label="G4_TISSUE_SOFT_ICRU-4"  # scripted group (container) (typed FeaturePython)
  Dunit = g/cm3
  Dvalue = 1
  Group = -> [H_element101,C_element111,N_element043,O_element095]
  conduct = 2
  density = 1
  expand = 3
  formula = G4_TISSUE_SOFT_ICRU-4
  name = G4_TISSUE_SOFT_ICRU-4
  specific = 4
FEATURE [App::DocumentObjectGroupPython] H_element102  label="H_element : 0.149"  # scripted group (container) (typed FeaturePython)
  n = 0.101869
FEATURE [App::DocumentObjectGroupPython] C_element112  label="C_element : 0.456"  # scripted group (container) (typed FeaturePython)
  n = 0.456179
FEATURE [App::DocumentObjectGroupPython] N_element044  label="N_element : 0.761"  # scripted group (container) (typed FeaturePython)
  n = 0.035172
FEATURE [App::DocumentObjectGroupPython] O_element096  label="O_element : 0.407"  # scripted group (container) (typed FeaturePython)
  n = 0.40678
FEATURE [App::DocumentObjectGroupPython] G4_TISSUE_METHANE  label="G4_TISSUE-METHANE"  # scripted group (container) (typed FeaturePython)
  Dunit = g/cm3
  Dvalue = 0.00106409
  Group = -> [H_element102,C_element112,N_element044,O_element096]
  conduct = 2
  density = 1
  expand = 3
  formula = G4_TISSUE-METHANE
  name = G4_TISSUE-METHANE
  specific = 4
FEATURE [App::DocumentObjectGroupPython] H_element103  label="H_element : 0.103"  # scripted group (container) (typed FeaturePython)
  n = 0.102672
FEATURE [App::DocumentObjectGroupPython] C_element113  label="C_element : 0.569"  # scripted group (container) (typed FeaturePython)
  n = 0.56894
FEATURE [App::DocumentObjectGroupPython] N_element045  label="N_element : 0.762"  # scripted group (container) (typed FeaturePython)
  n = 0.035022
FEATURE [App::DocumentObjectGroupPython] O_element097  label="O_element : 0.293"  # scripted group (container) (typed FeaturePython)
  n = 0.293366
FEATURE [App::DocumentObjectGroupPython] G4_TISSUE_PROPANE  label="G4_TISSUE-PROPANE"  # scripted group (container) (typed FeaturePython)
  Dunit = g/cm3
  Dvalue = 0.00182628
  Group = -> [H_element103,C_element113,N_element045,O_element097]
  conduct = 2
  density = 1
  expand = 3
  formula = G4_TISSUE-PROPANE
  name = G4_TISSUE-PROPANE
  specific = 4
FEATURE [App::DocumentObjectGroupPython] Ti_element003  label="Ti_element : 1"  # scripted group (container) (typed FeaturePython)
  n = 1
  ref = Ti_element
FEATURE [App::DocumentObjectGroupPython] O_element098  label="O_element : 052"  # scripted group (container) (typed FeaturePython)
  n = 2
  ref = O_element
FEATURE [App::DocumentObjectGroupPython] G4_TITANIUM_DIOXIDE  # scripted group (container) (typed FeaturePython)
  Dunit = g/cm3
  Dvalue = 4.26
  Group = -> [Ti_element003,O_element098]
  conduct = 2
  density = 1
  expand = 3
  formula = G4_TITANIUM_DIOXIDE
  name = G4_TITANIUM_DIOXIDE
  specific = 4
FEATURE [App::DocumentObjectGroupPython] C_element114  label="C_element : 061"  # scripted group (container) (typed FeaturePython)
  n = 7
  ref = C_element
FEATURE [App::DocumentObjectGroupPython] H_element104  label="H_element : 055"  # scripted group (container) (typed FeaturePython)
  n = 8
  ref = H_element
FEATURE [App::DocumentObjectGroupPython] G4_TOLUENE  # scripted group (container) (typed FeaturePython)
  Dunit = g/cm3
  Dvalue = 0.8669
  Group = -> [C_element114,H_element104]
  conduct = 2
  density = 1
  expand = 3
  formula = G4_TOLUENE
  name = G4_TOLUENE
  specific = 4
FEATURE [App::DocumentObjectGroupPython] C_element115  label="C_element : 062"  # scripted group (container) (typed FeaturePython)
  n = 2
  ref = C_element
FEATURE [App::DocumentObjectGroupPython] H_element105  label="H_element : 056"  # scripted group (container) (typed FeaturePython)
  n = 1
  ref = H_element
FEATURE [App::DocumentObjectGroupPython] Cl_element028  label="Cl_element : 014"  # scripted group (container) (typed FeaturePython)
  n = 3
  ref = Cl_element
FEATURE [App::DocumentObjectGroupPython] G4_TRICHLOROETHYLENE  # scripted group (container) (typed FeaturePython)
  Dunit = g/cm3
  Dvalue = 1.46
  Group = -> [C_element115,H_element105,Cl_element028]
  conduct = 2
  density = 1
  expand = 3
  formula = G4_TRICHLOROETHYLENE
  name = G4_TRICHLOROETHYLENE
  specific = 4
FEATURE [App::DocumentObjectGroupPython] C_element116  label="C_element : 063"  # scripted group (container) (typed FeaturePython)
  n = 6
  ref = C_element
FEATURE [App::DocumentObjectGroupPython] H_element106  label="H_element : 15"  # scripted group (container) (typed FeaturePython)
  n = 15
  ref = H_element
FEATURE [App::DocumentObjectGroupPython] O_element099  label="O_element : 053"  # scripted group (container) (typed FeaturePython)
  n = 4
  ref = O_element
FEATURE [App::DocumentObjectGroupPython] P_element012  label="P_element : 1"  # scripted group (container) (typed FeaturePython)
  n = 1
  ref = P_element
FEATURE [App::DocumentObjectGroupPython] G4_TRIETHYL_PHOSPHATE  # scripted group (container) (typed FeaturePython)
  Dunit = g/cm3
  Dvalue = 1.07
  Group = -> [C_element116,H_element106,O_element099,P_element012]
  conduct = 2
  density = 1
  expand = 3
  formula = G4_TRIETHYL_PHOSPHATE
  name = G4_TRIETHYL_PHOSPHATE
  specific = 4
FEATURE [App::DocumentObjectGroupPython] W_element003  label="W_element : 003"  # scripted group (container) (typed FeaturePython)
  n = 1
  ref = W_element
FEATURE [App::DocumentObjectGroupPython] F_element017  label="F_element : 6"  # scripted group (container) (typed FeaturePython)
  n = 6
  ref = F_element
FEATURE [App::DocumentObjectGroupPython] G4_TUNGSTEN_HEXAFLUORIDE  # scripted group (container) (typed FeaturePython)
  Dunit = g/cm3
  Dvalue = 2.4
  Group = -> [W_element003,F_element017]
  conduct = 2
  density = 1
  expand = 3
  formula = G4_TUNGSTEN_HEXAFLUORIDE
  name = G4_TUNGSTEN_HEXAFLUORIDE
  specific = 4
FEATURE [App::DocumentObjectGroupPython] U_element001  label="U_element : 1"  # scripted group (container) (typed FeaturePython)
  n = 1
  ref = U_element
FEATURE [App::DocumentObjectGroupPython] C_element117  label="C_element : 064"  # scripted group (container) (typed FeaturePython)
  n = 2
  ref = C_element
FEATURE [App::DocumentObjectGroupPython] G4_URANIUM_DICARBIDE  # scripted group (container) (typed FeaturePython)
  Dunit = g/cm3
  Dvalue = 11.28
  Group = -> [U_element001,C_element117]
  conduct = 2
  density = 1
  expand = 3
  formula = G4_URANIUM_DICARBIDE
  name = G4_URANIUM_DICARBIDE
  specific = 4
FEATURE [App::DocumentObjectGroupPython] U_element002  label="U_element : 002"  # scripted group (container) (typed FeaturePython)
  n = 1
  ref = U_element
FEATURE [App::DocumentObjectGroupPython] C_element118  label="C_element : 065"  # scripted group (container) (typed FeaturePython)
  n = 1
  ref = C_element
FEATURE [App::DocumentObjectGroupPython] G4_URANIUM_MONOCARBIDE  # scripted group (container) (typed FeaturePython)
  Dunit = g/cm3
  Dvalue = 13.63
  Group = -> [U_element002,C_element118]
  conduct = 2
  density = 1
  expand = 3
  formula = G4_URANIUM_MONOCARBIDE
  name = G4_URANIUM_MONOCARBIDE
  specific = 4
FEATURE [App::DocumentObjectGroupPython] U_element003  label="U_element : 003"  # scripted group (container) (typed FeaturePython)
  n = 1
  ref = U_element
FEATURE [App::DocumentObjectGroupPython] O_element100  label="O_element : 054"  # scripted group (container) (typed FeaturePython)
  n = 2
  ref = O_element
FEATURE [App::DocumentObjectGroupPython] G4_URANIUM_OXIDE  # scripted group (container) (typed FeaturePython)
  Dunit = g/cm3
  Dvalue = 10.96
  Group = -> [U_element003,O_element100]
  conduct = 2
  density = 1
  expand = 3
  formula = G4_URANIUM_OXIDE
  name = G4_URANIUM_OXIDE
  specific = 4
FEATURE [App::DocumentObjectGroupPython] C_element119  label="C_element : 066"  # scripted group (container) (typed FeaturePython)
  n = 1
  ref = C_element
FEATURE [App::DocumentObjectGroupPython] H_element107  label="H_element : 057"  # scripted group (container) (typed FeaturePython)
  n = 4
  ref = H_element
FEATURE [App::DocumentObjectGroupPython] N_element046  label="N_element : 019"  # scripted group (container) (typed FeaturePython)
  n = 2
  ref = N_element
FEATURE [App::DocumentObjectGroupPython] O_element101  label="O_element : 055"  # scripted group (container) (typed FeaturePython)
  n = 1
  ref = O_element
FEATURE [App::DocumentObjectGroupPython] G4_UREA  # scripted group (container) (typed FeaturePython)
  Dunit = g/cm3
  Dvalue = 1.323
  Group = -> [C_element119,H_element107,N_element046,O_element101]
  conduct = 2
  density = 1
  expand = 3
  formula = G4_UREA
  name = G4_UREA
  specific = 4
FEATURE [App::DocumentObjectGroupPython] C_element120  label="C_element : 067"  # scripted group (container) (typed FeaturePython)
  n = 5
  ref = C_element
FEATURE [App::DocumentObjectGroupPython] H_element108  label="H_element : 058"  # scripted group (container) (typed FeaturePython)
  n = 11
  ref = H_element
FEATURE [App::DocumentObjectGroupPython] N_element047  label="N_element : 020"  # scripted group (container) (typed FeaturePython)
  n = 1
  ref = N_element
FEATURE [App::DocumentObjectGroupPython] O_element102  label="O_element : 056"  # scripted group (container) (typed FeaturePython)
  n = 2
  ref = O_element
FEATURE [App::DocumentObjectGroupPython] G4_VALINE  # scripted group (container) (typed FeaturePython)
  Dunit = g/cm3
  Dvalue = 1.23
  Group = -> [C_element120,H_element108,N_element047,O_element102]
  conduct = 2
  density = 1
  expand = 3
  formula = G4_VALINE
  name = G4_VALINE
  specific = 4
FEATURE [App::DocumentObjectGroupPython] H_element109  label="H_element : 0.009"  # scripted group (container) (typed FeaturePython)
  n = 0.009417
FEATURE [App::DocumentObjectGroupPython] C_element121  label="C_element : 0.281"  # scripted group (container) (typed FeaturePython)
  n = 0.280555
FEATURE [App::DocumentObjectGroupPython] F_element018  label="F_element : 0.710"  # scripted group (container) (typed FeaturePython)
  n = 0.710028
FEATURE [App::DocumentObjectGroupPython] G4_VITON  # scripted group (container) (typed FeaturePython)
  Dunit = g/cm3
  Dvalue = 1.8
  Group = -> [H_element109,C_element121,F_element018]
  conduct = 2
  density = 1
  expand = 3
  formula = G4_VITON
  name = G4_VITON
  specific = 4
FEATURE [App::DocumentObjectGroupPython] H_element110  label="H_element : 059"  # scripted group (container) (typed FeaturePython)
  n = 2
  ref = H_element
FEATURE [App::DocumentObjectGroupPython] O_element103  label="O_element : 057"  # scripted group (container) (typed FeaturePython)
  n = 1
  ref = O_element
FEATURE [App::DocumentObjectGroupPython] G4_WATER  # scripted group (container) (typed FeaturePython)
  Dunit = g/cm3
  Dvalue = 1
  Group = -> [H_element110,O_element103]
  conduct = 2
  density = 1
  expand = 3
  formula = G4_WATER
  name = G4_WATER
  specific = 4
FEATURE [App::DocumentObjectGroupPython] H_element111  label="H_element : 060"  # scripted group (container) (typed FeaturePython)
  n = 2
  ref = H_element
FEATURE [App::DocumentObjectGroupPython] O_element104  label="O_element : 058"  # scripted group (container) (typed FeaturePython)
  n = 1
  ref = O_element
FEATURE [App::DocumentObjectGroupPython] G4_WATER_VAPOR  # scripted group (container) (typed FeaturePython)
  Dunit = g/cm3
  Dvalue = 0.000756182
  Group = -> [H_element111,O_element104]
  conduct = 2
  density = 1
  expand = 3
  formula = G4_WATER_VAPOR
  name = G4_WATER_VAPOR
  specific = 4
FEATURE [App::DocumentObjectGroupPython] C_element122  label="C_element : 068"  # scripted group (container) (typed FeaturePython)
  n = 8
  ref = C_element
FEATURE [App::DocumentObjectGroupPython] H_element112  label="H_element : 061"  # scripted group (container) (typed FeaturePython)
  n = 10
  ref = H_element
FEATURE [App::DocumentObjectGroupPython] G4_XYLENE  # scripted group (container) (typed FeaturePython)
  Dunit = g/cm3
  Dvalue = 0.87
  Group = -> [C_element122,H_element112]
  conduct = 2
  density = 1
  expand = 3
  formula = G4_XYLENE
  name = G4_XYLENE
  specific = 4
FEATURE [App::DocumentObjectGroupPython] C_element123  label="C_element : 069"  # scripted group (container) (typed FeaturePython)
  n = 1
  ref = C_element
FEATURE [App::DocumentObjectGroupPython] G4_GRAPHITE  # scripted group (container) (typed FeaturePython)
  Dunit = g/cm3
  Dvalue = 2.21
  Group = -> [C_element123]
  conduct = 2
  density = 1
  expand = 3
  formula = G4_GRAPHITE
  name = G4_GRAPHITE
  specific = 4
FEATURE [App::DocumentObjectGroupPython] NIST  # scripted group (container) (typed FeaturePython)
  Group = -> [G4_A_150_TISSUE,G4_ACETONE,G4_ACETYLENE,G4_ADENINE,G4_ADIPOSE_TISSUE_ICRP,G4_AIR,G4_ALANINE,G4_ALUMINUM_OXIDE,G4_AMBER,G4_AMMONIA,G4_ANILINE,G4_ANTHRACENE,G4_B_100_BONE,G4_BAKELITE,G4_BARIUM_FLUORIDE,G4_BARIUM_SULFATE,G4_BENZENE,G4_BERYLLIUM_OXIDE,G4_BGO,G4_BLOOD_ICRP,G4_BONE_COMPACT_ICRU,G4_BONE_CORTICAL_ICRP,G4_BORON_CARBIDE,G4_BORON_OXIDE,G4_BRAIN_ICRP,G4_BUTANE,G4_N_BUTYL_ALCOHOL,G4_C_552,+152 more]
FEATURE [App::DocumentObjectGroupPython] H_element113  label="H_element : 062"  # scripted group (container) (typed FeaturePython)
  n = 1
  ref = H_element
FEATURE [App::DocumentObjectGroupPython] G4_H  # scripted group (container) (typed FeaturePython)
  Dunit = g/cm3
  Dvalue = 8.3748e-05
  Group = -> [H_element113]
  conduct = 2
  density = 1
  expand = 3
  formula = H
  name = G4_H
  specific = 4
FEATURE [App::DocumentObjectGroupPython] He_element001  label="He_element : 1"  # scripted group (container) (typed FeaturePython)
  n = 1
  ref = He_element
FEATURE [App::DocumentObjectGroupPython] G4_He  # scripted group (container) (typed FeaturePython)
  Dunit = g/cm3
  Dvalue = 0.000166322
  Group = -> [He_element001]
  conduct = 2
  density = 1
  expand = 3
  formula = He
  name = G4_He
  specific = 4
FEATURE [App::DocumentObjectGroupPython] Li_element008  label="Li_element : 008"  # scripted group (container) (typed FeaturePython)
  n = 1
  ref = Li_element
FEATURE [App::DocumentObjectGroupPython] G4_Li  # scripted group (container) (typed FeaturePython)
  Dunit = g/cm3
  Dvalue = 0.534
  Group = -> [Li_element008]
  conduct = 2
  density = 1
  expand = 3
  formula = Li
  name = G4_Li
  specific = 4
FEATURE [App::DocumentObjectGroupPython] Be_element002  label="Be_element : 002"  # scripted group (container) (typed FeaturePython)
  n = 1
  ref = Be_element
FEATURE [App::DocumentObjectGroupPython] G4_Be  # scripted group (container) (typed FeaturePython)
  Dunit = g/cm3
  Dvalue = 1.848
  Group = -> [Be_element002]
  conduct = 2
  density = 1
  expand = 3
  formula = Be
  name = G4_Be
  specific = 4
FEATURE [App::DocumentObjectGroupPython] B_element007  label="B_element : 007"  # scripted group (container) (typed FeaturePython)
  n = 1
  ref = B_element
FEATURE [App::DocumentObjectGroupPython] G4_B  # scripted group (container) (typed FeaturePython)
  Dunit = g/cm3
  Dvalue = 2.37
  Group = -> [B_element007]
  conduct = 2
  density = 1
  expand = 3
  formula = B
  name = G4_B
  specific = 4
FEATURE [App::DocumentObjectGroupPython] C_element124  label="C_element : 070"  # scripted group (container) (typed FeaturePython)
  n = 1
  ref = C_element
FEATURE [App::DocumentObjectGroupPython] G4_C  # scripted group (container) (typed FeaturePython)
  Dunit = g/cm3
  Dvalue = 2
  Group = -> [C_element124]
  conduct = 2
  density = 1
  expand = 3
  formula = C
  name = G4_C
  specific = 4
FEATURE [App::DocumentObjectGroupPython] N_element048  label="N_element : 021"  # scripted group (container) (typed FeaturePython)
  n = 1
  ref = N_element
FEATURE [App::DocumentObjectGroupPython] G4_N  # scripted group (container) (typed FeaturePython)
  Dunit = g/cm3
  Dvalue = 0.0011652
  Group = -> [N_element048]
  conduct = 2
  density = 1
  expand = 3
  formula = N
  name = G4_N
  specific = 4
FEATURE [App::DocumentObjectGroupPython] O_element105  label="O_element : 059"  # scripted group (container) (typed FeaturePython)
  n = 1
  ref = O_element
FEATURE [App::DocumentObjectGroupPython] G4_O  # scripted group (container) (typed FeaturePython)
  Dunit = g/cm3
  Dvalue = 0.00133151
  Group = -> [O_element105]
  conduct = 2
  density = 1
  expand = 3
  formula = O
  name = G4_O
  specific = 4
FEATURE [App::DocumentObjectGroupPython] F_element019  label="F_element : 008"  # scripted group (container) (typed FeaturePython)
  n = 1
  ref = F_element
FEATURE [App::DocumentObjectGroupPython] G4_F  # scripted group (container) (typed FeaturePython)
  Dunit = g/cm3
  Dvalue = 0.00158029
  Group = -> [F_element019]
  conduct = 2
  density = 1
  expand = 3
  formula = F
  name = G4_F
  specific = 4
FEATURE [App::DocumentObjectGroupPython] Ne_element001  label="Ne_element : 1"  # scripted group (container) (typed FeaturePython)
  n = 1
  ref = Ne_element
FEATURE [App::DocumentObjectGroupPython] G4_Ne  # scripted group (container) (typed FeaturePython)
  Dunit = g/cm3
  Dvalue = 0.000838505
  Group = -> [Ne_element001]
  conduct = 2
  density = 1
  expand = 3
  formula = Ne
  name = G4_Ne
  specific = 4
FEATURE [App::DocumentObjectGroupPython] Na_element020  label="Na_element : 005"  # scripted group (container) (typed FeaturePython)
  n = 1
  ref = Na_element
FEATURE [App::DocumentObjectGroupPython] G4_Na  # scripted group (container) (typed FeaturePython)
  Dunit = g/cm3
  Dvalue = 0.971
  Group = -> [Na_element020]
  conduct = 2
  density = 1
  expand = 3
  formula = Na
  name = G4_Na
  specific = 4
FEATURE [App::DocumentObjectGroupPython] Mg_element011  label="Mg_element : 005"  # scripted group (container) (typed FeaturePython)
  n = 1
  ref = Mg_element
FEATURE [App::DocumentObjectGroupPython] G4_Mg  # scripted group (container) (typed FeaturePython)
  Dunit = g/cm3
  Dvalue = 1.74
  Group = -> [Mg_element011]
  conduct = 2
  density = 1
  expand = 3
  formula = Mg
  name = G4_Mg
  specific = 4
FEATURE [App::DocumentObjectGroupPython] Al_element004  label="Al_element : 1"  # scripted group (container) (typed FeaturePython)
  n = 1
  ref = Al_element
FEATURE [App::DocumentObjectGroupPython] G4_Al  # scripted group (container) (typed FeaturePython)
  Dunit = g/cm3
  Dvalue = 2.699
  Group = -> [Al_element004]
  conduct = 2
  density = 1
  expand = 3
  formula = Al
  name = G4_Al
  specific = 4
FEATURE [App::DocumentObjectGroupPython] Si_element007  label="Si_element : 002"  # scripted group (container) (typed FeaturePython)
  n = 1
  ref = Si_element
FEATURE [App::DocumentObjectGroupPython] G4_Si  # scripted group (container) (typed FeaturePython)
  Dunit = g/cm3
  Dvalue = 2.33
  Group = -> [Si_element007]
  conduct = 2
  density = 1
  expand = 3
  formula = Si
  name = G4_Si
  specific = 4
FEATURE [App::DocumentObjectGroupPython] P_element013  label="P_element : 002"  # scripted group (container) (typed FeaturePython)
  n = 1
  ref = P_element
FEATURE [App::DocumentObjectGroupPython] G4_P  # scripted group (container) (typed FeaturePython)
  Dunit = g/cm3
  Dvalue = 2.2
  Group = -> [P_element013]
  conduct = 2
  density = 1
  expand = 3
  formula = P
  name = G4_P
  specific = 4
FEATURE [App::DocumentObjectGroupPython] S_element023  label="S_element : 007"  # scripted group (container) (typed FeaturePython)
  n = 1
  ref = S_element
FEATURE [App::DocumentObjectGroupPython] G4_S  # scripted group (container) (typed FeaturePython)
  Dunit = g/cm3
  Dvalue = 2
  Group = -> [S_element023]
  conduct = 2
  density = 1
  expand = 3
  formula = S
  name = G4_S
  specific = 4
FEATURE [App::DocumentObjectGroupPython] Cl_element029  label="Cl_element : 015"  # scripted group (container) (typed FeaturePython)
  n = 1
  ref = Cl_element
FEATURE [App::DocumentObjectGroupPython] G4_Cl  # scripted group (container) (typed FeaturePython)
  Dunit = g/cm3
  Dvalue = 0.00299473
  Group = -> [Cl_element029]
  conduct = 2
  density = 1
  expand = 3
  formula = Cl
  name = G4_Cl
  specific = 4
FEATURE [App::DocumentObjectGroupPython] Ar_element002  label="Ar_element : 1"  # scripted group (container) (typed FeaturePython)
  n = 1
  ref = Ar_element
FEATURE [App::DocumentObjectGroupPython] G4_Ar  # scripted group (container) (typed FeaturePython)
  Dunit = g/cm3
  Dvalue = 0.00166201
  Group = -> [Ar_element002]
  conduct = 2
  density = 1
  expand = 3
  formula = Ar
  name = G4_Ar
  specific = 4
FEATURE [App::DocumentObjectGroupPython] K_element013  label="K_element : 003"  # scripted group (container) (typed FeaturePython)
  n = 1
  ref = K_element
FEATURE [App::DocumentObjectGroupPython] G4_K  # scripted group (container) (typed FeaturePython)
  Dunit = g/cm3
  Dvalue = 0.862
  Group = -> [K_element013]
  conduct = 2
  density = 1
  expand = 3
  formula = K
  name = G4_K
  specific = 4
FEATURE [App::DocumentObjectGroupPython] Ca_element014  label="Ca_element : 007"  # scripted group (container) (typed FeaturePython)
  n = 1
  ref = Ca_element
FEATURE [App::DocumentObjectGroupPython] G4_Ca  # scripted group (container) (typed FeaturePython)
  Dunit = g/cm3
  Dvalue = 1.55
  Group = -> [Ca_element014]
  conduct = 2
  density = 1
  expand = 3
  formula = Ca
  name = G4_Ca
  specific = 4
FEATURE [App::DocumentObjectGroupPython] Sc_element001  label="Sc_element : 1"  # scripted group (container) (typed FeaturePython)
  n = 1
  ref = Sc_element
FEATURE [App::DocumentObjectGroupPython] G4_Sc  # scripted group (container) (typed FeaturePython)
  Dunit = g/cm3
  Dvalue = 2.989
  Group = -> [Sc_element001]
  conduct = 2
  density = 1
  expand = 3
  formula = Sc
  name = G4_Sc
  specific = 4
FEATURE [App::DocumentObjectGroupPython] Ti_element004  label="Ti_element : 002"  # scripted group (container) (typed FeaturePython)
  n = 1
  ref = Ti_element
FEATURE [App::DocumentObjectGroupPython] G4_Ti  # scripted group (container) (typed FeaturePython)
  Dunit = g/cm3
  Dvalue = 4.54
  Group = -> [Ti_element004]
  conduct = 2
  density = 1
  expand = 3
  formula = Ti
  name = G4_Ti
  specific = 4
FEATURE [App::DocumentObjectGroupPython] V_element001  label="V_element : 1"  # scripted group (container) (typed FeaturePython)
  n = 1
  ref = V_element
FEATURE [App::DocumentObjectGroupPython] G4_V  # scripted group (container) (typed FeaturePython)
  Dunit = g/cm3
  Dvalue = 6.11
  Group = -> [V_element001]
  conduct = 2
  density = 1
  expand = 3
  formula = V
  name = G4_V
  specific = 4
FEATURE [App::DocumentObjectGroupPython] Cr_element001  label="Cr_element : 1"  # scripted group (container) (typed FeaturePython)
  n = 1
  ref = Cr_element
FEATURE [App::DocumentObjectGroupPython] G4_Cr  # scripted group (container) (typed FeaturePython)
  Dunit = g/cm3
  Dvalue = 7.18
  Group = -> [Cr_element001]
  conduct = 2
  density = 1
  expand = 3
  formula = Cr
  name = G4_Cr
  specific = 4
FEATURE [App::DocumentObjectGroupPython] Mn_element001  label="Mn_element : 1"  # scripted group (container) (typed FeaturePython)
  n = 1
  ref = Mn_element
FEATURE [App::DocumentObjectGroupPython] G4_Mn  # scripted group (container) (typed FeaturePython)
  Dunit = g/cm3
  Dvalue = 7.44
  Group = -> [Mn_element001]
  conduct = 2
  density = 1
  expand = 3
  formula = Mn
  name = G4_Mn
  specific = 4
FEATURE [App::DocumentObjectGroupPython] Fe_element007  label="Fe_element : 004"  # scripted group (container) (typed FeaturePython)
  n = 1
  ref = Fe_element
FEATURE [App::DocumentObjectGroupPython] G4_Fe  # scripted group (container) (typed FeaturePython)
  Dunit = g/cm3
  Dvalue = 7.874
  Group = -> [Fe_element007]
  conduct = 2
  density = 1
  expand = 3
  formula = Fe
  name = G4_Fe
  specific = 4
FEATURE [App::DocumentObjectGroupPython] Co_element001  label="Co_element : 1"  # scripted group (container) (typed FeaturePython)
  n = 1
  ref = Co_element
FEATURE [App::DocumentObjectGroupPython] G4_Co  # scripted group (container) (typed FeaturePython)
  Dunit = g/cm3
  Dvalue = 8.9
  Group = -> [Co_element001]
  conduct = 2
  density = 1
  expand = 3
  formula = Co
  name = G4_Co
  specific = 4
FEATURE [App::DocumentObjectGroupPython] Ni_element001  label="Ni_element : 1"  # scripted group (container) (typed FeaturePython)
  n = 1
  ref = Ni_element
FEATURE [App::DocumentObjectGroupPython] G4_Ni  # scripted group (container) (typed FeaturePython)
  Dunit = g/cm3
  Dvalue = 8.902
  Group = -> [Ni_element001]
  conduct = 2
  density = 1
  expand = 3
  formula = Ni
  name = G4_Ni
  specific = 4
FEATURE [App::DocumentObjectGroupPython] Cu_element001  label="Cu_element : 1"  # scripted group (container) (typed FeaturePython)
  n = 1
  ref = Cu_element
FEATURE [App::DocumentObjectGroupPython] G4_Cu  # scripted group (container) (typed FeaturePython)
  Dunit = g/cm3
  Dvalue = 8.96
  Group = -> [Cu_element001]
  conduct = 2
  density = 1
  expand = 3
  formula = Cu
  name = G4_Cu
  specific = 4
FEATURE [App::DocumentObjectGroupPython] Zn_element001  label="Zn_element : 1"  # scripted group (container) (typed FeaturePython)
  n = 1
  ref = Zn_element
FEATURE [App::DocumentObjectGroupPython] G4_Zn  # scripted group (container) (typed FeaturePython)
  Dunit = g/cm3
  Dvalue = 7.133
  Group = -> [Zn_element001]
  conduct = 2
  density = 1
  expand = 3
  formula = Zn
  name = G4_Zn
  specific = 4
FEATURE [App::DocumentObjectGroupPython] Ga_element002  label="Ga_element : 002"  # scripted group (container) (typed FeaturePython)
  n = 1
  ref = Ga_element
FEATURE [App::DocumentObjectGroupPython] G4_Ga  # scripted group (container) (typed FeaturePython)
  Dunit = g/cm3
  Dvalue = 5.904
  Group = -> [Ga_element002]
  conduct = 2
  density = 1
  expand = 3
  formula = Ga
  name = G4_Ga
  specific = 4
FEATURE [App::DocumentObjectGroupPython] Ge_element002  label="Ge_element : 1"  # scripted group (container) (typed FeaturePython)
  n = 1
  ref = Ge_element
FEATURE [App::DocumentObjectGroupPython] G4_Ge  # scripted group (container) (typed FeaturePython)
  Dunit = g/cm3
  Dvalue = 5.323
  Group = -> [Ge_element002]
  conduct = 2
  density = 1
  expand = 3
  formula = Ge
  name = G4_Ge
  specific = 4
FEATURE [App::DocumentObjectGroupPython] As_element003  label="As_element : 002"  # scripted group (container) (typed FeaturePython)
  n = 1
  ref = As_element
FEATURE [App::DocumentObjectGroupPython] G4_As  # scripted group (container) (typed FeaturePython)
  Dunit = g/cm3
  Dvalue = 5.73
  Group = -> [As_element003]
  conduct = 2
  density = 1
  expand = 3
  formula = As
  name = G4_As
  specific = 4
FEATURE [App::DocumentObjectGroupPython] Se_element001  label="Se_element : 1"  # scripted group (container) (typed FeaturePython)
  n = 1
  ref = Se_element
FEATURE [App::DocumentObjectGroupPython] G4_Se  # scripted group (container) (typed FeaturePython)
  Dunit = g/cm3
  Dvalue = 4.5
  Group = -> [Se_element001]
  conduct = 2
  density = 1
  expand = 3
  formula = Se
  name = G4_Se
  specific = 4
FEATURE [App::DocumentObjectGroupPython] Br_element007  label="Br_element : 004"  # scripted group (container) (typed FeaturePython)
  n = 1
  ref = Br_element
FEATURE [App::DocumentObjectGroupPython] G4_Br  # scripted group (container) (typed FeaturePython)
  Dunit = g/cm3
  Dvalue = 0.0070721
  Group = -> [Br_element007]
  conduct = 2
  density = 1
  expand = 3
  formula = Br
  name = G4_Br
  specific = 4
FEATURE [App::DocumentObjectGroupPython] Kr_element001  label="Kr_element : 1"  # scripted group (container) (typed FeaturePython)
  n = 1
  ref = Kr_element
FEATURE [App::DocumentObjectGroupPython] G4_Kr  # scripted group (container) (typed FeaturePython)
  Dunit = g/cm3
  Dvalue = 0.00347832
  Group = -> [Kr_element001]
  conduct = 2
  density = 1
  expand = 3
  formula = Kr
  name = G4_Kr
  specific = 4
FEATURE [App::DocumentObjectGroupPython] Rb_element001  label="Rb_element : 1"  # scripted group (container) (typed FeaturePython)
  n = 1
  ref = Rb_element
FEATURE [App::DocumentObjectGroupPython] G4_Rb  # scripted group (container) (typed FeaturePython)
  Dunit = g/cm3
  Dvalue = 1.532
  Group = -> [Rb_element001]
  conduct = 2
  density = 1
  expand = 3
  formula = Rb
  name = G4_Rb
  specific = 4
FEATURE [App::DocumentObjectGroupPython] Sr_element001  label="Sr_element : 1"  # scripted group (container) (typed FeaturePython)
  n = 1
  ref = Sr_element
FEATURE [App::DocumentObjectGroupPython] G4_Sr  # scripted group (container) (typed FeaturePython)
  Dunit = g/cm3
  Dvalue = 2.54
  Group = -> [Sr_element001]
  conduct = 2
  density = 1
  expand = 3
  formula = Sr
  name = G4_Sr
  specific = 4
FEATURE [App::DocumentObjectGroupPython] Y_element001  label="Y_element : 1"  # scripted group (container) (typed FeaturePython)
  n = 1
  ref = Y_element
FEATURE [App::DocumentObjectGroupPython] G4_Y  # scripted group (container) (typed FeaturePython)
  Dunit = g/cm3
  Dvalue = 4.469
  Group = -> [Y_element001]
  conduct = 2
  density = 1
  expand = 3
  formula = Y
  name = G4_Y
  specific = 4
FEATURE [App::DocumentObjectGroupPython] Zr_element001  label="Zr_element : 1"  # scripted group (container) (typed FeaturePython)
  n = 1
  ref = Zr_element
FEATURE [App::DocumentObjectGroupPython] G4_Zr  # scripted group (container) (typed FeaturePython)
  Dunit = g/cm3
  Dvalue = 6.506
  Group = -> [Zr_element001]
  conduct = 2
  density = 1
  expand = 3
  formula = Zr
  name = G4_Zr
  specific = 4
FEATURE [App::DocumentObjectGroupPython] Nb_element001  label="Nb_element : 1"  # scripted group (container) (typed FeaturePython)
  n = 1
  ref = Nb_element
FEATURE [App::DocumentObjectGroupPython] G4_Nb  # scripted group (container) (typed FeaturePython)
  Dunit = g/cm3
  Dvalue = 8.57
  Group = -> [Nb_element001]
  conduct = 2
  density = 1
  expand = 3
  formula = Nb
  name = G4_Nb
  specific = 4
FEATURE [App::DocumentObjectGroupPython] Mo_element001  label="Mo_element : 1"  # scripted group (container) (typed FeaturePython)
  n = 1
  ref = Mo_element
FEATURE [App::DocumentObjectGroupPython] G4_Mo  # scripted group (container) (typed FeaturePython)
  Dunit = g/cm3
  Dvalue = 10.22
  Group = -> [Mo_element001]
  conduct = 2
  density = 1
  expand = 3
  formula = Mo
  name = G4_Mo
  specific = 4
FEATURE [App::DocumentObjectGroupPython] Tc_element001  label="Tc_element : 1"  # scripted group (container) (typed FeaturePython)
  n = 1
  ref = Tc_element
FEATURE [App::DocumentObjectGroupPython] G4_Tc  # scripted group (container) (typed FeaturePython)
  Dunit = g/cm3
  Dvalue = 11.5
  Group = -> [Tc_element001]
  conduct = 2
  density = 1
  expand = 3
  formula = Tc
  name = G4_Tc
  specific = 4
FEATURE [App::DocumentObjectGroupPython] Ru_element001  label="Ru_element : 1"  # scripted group (container) (typed FeaturePython)
  n = 1
  ref = Ru_element
FEATURE [App::DocumentObjectGroupPython] G4_Ru  # scripted group (container) (typed FeaturePython)
  Dunit = g/cm3
  Dvalue = 12.41
  Group = -> [Ru_element001]
  conduct = 2
  density = 1
  expand = 3
  formula = Ru
  name = G4_Ru
  specific = 4
FEATURE [App::DocumentObjectGroupPython] Rh_element001  label="Rh_element : 1"  # scripted group (container) (typed FeaturePython)
  n = 1
  ref = Rh_element
FEATURE [App::DocumentObjectGroupPython] G4_Rh  # scripted group (container) (typed FeaturePython)
  Dunit = g/cm3
  Dvalue = 12.41
  Group = -> [Rh_element001]
  conduct = 2
  density = 1
  expand = 3
  formula = Rh
  name = G4_Rh
  specific = 4
FEATURE [App::DocumentObjectGroupPython] Pd_element001  label="Pd_element : 1"  # scripted group (container) (typed FeaturePython)
  n = 1
  ref = Pd_element
FEATURE [App::DocumentObjectGroupPython] G4_Pd  # scripted group (container) (typed FeaturePython)
  Dunit = g/cm3
  Dvalue = 12.02
  Group = -> [Pd_element001]
  conduct = 2
  density = 1
  expand = 3
  formula = Pd
  name = G4_Pd
  specific = 4
FEATURE [App::DocumentObjectGroupPython] Ag_element006  label="Ag_element : 004"  # scripted group (container) (typed FeaturePython)
  n = 1
  ref = Ag_element
FEATURE [App::DocumentObjectGroupPython] G4_Ag  # scripted group (container) (typed FeaturePython)
  Dunit = g/cm3
  Dvalue = 10.5
  Group = -> [Ag_element006]
  conduct = 2
  density = 1
  expand = 3
  formula = Ag
  name = G4_Ag
  specific = 4
FEATURE [App::DocumentObjectGroupPython] Cd_element003  label="Cd_element : 003"  # scripted group (container) (typed FeaturePython)
  n = 1
  ref = Cd_element
FEATURE [App::DocumentObjectGroupPython] G4_Cd  # scripted group (container) (typed FeaturePython)
  Dunit = g/cm3
  Dvalue = 8.65
  Group = -> [Cd_element003]
  conduct = 2
  density = 1
  expand = 3
  formula = Cd
  name = G4_Cd
  specific = 4
FEATURE [App::DocumentObjectGroupPython] In_element001  label="In_element : 1"  # scripted group (container) (typed FeaturePython)
  n = 1
  ref = In_element
FEATURE [App::DocumentObjectGroupPython] G4_In  # scripted group (container) (typed FeaturePython)
  Dunit = g/cm3
  Dvalue = 7.31
  Group = -> [In_element001]
  conduct = 2
  density = 1
  expand = 3
  formula = In
  name = G4_In
  specific = 4
FEATURE [App::DocumentObjectGroupPython] Sn_element001  label="Sn_element : 1"  # scripted group (container) (typed FeaturePython)
  n = 1
  ref = Sn_element
FEATURE [App::DocumentObjectGroupPython] G4_Sn  # scripted group (container) (typed FeaturePython)
  Dunit = g/cm3
  Dvalue = 7.31
  Group = -> [Sn_element001]
  conduct = 2
  density = 1
  expand = 3
  formula = Sn
  name = G4_Sn
  specific = 4
FEATURE [App::DocumentObjectGroupPython] Sb_element001  label="Sb_element : 1"  # scripted group (container) (typed FeaturePython)
  n = 1
  ref = Sb_element
FEATURE [App::DocumentObjectGroupPython] G4_Sb  # scripted group (container) (typed FeaturePython)
  Dunit = g/cm3
  Dvalue = 6.691
  Group = -> [Sb_element001]
  conduct = 2
  density = 1
  expand = 3
  formula = Sb
  name = G4_Sb
  specific = 4
FEATURE [App::DocumentObjectGroupPython] Te_element002  label="Te_element : 002"  # scripted group (container) (typed FeaturePython)
  n = 1
  ref = Te_element
FEATURE [App::DocumentObjectGroupPython] G4_Te  # scripted group (container) (typed FeaturePython)
  Dunit = g/cm3
  Dvalue = 6.24
  Group = -> [Te_element002]
  conduct = 2
  density = 1
  expand = 3
  formula = Te
  name = G4_Te
  specific = 4
FEATURE [App::DocumentObjectGroupPython] I_element010  label="I_element : 006"  # scripted group (container) (typed FeaturePython)
  n = 1
  ref = I_element
FEATURE [App::DocumentObjectGroupPython] G4_I  # scripted group (container) (typed FeaturePython)
  Dunit = g/cm3
  Dvalue = 4.93
  Group = -> [I_element010]
  conduct = 2
  density = 1
  expand = 3
  formula = I
  name = G4_I
  specific = 4
FEATURE [App::DocumentObjectGroupPython] Xe_element001  label="Xe_element : 1"  # scripted group (container) (typed FeaturePython)
  n = 1
  ref = Xe_element
FEATURE [App::DocumentObjectGroupPython] G4_Xe  # scripted group (container) (typed FeaturePython)
  Dunit = g/cm3
  Dvalue = 0.00548536
  Group = -> [Xe_element001]
  conduct = 2
  density = 1
  expand = 3
  formula = Xe
  name = G4_Xe
  specific = 4
FEATURE [App::DocumentObjectGroupPython] Cs_element003  label="Cs_element : 003"  # scripted group (container) (typed FeaturePython)
  n = 1
  ref = Cs_element
FEATURE [App::DocumentObjectGroupPython] G4_Cs  # scripted group (container) (typed FeaturePython)
  Dunit = g/cm3
  Dvalue = 1.873
  Group = -> [Cs_element003]
  conduct = 2
  density = 1
  expand = 3
  formula = Cs
  name = G4_Cs
  specific = 4
FEATURE [App::DocumentObjectGroupPython] Ba_element003  label="Ba_element : 003"  # scripted group (container) (typed FeaturePython)
  n = 1
  ref = Ba_element
FEATURE [App::DocumentObjectGroupPython] G4_Ba  # scripted group (container) (typed FeaturePython)
  Dunit = g/cm3
  Dvalue = 3.5
  Group = -> [Ba_element003]
  conduct = 2
  density = 1
  expand = 3
  formula = Ba
  name = G4_Ba
  specific = 4
FEATURE [App::DocumentObjectGroupPython] La_element003  label="La_element : 003"  # scripted group (container) (typed FeaturePython)
  n = 1
  ref = La_element
FEATURE [App::DocumentObjectGroupPython] G4_La  # scripted group (container) (typed FeaturePython)
  Dunit = g/cm3
  Dvalue = 6.154
  Group = -> [La_element003]
  conduct = 2
  density = 1
  expand = 3
  formula = La
  name = G4_La
  specific = 4
FEATURE [App::DocumentObjectGroupPython] Ce_element002  label="Ce_element : 1"  # scripted group (container) (typed FeaturePython)
  n = 1
  ref = Ce_element
FEATURE [App::DocumentObjectGroupPython] G4_Ce  # scripted group (container) (typed FeaturePython)
  Dunit = g/cm3
  Dvalue = 6.657
  Group = -> [Ce_element002]
  conduct = 2
  density = 1
  expand = 3
  formula = Ce
  name = G4_Ce
  specific = 4
FEATURE [App::DocumentObjectGroupPython] Pr_element001  label="Pr_element : 1"  # scripted group (container) (typed FeaturePython)
  n = 1
  ref = Pr_element
FEATURE [App::DocumentObjectGroupPython] G4_Pr  # scripted group (container) (typed FeaturePython)
  Dunit = g/cm3
  Dvalue = 6.71
  Group = -> [Pr_element001]
  conduct = 2
  density = 1
  expand = 3
  formula = Pr
  name = G4_Pr
  specific = 4
FEATURE [App::DocumentObjectGroupPython] Nd_element001  label="Nd_element : 1"  # scripted group (container) (typed FeaturePython)
  n = 1
  ref = Nd_element
FEATURE [App::DocumentObjectGroupPython] G4_Nd  # scripted group (container) (typed FeaturePython)
  Dunit = g/cm3
  Dvalue = 6.9
  Group = -> [Nd_element001]
  conduct = 2
  density = 1
  expand = 3
  formula = Nd
  name = G4_Nd
  specific = 4
FEATURE [App::DocumentObjectGroupPython] Pm_element001  label="Pm_element : 1"  # scripted group (container) (typed FeaturePython)
  n = 1
  ref = Pm_element
FEATURE [App::DocumentObjectGroupPython] G4_Pm  # scripted group (container) (typed FeaturePython)
  Dunit = g/cm3
  Dvalue = 7.22
  Group = -> [Pm_element001]
  conduct = 2
  density = 1
  expand = 3
  formula = Pm
  name = G4_Pm
  specific = 4
FEATURE [App::DocumentObjectGroupPython] Sm_element001  label="Sm_element : 1"  # scripted group (container) (typed FeaturePython)
  n = 1
  ref = Sm_element
FEATURE [App::DocumentObjectGroupPython] G4_Sm  # scripted group (container) (typed FeaturePython)
  Dunit = g/cm3
  Dvalue = 7.46
  Group = -> [Sm_element001]
  conduct = 2
  density = 1
  expand = 3
  formula = Sm
  name = G4_Sm
  specific = 4
FEATURE [App::DocumentObjectGroupPython] Eu_element001  label="Eu_element : 1"  # scripted group (container) (typed FeaturePython)
  n = 1
  ref = Eu_element
FEATURE [App::DocumentObjectGroupPython] G4_Eu  # scripted group (container) (typed FeaturePython)
  Dunit = g/cm3
  Dvalue = 5.243
  Group = -> [Eu_element001]
  conduct = 2
  density = 1
  expand = 3
  formula = Eu
  name = G4_Eu
  specific = 4
FEATURE [App::DocumentObjectGroupPython] Gd_element002  label="Gd_element : 1"  # scripted group (container) (typed FeaturePython)
  n = 1
  ref = Gd_element
FEATURE [App::DocumentObjectGroupPython] G4_Gd  # scripted group (container) (typed FeaturePython)
  Dunit = g/cm3
  Dvalue = 7.9004
  Group = -> [Gd_element002]
  conduct = 2
  density = 1
  expand = 3
  formula = Gd
  name = G4_Gd
  specific = 4
FEATURE [App::DocumentObjectGroupPython] Tb_element001  label="Tb_element : 1"  # scripted group (container) (typed FeaturePython)
  n = 1
  ref = Tb_element
FEATURE [App::DocumentObjectGroupPython] G4_Tb  # scripted group (container) (typed FeaturePython)
  Dunit = g/cm3
  Dvalue = 8.229
  Group = -> [Tb_element001]
  conduct = 2
  density = 1
  expand = 3
  formula = Tb
  name = G4_Tb
  specific = 4
FEATURE [App::DocumentObjectGroupPython] Dy_element001  label="Dy_element : 1"  # scripted group (container) (typed FeaturePython)
  n = 1
  ref = Dy_element
FEATURE [App::DocumentObjectGroupPython] G4_Dy  # scripted group (container) (typed FeaturePython)
  Dunit = g/cm3
  Dvalue = 8.55
  Group = -> [Dy_element001]
  conduct = 2
  density = 1
  expand = 3
  formula = Dy
  name = G4_Dy
  specific = 4
FEATURE [App::DocumentObjectGroupPython] Ho_element001  label="Ho_element : 1"  # scripted group (container) (typed FeaturePython)
  n = 1
  ref = Ho_element
FEATURE [App::DocumentObjectGroupPython] G4_Ho  # scripted group (container) (typed FeaturePython)
  Dunit = g/cm3
  Dvalue = 8.795
  Group = -> [Ho_element001]
  conduct = 2
  density = 1
  expand = 3
  formula = Ho
  name = G4_Ho
  specific = 4
FEATURE [App::DocumentObjectGroupPython] Er_element001  label="Er_element : 1"  # scripted group (container) (typed FeaturePython)
  n = 1
  ref = Er_element
FEATURE [App::DocumentObjectGroupPython] G4_Er  # scripted group (container) (typed FeaturePython)
  Dunit = g/cm3
  Dvalue = 9.066
  Group = -> [Er_element001]
  conduct = 2
  density = 1
  expand = 3
  formula = Er
  name = G4_Er
  specific = 4
FEATURE [App::DocumentObjectGroupPython] Tm_element001  label="Tm_element : 1"  # scripted group (container) (typed FeaturePython)
  n = 1
  ref = Tm_element
FEATURE [App::DocumentObjectGroupPython] G4_Tm  # scripted group (container) (typed FeaturePython)
  Dunit = g/cm3
  Dvalue = 9.321
  Group = -> [Tm_element001]
  conduct = 2
  density = 1
  expand = 3
  formula = Tm
  name = G4_Tm
  specific = 4
FEATURE [App::DocumentObjectGroupPython] Yb_element001  label="Yb_element : 1"  # scripted group (container) (typed FeaturePython)
  n = 1
  ref = Yb_element
FEATURE [App::DocumentObjectGroupPython] G4_Yb  # scripted group (container) (typed FeaturePython)
  Dunit = g/cm3
  Dvalue = 6.73
  Group = -> [Yb_element001]
  conduct = 2
  density = 1
  expand = 3
  formula = Yb
  name = G4_Yb
  specific = 4
FEATURE [App::DocumentObjectGroupPython] Lu_element001  label="Lu_element : 1"  # scripted group (container) (typed FeaturePython)
  n = 1
  ref = Lu_element
FEATURE [App::DocumentObjectGroupPython] G4_Lu  # scripted group (container) (typed FeaturePython)
  Dunit = g/cm3
  Dvalue = 9.84
  Group = -> [Lu_element001]
  conduct = 2
  density = 1
  expand = 3
  formula = Lu
  name = G4_Lu
  specific = 4
FEATURE [App::DocumentObjectGroupPython] Hf_element001  label="Hf_element : 1"  # scripted group (container) (typed FeaturePython)
  n = 1
  ref = Hf_element
FEATURE [App::DocumentObjectGroupPython] G4_Hf  # scripted group (container) (typed FeaturePython)
  Dunit = g/cm3
  Dvalue = 13.31
  Group = -> [Hf_element001]
  conduct = 2
  density = 1
  expand = 3
  formula = Hf
  name = G4_Hf
  specific = 4
FEATURE [App::DocumentObjectGroupPython] Ta_element001  label="Ta_element : 1"  # scripted group (container) (typed FeaturePython)
  n = 1
  ref = Ta_element
FEATURE [App::DocumentObjectGroupPython] G4_Ta  # scripted group (container) (typed FeaturePython)
  Dunit = g/cm3
  Dvalue = 16.654
  Group = -> [Ta_element001]
  conduct = 2
  density = 1
  expand = 3
  formula = Ta
  name = G4_Ta
  specific = 4
FEATURE [App::DocumentObjectGroupPython] W_element004  label="W_element : 004"  # scripted group (container) (typed FeaturePython)
  n = 1
  ref = W_element
FEATURE [App::DocumentObjectGroupPython] G4_W  # scripted group (container) (typed FeaturePython)
  Dunit = g/cm3
  Dvalue = 19.3
  Group = -> [W_element004]
  conduct = 2
  density = 1
  expand = 3
  formula = W
  name = G4_W
  specific = 4
FEATURE [App::DocumentObjectGroupPython] Re_element001  label="Re_element : 1"  # scripted group (container) (typed FeaturePython)
  n = 1
  ref = Re_element
FEATURE [App::DocumentObjectGroupPython] G4_Re  # scripted group (container) (typed FeaturePython)
  Dunit = g/cm3
  Dvalue = 21.02
  Group = -> [Re_element001]
  conduct = 2
  density = 1
  expand = 3
  formula = Re
  name = G4_Re
  specific = 4
FEATURE [App::DocumentObjectGroupPython] Os_element001  label="Os_element : 1"  # scripted group (container) (typed FeaturePython)
  n = 1
  ref = Os_element
FEATURE [App::DocumentObjectGroupPython] G4_Os  # scripted group (container) (typed FeaturePython)
  Dunit = g/cm3
  Dvalue = 22.57
  Group = -> [Os_element001]
  conduct = 2
  density = 1
  expand = 3
  formula = Os
  name = G4_Os
  specific = 4
FEATURE [App::DocumentObjectGroupPython] Ir_element001  label="Ir_element : 1"  # scripted group (container) (typed FeaturePython)
  n = 1
  ref = Ir_element
FEATURE [App::DocumentObjectGroupPython] G4_Ir  # scripted group (container) (typed FeaturePython)
  Dunit = g/cm3
  Dvalue = 22.42
  Group = -> [Ir_element001]
  conduct = 2
  density = 1
  expand = 3
  formula = Ir
  name = G4_Ir
  specific = 4
FEATURE [App::DocumentObjectGroupPython] Pt_element001  label="Pt_element : 1"  # scripted group (container) (typed FeaturePython)
  n = 1
  ref = Pt_element
FEATURE [App::DocumentObjectGroupPython] G4_Pt  # scripted group (container) (typed FeaturePython)
  Dunit = g/cm3
  Dvalue = 21.45
  Group = -> [Pt_element001]
  conduct = 2
  density = 1
  expand = 3
  formula = Pt
  name = G4_Pt
  specific = 4
FEATURE [App::DocumentObjectGroupPython] Au_element001  label="Au_element : 1"  # scripted group (container) (typed FeaturePython)
  n = 1
  ref = Au_element
FEATURE [App::DocumentObjectGroupPython] G4_Au  # scripted group (container) (typed FeaturePython)
  Dunit = g/cm3
  Dvalue = 19.32
  Group = -> [Au_element001]
  conduct = 2
  density = 1
  expand = 3
  formula = Au
  name = G4_Au
  specific = 4
FEATURE [App::DocumentObjectGroupPython] Hg_element002  label="Hg_element : 002"  # scripted group (container) (typed FeaturePython)
  n = 1
  ref = Hg_element
FEATURE [App::DocumentObjectGroupPython] G4_Hg  # scripted group (container) (typed FeaturePython)
  Dunit = g/cm3
  Dvalue = 13.546
  Group = -> [Hg_element002]
  conduct = 2
  density = 1
  expand = 3
  formula = Hg
  name = G4_Hg
  specific = 4
FEATURE [App::DocumentObjectGroupPython] Tl_element002  label="Tl_element : 002"  # scripted group (container) (typed FeaturePython)
  n = 1
  ref = Tl_element
FEATURE [App::DocumentObjectGroupPython] G4_Tl  # scripted group (container) (typed FeaturePython)
  Dunit = g/cm3
  Dvalue = 11.72
  Group = -> [Tl_element002]
  conduct = 2
  density = 1
  expand = 3
  formula = Tl
  name = G4_Tl
  specific = 4
FEATURE [App::DocumentObjectGroupPython] Pb_element003  label="Pb_element : 1"  # scripted group (container) (typed FeaturePython)
  n = 1
  ref = Pb_element
FEATURE [App::DocumentObjectGroupPython] G4_Pb  # scripted group (container) (typed FeaturePython)
  Dunit = g/cm3
  Dvalue = 11.35
  Group = -> [Pb_element003]
  conduct = 2
  density = 1
  expand = 3
  formula = Pb
  name = G4_Pb
  specific = 4
FEATURE [App::DocumentObjectGroupPython] Bi_element002  label="Bi_element : 1"  # scripted group (container) (typed FeaturePython)
  n = 1
  ref = Bi_element
FEATURE [App::DocumentObjectGroupPython] G4_Bi  # scripted group (container) (typed FeaturePython)
  Dunit = g/cm3
  Dvalue = 9.747
  Group = -> [Bi_element002]
  conduct = 2
  density = 1
  expand = 3
  formula = Bi
  name = G4_Bi
  specific = 4
FEATURE [App::DocumentObjectGroupPython] Po_element001  label="Po_element : 1"  # scripted group (container) (typed FeaturePython)
  n = 1
  ref = Po_element
FEATURE [App::DocumentObjectGroupPython] G4_Po  # scripted group (container) (typed FeaturePython)
  Dunit = g/cm3
  Dvalue = 9.32
  Group = -> [Po_element001]
  conduct = 2
  density = 1
  expand = 3
  formula = Po
  name = G4_Po
  specific = 4
FEATURE [App::DocumentObjectGroupPython] At_element001  label="At_element : 1"  # scripted group (container) (typed FeaturePython)
  n = 1
  ref = At_element
FEATURE [App::DocumentObjectGroupPython] G4_At  # scripted group (container) (typed FeaturePython)
  Dunit = g/cm3
  Dvalue = 9.32
  Group = -> [At_element001]
  conduct = 2
  density = 1
  expand = 3
  formula = At
  name = G4_At
  specific = 4
FEATURE [App::DocumentObjectGroupPython] Rn_element001  label="Rn_element : 1"  # scripted group (container) (typed FeaturePython)
  n = 1
  ref = Rn_element
FEATURE [App::DocumentObjectGroupPython] G4_Rn  # scripted group (container) (typed FeaturePython)
  Dunit = g/cm3
  Dvalue = 0.00900662
  Group = -> [Rn_element001]
  conduct = 2
  density = 1
  expand = 3
  formula = Rn
  name = G4_Rn
  specific = 4
FEATURE [App::DocumentObjectGroupPython] Fr_element001  label="Fr_element : 1"  # scripted group (container) (typed FeaturePython)
  n = 1
  ref = Fr_element
FEATURE [App::DocumentObjectGroupPython] G4_Fr  # scripted group (container) (typed FeaturePython)
  Dunit = g/cm3
  Dvalue = 1
  Group = -> [Fr_element001]
  conduct = 2
  density = 1
  expand = 3
  formula = Fr
  name = G4_Fr
  specific = 4
FEATURE [App::DocumentObjectGroupPython] Ra_element001  label="Ra_element : 1"  # scripted group (container) (typed FeaturePython)
  n = 1
  ref = Ra_element
FEATURE [App::DocumentObjectGroupPython] G4_Ra  # scripted group (container) (typed FeaturePython)
  Dunit = g/cm3
  Dvalue = 5
  Group = -> [Ra_element001]
  conduct = 2
  density = 1
  expand = 3
  formula = Ra
  name = G4_Ra
  specific = 4
FEATURE [App::DocumentObjectGroupPython] Ac_element001  label="Ac_element : 1"  # scripted group (container) (typed FeaturePython)
  n = 1
  ref = Ac_element
FEATURE [App::DocumentObjectGroupPython] G4_Ac  # scripted group (container) (typed FeaturePython)
  Dunit = g/cm3
  Dvalue = 10.07
  Group = -> [Ac_element001]
  conduct = 2
  density = 1
  expand = 3
  formula = Ac
  name = G4_Ac
  specific = 4
FEATURE [App::DocumentObjectGroupPython] Th_element001  label="Th_element : 1"  # scripted group (container) (typed FeaturePython)
  n = 1
  ref = Th_element
FEATURE [App::DocumentObjectGroupPython] G4_Th  # scripted group (container) (typed FeaturePython)
  Dunit = g/cm3
  Dvalue = 11.72
  Group = -> [Th_element001]
  conduct = 2
  density = 1
  expand = 3
  formula = Th
  name = G4_Th
  specific = 4
FEATURE [App::DocumentObjectGroupPython] Pa_element001  label="Pa_element : 1"  # scripted group (container) (typed FeaturePython)
  n = 1
  ref = Pa_element
FEATURE [App::DocumentObjectGroupPython] G4_Pa  # scripted group (container) (typed FeaturePython)
  Dunit = g/cm3
  Dvalue = 15.37
  Group = -> [Pa_element001]
  conduct = 2
  density = 1
  expand = 3
  formula = Pa
  name = G4_Pa
  specific = 4
FEATURE [App::DocumentObjectGroupPython] U_element004  label="U_element : 004"  # scripted group (container) (typed FeaturePython)
  n = 1
  ref = U_element
FEATURE [App::DocumentObjectGroupPython] G4_U  # scripted group (container) (typed FeaturePython)
  Dunit = g/cm3
  Dvalue = 18.95
  Group = -> [U_element004]
  conduct = 2
  density = 1
  expand = 3
  formula = U
  name = G4_U
  specific = 4
FEATURE [App::DocumentObjectGroupPython] Np_element001  label="Np_element : 1"  # scripted group (container) (typed FeaturePython)
  n = 1
  ref = Np_element
FEATURE [App::DocumentObjectGroupPython] G4_Np  # scripted group (container) (typed FeaturePython)
  Dunit = g/cm3
  Dvalue = 20.25
  Group = -> [Np_element001]
  conduct = 2
  density = 1
  expand = 3
  formula = Np
  name = G4_Np
  specific = 4
FEATURE [App::DocumentObjectGroupPython] Pu_element002  label="Pu_element : 002"  # scripted group (container) (typed FeaturePython)
  n = 1
  ref = Pu_element
FEATURE [App::DocumentObjectGroupPython] G4_Pu  # scripted group (container) (typed FeaturePython)
  Dunit = g/cm3
  Dvalue = 19.84
  Group = -> [Pu_element002]
  conduct = 2
  density = 1
  expand = 3
  formula = Pu
  name = G4_Pu
  specific = 4
FEATURE [App::DocumentObjectGroupPython] Am_element001  label="Am_element : 1"  # scripted group (container) (typed FeaturePython)
  n = 1
  ref = Am_element
FEATURE [App::DocumentObjectGroupPython] G4_Am  # scripted group (container) (typed FeaturePython)
  Dunit = g/cm3
  Dvalue = 13.67
  Group = -> [Am_element001]
  conduct = 2
  density = 1
  expand = 3
  formula = Am
  name = G4_Am
  specific = 4
FEATURE [App::DocumentObjectGroupPython] Cm_element001  label="Cm_element : 1"  # scripted group (container) (typed FeaturePython)
  n = 1
  ref = Cm_element
FEATURE [App::DocumentObjectGroupPython] G4_Cm  # scripted group (container) (typed FeaturePython)
  Dunit = g/cm3
  Dvalue = 13.51
  Group = -> [Cm_element001]
  conduct = 2
  density = 1
  expand = 3
  formula = Cm
  name = G4_Cm
  specific = 4
FEATURE [App::DocumentObjectGroupPython] Bk_element001  label="Bk_element : 1"  # scripted group (container) (typed FeaturePython)
  n = 1
  ref = Bk_element
FEATURE [App::DocumentObjectGroupPython] G4_Bk  # scripted group (container) (typed FeaturePython)
  Dunit = g/cm3
  Dvalue = 14
  Group = -> [Bk_element001]
  conduct = 2
  density = 1
  expand = 3
  formula = Bk
  name = G4_Bk
  specific = 4
FEATURE [App::DocumentObjectGroupPython] Cf_element001  label="Cf_element : 1"  # scripted group (container) (typed FeaturePython)
  n = 1
  ref = Cf_element
FEATURE [App::DocumentObjectGroupPython] G4_Cf  # scripted group (container) (typed FeaturePython)
  Dunit = g/cm3
  Dvalue = 10
  Group = -> [Cf_element001]
  conduct = 2
  density = 1
  expand = 3
  formula = Cf
  name = G4_Cf
  specific = 4
FEATURE [App::DocumentObjectGroupPython] Element  # scripted group (container) (typed FeaturePython)
  Group = -> [G4_H,G4_He,G4_Li,G4_Be,G4_B,G4_C,G4_N,G4_O,G4_F,G4_Ne,G4_Na,G4_Mg,G4_Al,G4_Si,G4_P,G4_S,G4_Cl,G4_Ar,G4_K,G4_Ca,G4_Sc,G4_Ti,G4_V,G4_Cr,G4_Mn,G4_Fe,G4_Co,G4_Ni,G4_Cu,G4_Zn,G4_Ga,G4_Ge,G4_As,G4_Se,G4_Br,G4_Kr,G4_Rb,G4_Sr,G4_Y,G4_Zr,G4_Nb,G4_Mo,G4_Tc,G4_Ru,G4_Rh,G4_Pd,G4_Ag,G4_Cd,G4_In,G4_Sn,G4_Sb,G4_Te,G4_I,G4_Xe,G4_Cs,G4_Ba,G4_La,G4_Ce,G4_Pr,G4_Nd,G4_Pm,G4_Sm,G4_Eu,G4_Gd,G4_Tb,G4_Dy,G4_Ho,G4_Er,+30 more]
FEATURE [App::DocumentObjectGroupPython] H_element114  label="H_element : 063"  # scripted group (container) (typed FeaturePython)
  n = 2
  ref = H_element
FEATURE [App::DocumentObjectGroupPython] G4_lH2  # scripted group (container) (typed FeaturePython)
  Dunit = g/cm3
  Dvalue = 0.0708
  Group = -> [H_element114]
  conduct = 2
  density = 1
  expand = 3
  formula = G4_lH2
  name = G4_lH2
  specific = 4
FEATURE [App::DocumentObjectGroupPython] N_element049  label="N_element : 022"  # scripted group (container) (typed FeaturePython)
  n = 2
  ref = N_element
FEATURE [App::DocumentObjectGroupPython] G4_lN2  # scripted group (container) (typed FeaturePython)
  Dunit = g/cm3
  Dvalue = 0.807
  Group = -> [N_element049]
  conduct = 2
  density = 1
  expand = 3
  formula = G4_lN2
  name = G4_lN2
  specific = 4
FEATURE [App::DocumentObjectGroupPython] O_element106  label="O_element : 060"  # scripted group (container) (typed FeaturePython)
  n = 2
  ref = O_element
FEATURE [App::DocumentObjectGroupPython] G4_lO2  # scripted group (container) (typed FeaturePython)
  Dunit = g/cm3
  Dvalue = 1.141
  Group = -> [O_element106]
  conduct = 2
  density = 1
  expand = 3
  formula = G4_lO2
  name = G4_lO2
  specific = 4
FEATURE [App::DocumentObjectGroupPython] Ar  label="Ar : 1"  # scripted group (container) (typed FeaturePython)
  n = 1
  ref = Ar
FEATURE [App::DocumentObjectGroupPython] G4_lAr  # scripted group (container) (typed FeaturePython)
  Dunit = g/cm3
  Dvalue = 1.396
  Group = -> [Ar]
  conduct = 2
  density = 1
  expand = 3
  formula = G4_lAr
  name = G4_lAr
  specific = 4
FEATURE [App::DocumentObjectGroupPython] Br  label="Br : 1"  # scripted group (container) (typed FeaturePython)
  n = 1
  ref = Br
FEATURE [App::DocumentObjectGroupPython] G4_lBr  # scripted group (container) (typed FeaturePython)
  Dunit = g/cm3
  Dvalue = 3.1028
  Group = -> [Br]
  conduct = 2
  density = 1
  expand = 3
  formula = G4_lBr
  name = G4_lBr
  specific = 4
FEATURE [App::DocumentObjectGroupPython] Kr  label="Kr : 1"  # scripted group (container) (typed FeaturePython)
  n = 1
  ref = Kr
FEATURE [App::DocumentObjectGroupPython] G4_lKr  # scripted group (container) (typed FeaturePython)
  Dunit = g/cm3
  Dvalue = 2.418
  Group = -> [Kr]
  conduct = 2
  density = 1
  expand = 3
  formula = G4_lKr
  name = G4_lKr
  specific = 4
FEATURE [App::DocumentObjectGroupPython] Xe  label="Xe : 1"  # scripted group (container) (typed FeaturePython)
  n = 1
  ref = Xe
FEATURE [App::DocumentObjectGroupPython] G4_lXe  # scripted group (container) (typed FeaturePython)
  Dunit = g/cm3
  Dvalue = 2.953
  Group = -> [Xe]
  conduct = 2
  density = 1
  expand = 3
  formula = G4_lXe
  name = G4_lXe
  specific = 4
FEATURE [App::DocumentObjectGroupPython] O_element107  label="O_element : 061"  # scripted group (container) (typed FeaturePython)
  n = 4
  ref = O_element
FEATURE [App::DocumentObjectGroupPython] Pb_element004  label="Pb_element : 002"  # scripted group (container) (typed FeaturePython)
  n = 1
  ref = Pb_element
FEATURE [App::DocumentObjectGroupPython] W_element005  label="W_element : 005"  # scripted group (container) (typed FeaturePython)
  n = 1
  ref = W_element
FEATURE [App::DocumentObjectGroupPython] G4_PbWO4  # scripted group (container) (typed FeaturePython)
  Dunit = g/cm3
  Dvalue = 8.28
  Group = -> [O_element107,Pb_element004,W_element005]
  conduct = 2
  density = 1
  expand = 3
  formula = G4_PbWO4
  name = G4_PbWO4
  specific = 4
FEATURE [App::DocumentObjectGroupPython] alactic  label="alactic : 1"  # scripted group (container) (typed FeaturePython)
  n = 1
  ref = alactic
FEATURE [App::DocumentObjectGroupPython] G4_Galactic  # scripted group (container) (typed FeaturePython)
  Dunit = g/cm3
  Dvalue = 0
  Group = -> [alactic]
  conduct = 2
  density = 1
  expand = 3
  formula = G4_Galactic
  name = G4_Galactic
  specific = 4
FEATURE [App::DocumentObjectGroupPython] RAPHITE_POROUS  label="RAPHITE_POROUS : 1"  # scripted group (container) (typed FeaturePython)
  n = 1
  ref = RAPHITE_POROUS
FEATURE [App::DocumentObjectGroupPython] G4_GRAPHITE_POROUS  # scripted group (container) (typed FeaturePython)
  Dunit = g/cm3
  Dvalue = 1.7
  Group = -> [RAPHITE_POROUS]
  conduct = 2
  density = 1
  expand = 3
  formula = G4_GRAPHITE_POROUS
  name = G4_GRAPHITE_POROUS
  specific = 4
FEATURE [App::DocumentObjectGroupPython] H_element115  label="H_element : 0.150"  # scripted group (container) (typed FeaturePython)
  n = 0.080538
FEATURE [App::DocumentObjectGroupPython] C_element125  label="C_element : 0.600"  # scripted group (container) (typed FeaturePython)
  n = 0.599848
FEATURE [App::DocumentObjectGroupPython] O_element108  label="O_element : 0.320"  # scripted group (container) (typed FeaturePython)
  n = 0.319614
FEATURE [App::DocumentObjectGroupPython] G4_LUCITE  # scripted group (container) (typed FeaturePython)
  Dunit = g/cm3
  Dvalue = 1.19
  Group = -> [H_element115,C_element125,O_element108]
  conduct = 2
  density = 1
  expand = 3
  formula = G4_LUCITE
  name = G4_LUCITE
  specific = 4
FEATURE [App::DocumentObjectGroupPython] Cu_element002  label="Cu_element : 62"  # scripted group (container) (typed FeaturePython)
  n = 62
  ref = Cu_element
FEATURE [App::DocumentObjectGroupPython] Zn_element002  label="Zn_element : 35"  # scripted group (container) (typed FeaturePython)
  n = 35
  ref = Zn_element
FEATURE [App::DocumentObjectGroupPython] Pb_element005  label="Pb_element : 3"  # scripted group (container) (typed FeaturePython)
  n = 3
  ref = Pb_element
FEATURE [App::DocumentObjectGroupPython] G4_BRASS  # scripted group (container) (typed FeaturePython)
  Dunit = g/cm3
  Dvalue = 8.52
  Group = -> [Cu_element002,Zn_element002,Pb_element005]
  conduct = 2
  density = 1
  expand = 3
  formula = G4_BRASS
  name = G4_BRASS
  specific = 4
FEATURE [App::DocumentObjectGroupPython] Cu_element003  label="Cu_element : 89"  # scripted group (container) (typed FeaturePython)
  n = 89
  ref = Cu_element
FEATURE [App::DocumentObjectGroupPython] Zn_element003  label="Zn_element : 9"  # scripted group (container) (typed FeaturePython)
  n = 9
  ref = Zn_element
FEATURE [App::DocumentObjectGroupPython] Pb_element006  label="Pb_element : 2"  # scripted group (container) (typed FeaturePython)
  n = 2
  ref = Pb_element
FEATURE [App::DocumentObjectGroupPython] G4_BRONZE  # scripted group (container) (typed FeaturePython)
  Dunit = g/cm3
  Dvalue = 8.82
  Group = -> [Cu_element003,Zn_element003,Pb_element006]
  conduct = 2
  density = 1
  expand = 3
  formula = G4_BRONZE
  name = G4_BRONZE
  specific = 4
FEATURE [App::DocumentObjectGroupPython] Fe_element008  label="Fe_element : 74"  # scripted group (container) (typed FeaturePython)
  n = 74
  ref = Fe_element
FEATURE [App::DocumentObjectGroupPython] Cr_element002  label="Cr_element : 18"  # scripted group (container) (typed FeaturePython)
  n = 18
  ref = Cr_element
FEATURE [App::DocumentObjectGroupPython] Ni_element002  label="Ni_element : 8"  # scripted group (container) (typed FeaturePython)
  n = 8
  ref = Ni_element
FEATURE [App::DocumentObjectGroupPython] G4_STAINLESS_STEEL  label="G4_STAINLESS-STEEL"  # scripted group (container) (typed FeaturePython)
  Dunit = g/cm3
  Dvalue = 8
  Group = -> [Fe_element008,Cr_element002,Ni_element002]
  conduct = 2
  density = 1
  expand = 3
  formula = G4_STAINLESS-STEEL
  name = G4_STAINLESS-STEEL
  specific = 4
FEATURE [App::DocumentObjectGroupPython] H_element116  label="H_element : 064"  # scripted group (container) (typed FeaturePython)
  n = 18
  ref = H_element
FEATURE [App::DocumentObjectGroupPython] C_element126  label="C_element : 071"  # scripted group (container) (typed FeaturePython)
  n = 12
  ref = C_element
FEATURE [App::DocumentObjectGroupPython] O_element109  label="O_element : 062"  # scripted group (container) (typed FeaturePython)
  n = 7
  ref = O_element
FEATURE [App::DocumentObjectGroupPython] G4_CR39  # scripted group (container) (typed FeaturePython)
  Dunit = g/cm3
  Dvalue = 1.32
  Group = -> [H_element116,C_element126,O_element109]
  conduct = 2
  density = 1
  expand = 3
  formula = G4_CR39
  name = G4_CR39
  specific = 4
FEATURE [App::DocumentObjectGroupPython] H_element117  label="H_element : 38"  # scripted group (container) (typed FeaturePython)
  n = 38
  ref = H_element
FEATURE [App::DocumentObjectGroupPython] C_element127  label="C_element : 072"  # scripted group (container) (typed FeaturePython)
  n = 18
  ref = C_element
FEATURE [App::DocumentObjectGroupPython] O_element110  label="O_element : 063"  # scripted group (container) (typed FeaturePython)
  n = 1
  ref = O_element
FEATURE [App::DocumentObjectGroupPython] G4_OCTADECANOL  # scripted group (container) (typed FeaturePython)
  Dunit = g/cm3
  Dvalue = 0.812
  Group = -> [H_element117,C_element127,O_element110]
  conduct = 2
  density = 1
  expand = 3
  formula = G4_OCTADECANOL
  name = G4_OCTADECANOL
  specific = 4
FEATURE [App::DocumentObjectGroupPython] HEP  # scripted group (container) (typed FeaturePython)
  Group = -> [G4_lH2,G4_lN2,G4_lO2,G4_lAr,G4_lBr,G4_lKr,G4_lXe,G4_PbWO4,G4_Galactic,G4_GRAPHITE_POROUS,G4_LUCITE,G4_BRASS,G4_BRONZE,G4_STAINLESS_STEEL,G4_CR39,G4_OCTADECANOL]
FEATURE [App::DocumentObjectGroupPython] C_element128  label="C_element : 073"  # scripted group (container) (typed FeaturePython)
  n = 14
  ref = C_element
FEATURE [App::DocumentObjectGroupPython] H_element118  label="H_element : 065"  # scripted group (container) (typed FeaturePython)
  n = 10
  ref = H_element
FEATURE [App::DocumentObjectGroupPython] O_element111  label="O_element : 064"  # scripted group (container) (typed FeaturePython)
  n = 2
  ref = O_element
FEATURE [App::DocumentObjectGroupPython] N_element050  label="N_element : 023"  # scripted group (container) (typed FeaturePython)
  n = 2
  ref = N_element
FEATURE [App::DocumentObjectGroupPython] G4_KEVLAR  # scripted group (container) (typed FeaturePython)
  Dunit = g/cm3
  Dvalue = 1.44
  Group = -> [C_element128,H_element118,O_element111,N_element050]
  conduct = 2
  density = 1
  expand = 3
  formula = G4_KEVLAR
  name = G4_KEVLAR
  specific = 4
FEATURE [App::DocumentObjectGroupPython] C_element129  label="C_element : 074"  # scripted group (container) (typed FeaturePython)
  n = 10
  ref = C_element
FEATURE [App::DocumentObjectGroupPython] H_element119  label="H_element : 066"  # scripted group (container) (typed FeaturePython)
  n = 8
  ref = H_element
FEATURE [App::DocumentObjectGroupPython] O_element112  label="O_element : 065"  # scripted group (container) (typed FeaturePython)
  n = 4
  ref = O_element
FEATURE [App::DocumentObjectGroupPython] G4_DACRON  # scripted group (container) (typed FeaturePython)
  Dunit = g/cm3
  Dvalue = 1.4
  Group = -> [C_element129,H_element119,O_element112]
  conduct = 2
  density = 1
  expand = 3
  formula = G4_DACRON
  name = G4_DACRON
  specific = 4
FEATURE [App::DocumentObjectGroupPython] C_element130  label="C_element : 075"  # scripted group (container) (typed FeaturePython)
  n = 4
  ref = C_element
FEATURE [App::DocumentObjectGroupPython] H_element120  label="H_element : 067"  # scripted group (container) (typed FeaturePython)
  n = 5
  ref = H_element
FEATURE [App::DocumentObjectGroupPython] Cl_element030  label="Cl_element : 016"  # scripted group (container) (typed FeaturePython)
  n = 1
  ref = Cl_element
FEATURE [App::DocumentObjectGroupPython] G4_NEOPRENE  # scripted group (container) (typed FeaturePython)
  Dunit = g/cm3
  Dvalue = 1.23
  Group = -> [C_element130,H_element120,Cl_element030]
  conduct = 2
  density = 1
  expand = 3
  formula = G4_NEOPRENE
  name = G4_NEOPRENE
  specific = 4
FEATURE [App::DocumentObjectGroupPython] Space  # scripted group (container) (typed FeaturePython)
  Group = -> [G4_KEVLAR,G4_DACRON,G4_NEOPRENE]
FEATURE [App::DocumentObjectGroupPython] H_element121  label="H_element : 068"  # scripted group (container) (typed FeaturePython)
  n = 5
  ref = H_element
FEATURE [App::DocumentObjectGroupPython] C_element131  label="C_element : 076"  # scripted group (container) (typed FeaturePython)
  n = 4
  ref = C_element
FEATURE [App::DocumentObjectGroupPython] N_element051  label="N_element : 3"  # scripted group (container) (typed FeaturePython)
  n = 3
  ref = N_element
FEATURE [App::DocumentObjectGroupPython] O_element113  label="O_element : 066"  # scripted group (container) (typed FeaturePython)
  n = 1
  ref = O_element
FEATURE [App::DocumentObjectGroupPython] G4_CYTOSINE  # scripted group (container) (typed FeaturePython)
  Dunit = g/cm3
  Dvalue = 1.55
  Group = -> [H_element121,C_element131,N_element051,O_element113]
  conduct = 2
  density = 1
  expand = 3
  formula = G4_CYTOSINE
  name = G4_CYTOSINE
  specific = 4
FEATURE [App::DocumentObjectGroupPython] H_element122  label="H_element : 069"  # scripted group (container) (typed FeaturePython)
  n = 6
  ref = H_element
FEATURE [App::DocumentObjectGroupPython] C_element132  label="C_element : 077"  # scripted group (container) (typed FeaturePython)
  n = 5
  ref = C_element
FEATURE [App::DocumentObjectGroupPython] N_element052  label="N_element : 024"  # scripted group (container) (typed FeaturePython)
  n = 2
  ref = N_element
FEATURE [App::DocumentObjectGroupPython] O_element114  label="O_element : 067"  # scripted group (container) (typed FeaturePython)
  n = 2
  ref = O_element
FEATURE [App::DocumentObjectGroupPython] G4_THYMINE  # scripted group (container) (typed FeaturePython)
  Dunit = g/cm3
  Dvalue = 1.23
  Group = -> [H_element122,C_element132,N_element052,O_element114]
  conduct = 2
  density = 1
  expand = 3
  formula = G4_THYMINE
  name = G4_THYMINE
  specific = 4
FEATURE [App::DocumentObjectGroupPython] H_element123  label="H_element : 070"  # scripted group (container) (typed FeaturePython)
  n = 4
  ref = H_element
FEATURE [App::DocumentObjectGroupPython] C_element133  label="C_element : 078"  # scripted group (container) (typed FeaturePython)
  n = 4
  ref = C_element
FEATURE [App::DocumentObjectGroupPython] N_element053  label="N_element : 025"  # scripted group (container) (typed FeaturePython)
  n = 2
  ref = N_element
FEATURE [App::DocumentObjectGroupPython] O_element115  label="O_element : 068"  # scripted group (container) (typed FeaturePython)
  n = 2
  ref = O_element
FEATURE [App::DocumentObjectGroupPython] G4_URACIL  # scripted group (container) (typed FeaturePython)
  Dunit = g/cm3
  Dvalue = 1.32
  Group = -> [H_element123,C_element133,N_element053,O_element115]
  conduct = 2
  density = 1
  expand = 3
  formula = G4_URACIL
  name = G4_URACIL
  specific = 4
FEATURE [App::DocumentObjectGroupPython] H_element124  label="H_element : 071"  # scripted group (container) (typed FeaturePython)
  n = 4
  ref = H_element
FEATURE [App::DocumentObjectGroupPython] C_element134  label="C_element : 079"  # scripted group (container) (typed FeaturePython)
  n = 5
  ref = C_element
FEATURE [App::DocumentObjectGroupPython] N_element054  label="N_element : 026"  # scripted group (container) (typed FeaturePython)
  n = 5
  ref = N_element
FEATURE [App::DocumentObjectGroupPython] G4_DNA_ADENINE  # scripted group (container) (typed FeaturePython)
  Dunit = g/cm3
  Dvalue = 1
  Group = -> [H_element124,C_element134,N_element054]
  conduct = 2
  density = 1
  expand = 3
  formula = G4_DNA_ADENINE
  name = G4_DNA_ADENINE
  specific = 4
FEATURE [App::DocumentObjectGroupPython] H_element125  label="H_element : 072"  # scripted group (container) (typed FeaturePython)
  n = 4
  ref = H_element
FEATURE [App::DocumentObjectGroupPython] C_element135  label="C_element : 080"  # scripted group (container) (typed FeaturePython)
  n = 5
  ref = C_element
FEATURE [App::DocumentObjectGroupPython] N_element055  label="N_element : 027"  # scripted group (container) (typed FeaturePython)
  n = 5
  ref = N_element
FEATURE [App::DocumentObjectGroupPython] O_element116  label="O_element : 069"  # scripted group (container) (typed FeaturePython)
  n = 1
  ref = O_element
FEATURE [App::DocumentObjectGroupPython] G4_DNA_GUANINE  # scripted group (container) (typed FeaturePython)
  Dunit = g/cm3
  Dvalue = 1
  Group = -> [H_element125,C_element135,N_element055,O_element116]
  conduct = 2
  density = 1
  expand = 3
  formula = G4_DNA_GUANINE
  name = G4_DNA_GUANINE
  specific = 4
FEATURE [App::DocumentObjectGroupPython] H_element126  label="H_element : 073"  # scripted group (container) (typed FeaturePython)
  n = 4
  ref = H_element
FEATURE [App::DocumentObjectGroupPython] C_element136  label="C_element : 081"  # scripted group (container) (typed FeaturePython)
  n = 4
  ref = C_element
FEATURE [App::DocumentObjectGroupPython] N_element056  label="N_element : 028"  # scripted group (container) (typed FeaturePython)
  n = 3
  ref = N_element
FEATURE [App::DocumentObjectGroupPython] O_element117  label="O_element : 070"  # scripted group (container) (typed FeaturePython)
  n = 1
  ref = O_element
FEATURE [App::DocumentObjectGroupPython] G4_DNA_CYTOSINE  # scripted group (container) (typed FeaturePython)
  Dunit = g/cm3
  Dvalue = 1
  Group = -> [H_element126,C_element136,N_element056,O_element117]
  conduct = 2
  density = 1
  expand = 3
  formula = G4_DNA_CYTOSINE
  name = G4_DNA_CYTOSINE
  specific = 4
FEATURE [App::DocumentObjectGroupPython] H_element127  label="H_element : 074"  # scripted group (container) (typed FeaturePython)
  n = 5
  ref = H_element
FEATURE [App::DocumentObjectGroupPython] C_element137  label="C_element : 082"  # scripted group (container) (typed FeaturePython)
  n = 5
  ref = C_element
FEATURE [App::DocumentObjectGroupPython] N_element057  label="N_element : 029"  # scripted group (container) (typed FeaturePython)
  n = 2
  ref = N_element
FEATURE [App::DocumentObjectGroupPython] O_element118  label="O_element : 071"  # scripted group (container) (typed FeaturePython)
  n = 2
  ref = O_element
FEATURE [App::DocumentObjectGroupPython] G4_DNA_THYMINE  # scripted group (container) (typed FeaturePython)
  Dunit = g/cm3
  Dvalue = 1
  Group = -> [H_element127,C_element137,N_element057,O_element118]
  conduct = 2
  density = 1
  expand = 3
  formula = G4_DNA_THYMINE
  name = G4_DNA_THYMINE
  specific = 4
FEATURE [App::DocumentObjectGroupPython] H_element128  label="H_element : 075"  # scripted group (container) (typed FeaturePython)
  n = 3
  ref = H_element
FEATURE [App::DocumentObjectGroupPython] C_element138  label="C_element : 083"  # scripted group (container) (typed FeaturePython)
  n = 4
  ref = C_element
FEATURE [App::DocumentObjectGroupPython] N_element058  label="N_element : 030"  # scripted group (container) (typed FeaturePython)
  n = 2
  ref = N_element
FEATURE [App::DocumentObjectGroupPython] O_element119  label="O_element : 072"  # scripted group (container) (typed FeaturePython)
  n = 2
  ref = O_element
FEATURE [App::DocumentObjectGroupPython] G4_DNA_URACIL  # scripted group (container) (typed FeaturePython)
  Dunit = g/cm3
  Dvalue = 1
  Group = -> [H_element128,C_element138,N_element058,O_element119]
  conduct = 2
  density = 1
  expand = 3
  formula = G4_DNA_URACIL
  name = G4_DNA_URACIL
  specific = 4
FEATURE [App::DocumentObjectGroupPython] H_element129  label="H_element : 076"  # scripted group (container) (typed FeaturePython)
  n = 10
  ref = H_element
FEATURE [App::DocumentObjectGroupPython] C_element139  label="C_element : 084"  # scripted group (container) (typed FeaturePython)
  n = 10
  ref = C_element
FEATURE [App::DocumentObjectGroupPython] N_element059  label="N_element : 031"  # scripted group (container) (typed FeaturePython)
  n = 5
  ref = N_element
FEATURE [App::DocumentObjectGroupPython] O_element120  label="O_element : 073"  # scripted group (container) (typed FeaturePython)
  n = 4
  ref = O_element
FEATURE [App::DocumentObjectGroupPython] G4_DNA_ADENOSINE  # scripted group (container) (typed FeaturePython)
  Dunit = g/cm3
  Dvalue = 1
  Group = -> [H_element129,C_element139,N_element059,O_element120]
  conduct = 2
  density = 1
  expand = 3
  formula = G4_DNA_ADENOSINE
  name = G4_DNA_ADENOSINE
  specific = 4
FEATURE [App::DocumentObjectGroupPython] H_element130  label="H_element : 077"  # scripted group (container) (typed FeaturePython)
  n = 10
  ref = H_element
FEATURE [App::DocumentObjectGroupPython] C_element140  label="C_element : 085"  # scripted group (container) (typed FeaturePython)
  n = 10
  ref = C_element
FEATURE [App::DocumentObjectGroupPython] N_element060  label="N_element : 032"  # scripted group (container) (typed FeaturePython)
  n = 5
  ref = N_element
FEATURE [App::DocumentObjectGroupPython] O_element121  label="O_element : 074"  # scripted group (container) (typed FeaturePython)
  n = 5
  ref = O_element
FEATURE [App::DocumentObjectGroupPython] G4_DNA_GUANOSINE  # scripted group (container) (typed FeaturePython)
  Dunit = g/cm3
  Dvalue = 1
  Group = -> [H_element130,C_element140,N_element060,O_element121]
  conduct = 2
  density = 1
  expand = 3
  formula = G4_DNA_GUANOSINE
  name = G4_DNA_GUANOSINE
  specific = 4
FEATURE [App::DocumentObjectGroupPython] H_element131  label="H_element : 078"  # scripted group (container) (typed FeaturePython)
  n = 10
  ref = H_element
FEATURE [App::DocumentObjectGroupPython] C_element141  label="C_element : 086"  # scripted group (container) (typed FeaturePython)
  n = 9
  ref = C_element
FEATURE [App::DocumentObjectGroupPython] N_element061  label="N_element : 033"  # scripted group (container) (typed FeaturePython)
  n = 3
  ref = N_element
FEATURE [App::DocumentObjectGroupPython] O_element122  label="O_element : 075"  # scripted group (container) (typed FeaturePython)
  n = 5
  ref = O_element
FEATURE [App::DocumentObjectGroupPython] G4_DNA_CYTIDINE  # scripted group (container) (typed FeaturePython)
  Dunit = g/cm3
  Dvalue = 1
  Group = -> [H_element131,C_element141,N_element061,O_element122]
  conduct = 2
  density = 1
  expand = 3
  formula = G4_DNA_CYTIDINE
  name = G4_DNA_CYTIDINE
  specific = 4
FEATURE [App::DocumentObjectGroupPython] H_element132  label="H_element : 079"  # scripted group (container) (typed FeaturePython)
  n = 9
  ref = H_element
FEATURE [App::DocumentObjectGroupPython] C_element142  label="C_element : 087"  # scripted group (container) (typed FeaturePython)
  n = 9
  ref = C_element
FEATURE [App::DocumentObjectGroupPython] N_element062  label="N_element : 034"  # scripted group (container) (typed FeaturePython)
  n = 2
  ref = N_element
FEATURE [App::DocumentObjectGroupPython] O_element123  label="O_element : 076"  # scripted group (container) (typed FeaturePython)
  n = 6
  ref = O_element
FEATURE [App::DocumentObjectGroupPython] G4_DNA_URIDINE  # scripted group (container) (typed FeaturePython)
  Dunit = g/cm3
  Dvalue = 1
  Group = -> [H_element132,C_element142,N_element062,O_element123]
  conduct = 2
  density = 1
  expand = 3
  formula = G4_DNA_URIDINE
  name = G4_DNA_URIDINE
  specific = 4
FEATURE [App::DocumentObjectGroupPython] H_element133  label="H_element : 080"  # scripted group (container) (typed FeaturePython)
  n = 11
  ref = H_element
FEATURE [App::DocumentObjectGroupPython] C_element143  label="C_element : 088"  # scripted group (container) (typed FeaturePython)
  n = 10
  ref = C_element
FEATURE [App::DocumentObjectGroupPython] N_element063  label="N_element : 035"  # scripted group (container) (typed FeaturePython)
  n = 2
  ref = N_element
FEATURE [App::DocumentObjectGroupPython] O_element124  label="O_element : 077"  # scripted group (container) (typed FeaturePython)
  n = 6
  ref = O_element
FEATURE [App::DocumentObjectGroupPython] G4_DNA_METHYLURIDINE  # scripted group (container) (typed FeaturePython)
  Dunit = g/cm3
  Dvalue = 1
  Group = -> [H_element133,C_element143,N_element063,O_element124]
  conduct = 2
  density = 1
  expand = 3
  formula = G4_DNA_METHYLURIDINE
  name = G4_DNA_METHYLURIDINE
  specific = 4
FEATURE [App::DocumentObjectGroupPython] P_element014  label="P_element : 003"  # scripted group (container) (typed FeaturePython)
  n = 1
  ref = P_element
FEATURE [App::DocumentObjectGroupPython] O_element125  label="O_element : 078"  # scripted group (container) (typed FeaturePython)
  n = 3
  ref = O_element
FEATURE [App::DocumentObjectGroupPython] G4_DNA_MONOPHOSPHATE  # scripted group (container) (typed FeaturePython)
  Dunit = g/cm3
  Dvalue = 1
  Group = -> [P_element014,O_element125]
  conduct = 2
  density = 1
  expand = 3
  formula = G4_DNA_MONOPHOSPHATE
  name = G4_DNA_MONOPHOSPHATE
  specific = 4
FEATURE [App::DocumentObjectGroupPython] H_element134  label="H_element : 081"  # scripted group (container) (typed FeaturePython)
  n = 10
  ref = H_element
FEATURE [App::DocumentObjectGroupPython] C_element144  label="C_element : 089"  # scripted group (container) (typed FeaturePython)
  n = 10
  ref = C_element
FEATURE [App::DocumentObjectGroupPython] N_element064  label="N_element : 036"  # scripted group (container) (typed FeaturePython)
  n = 5
  ref = N_element
FEATURE [App::DocumentObjectGroupPython] O_element126  label="O_element : 079"  # scripted group (container) (typed FeaturePython)
  n = 7
  ref = O_element
FEATURE [App::DocumentObjectGroupPython] P_element015  label="P_element : 004"  # scripted group (container) (typed FeaturePython)
  n = 1
  ref = P_element
FEATURE [App::DocumentObjectGroupPython] G4_DNA_A  # scripted group (container) (typed FeaturePython)
  Dunit = g/cm3
  Dvalue = 1
  Group = -> [H_element134,C_element144,N_element064,O_element126,P_element015]
  conduct = 2
  density = 1
  expand = 3
  formula = G4_DNA_A
  name = G4_DNA_A
  specific = 4
FEATURE [App::DocumentObjectGroupPython] H_element135  label="H_element : 082"  # scripted group (container) (typed FeaturePython)
  n = 10
  ref = H_element
FEATURE [App::DocumentObjectGroupPython] C_element145  label="C_element : 090"  # scripted group (container) (typed FeaturePython)
  n = 10
  ref = C_element
FEATURE [App::DocumentObjectGroupPython] N_element065  label="N_element : 037"  # scripted group (container) (typed FeaturePython)
  n = 5
  ref = N_element
FEATURE [App::DocumentObjectGroupPython] O_element127  label="O_element : 8"  # scripted group (container) (typed FeaturePython)
  n = 8
  ref = O_element
FEATURE [App::DocumentObjectGroupPython] P_element016  label="P_element : 005"  # scripted group (container) (typed FeaturePython)
  n = 1
  ref = P_element
FEATURE [App::DocumentObjectGroupPython] G4_DNA_G  # scripted group (container) (typed FeaturePython)
  Dunit = g/cm3
  Dvalue = 1
  Group = -> [H_element135,C_element145,N_element065,O_element127,P_element016]
  conduct = 2
  density = 1
  expand = 3
  formula = G4_DNA_G
  name = G4_DNA_G
  specific = 4
FEATURE [App::DocumentObjectGroupPython] H_element136  label="H_element : 083"  # scripted group (container) (typed FeaturePython)
  n = 10
  ref = H_element
FEATURE [App::DocumentObjectGroupPython] C_element146  label="C_element : 091"  # scripted group (container) (typed FeaturePython)
  n = 9
  ref = C_element
FEATURE [App::DocumentObjectGroupPython] N_element066  label="N_element : 038"  # scripted group (container) (typed FeaturePython)
  n = 3
  ref = N_element
FEATURE [App::DocumentObjectGroupPython] O_element128  label="O_element : 080"  # scripted group (container) (typed FeaturePython)
  n = 8
  ref = O_element
FEATURE [App::DocumentObjectGroupPython] P_element017  label="P_element : 006"  # scripted group (container) (typed FeaturePython)
  n = 1
  ref = P_element
FEATURE [App::DocumentObjectGroupPython] G4_DNA_C  # scripted group (container) (typed FeaturePython)
  Dunit = g/cm3
  Dvalue = 1
  Group = -> [H_element136,C_element146,N_element066,O_element128,P_element017]
  conduct = 2
  density = 1
  expand = 3
  formula = G4_DNA_C
  name = G4_DNA_C
  specific = 4
FEATURE [App::DocumentObjectGroupPython] H_element137  label="H_element : 084"  # scripted group (container) (typed FeaturePython)
  n = 9
  ref = H_element
FEATURE [App::DocumentObjectGroupPython] C_element147  label="C_element : 092"  # scripted group (container) (typed FeaturePython)
  n = 9
  ref = C_element
FEATURE [App::DocumentObjectGroupPython] N_element067  label="N_element : 039"  # scripted group (container) (typed FeaturePython)
  n = 2
  ref = N_element
FEATURE [App::DocumentObjectGroupPython] O_element129  label="O_element : 9"  # scripted group (container) (typed FeaturePython)
  n = 9
  ref = O_element
FEATURE [App::DocumentObjectGroupPython] P_element018  label="P_element : 007"  # scripted group (container) (typed FeaturePython)
  n = 1
  ref = P_element
FEATURE [App::DocumentObjectGroupPython] G4_DNA_U  # scripted group (container) (typed FeaturePython)
  Dunit = g/cm3
  Dvalue = 1
  Group = -> [H_element137,C_element147,N_element067,O_element129,P_element018]
  conduct = 2
  density = 1
  expand = 3
  formula = G4_DNA_U
  name = G4_DNA_U
  specific = 4
FEATURE [App::DocumentObjectGroupPython] H_element138  label="H_element : 085"  # scripted group (container) (typed FeaturePython)
  n = 11
  ref = H_element
FEATURE [App::DocumentObjectGroupPython] C_element148  label="C_element : 093"  # scripted group (container) (typed FeaturePython)
  n = 10
  ref = C_element
FEATURE [App::DocumentObjectGroupPython] N_element068  label="N_element : 040"  # scripted group (container) (typed FeaturePython)
  n = 2
  ref = N_element
FEATURE [App::DocumentObjectGroupPython] O_element130  label="O_element : 081"  # scripted group (container) (typed FeaturePython)
  n = 9
  ref = O_element
FEATURE [App::DocumentObjectGroupPython] P_element019  label="P_element : 008"  # scripted group (container) (typed FeaturePython)
  n = 1
  ref = P_element
FEATURE [App::DocumentObjectGroupPython] G4_DNA_MU  # scripted group (container) (typed FeaturePython)
  Dunit = g/cm3
  Dvalue = 1
  Group = -> [H_element138,C_element148,N_element068,O_element130,P_element019]
  conduct = 2
  density = 1
  expand = 3
  formula = G4_DNA_MU
  name = G4_DNA_MU
  specific = 4
FEATURE [App::DocumentObjectGroupPython] BioChemical  # scripted group (container) (typed FeaturePython)
  Group = -> [G4_CYTOSINE,G4_THYMINE,G4_URACIL,G4_DNA_ADENINE,G4_DNA_GUANINE,G4_DNA_CYTOSINE,G4_DNA_THYMINE,G4_DNA_URACIL,G4_DNA_ADENOSINE,G4_DNA_GUANOSINE,G4_DNA_CYTIDINE,G4_DNA_URIDINE,G4_DNA_METHYLURIDINE,G4_DNA_MONOPHOSPHATE,G4_DNA_A,G4_DNA_G,G4_DNA_C,G4_DNA_U,G4_DNA_MU]
FEATURE [App::DocumentObjectGroupPython] G4Materials  # scripted group (container) (typed FeaturePython)
  Group = -> [NIST,Element,HEP,Space,BioChemical]
  version = 1
FEATURE [App::DocumentObjectGroupPython] Geant4  # scripted group (container) (typed FeaturePython)
  Group = -> [G4Isotopes,G4Elements,G4Materials]
FEATURE [App::DocumentObjectGroupPython] Materials  # scripted group (container) (typed FeaturePython)
  Group = -> [Geant4]
FEATURE [Part::FeaturePython] GDMLBox_WorldBox  # WARN: FeaturePython — macro-defined, semantics opaque (R4)
  lunit = 3
  material = 288
  x = 500
  y = 500
  z = 1200
FEATURE [Sketcher::SketchObject] Sketch001
  ArcFitTolerance = 0
  AttachmentSupport = -> [YZ_Plane001]
  FullyConstrained = false
  MakeInternals = false
  MapMode = 5
  Placement = pos=(0,0,0) rot=(0.57735,0.57735,0.57735;2.0944rad)
  sketch-geometry (36):
    g0: LineSegment StartX=345.196 StartY=1207.39 StartZ=0 EndX=345.196 EndY=4779.1 EndZ=0
    g1: LineSegment StartX=910.487 StartY=4896.42 StartZ=0 EndX=910.487 EndY=5006.42 EndZ=0
    g2: LineSegment StartX=435.196 StartY=4869.1 StartZ=0 EndX=445.196 EndY=4869.1 EndZ=0
    g3: LineSegment StartX=445.196 StartY=4869.1 StartZ=0 EndX=445.196 EndY=4896.42 EndZ=0
    g4: LineSegment StartX=445.196 StartY=4896.42 StartZ=0 EndX=910.487 EndY=4896.42 EndZ=0
    g5: LineSegment StartX=318.538 StartY=5006.42 StartZ=0 EndX=910.487 EndY=5006.42 EndZ=0
    g6: LineSegment StartX=175.531 StartY=1234.96 StartZ=0 EndX=318.538 EndY=1234.96 EndZ=0
    g7: LineSegment StartX=318.538 StartY=5006.42 StartZ=0 EndX=318.538 EndY=1234.96 EndZ=0
    g8: LineSegment StartX=0 StartY=39.215 StartZ=0 EndX=0 EndY=0 EndZ=0
    g9-g16: Circle [constr] x8 (B-spline internal-alignment scaffolding for g17; pole/knot coordinates omitted)
    g17: BSplineCurve PolesCount=8 KnotsCount=6 Degree=3 IsPeriodic=0
    g18-g23: GeomPoint [constr] x6 (B-spline internal-alignment scaffolding for g17; pole/knot coordinates omitted)
    g24: LineSegment StartX=175.531 StartY=1234.96 StartZ=0 EndX=175.531 EndY=838.896 EndZ=0
    g25-g29: Circle [constr] x5 (B-spline internal-alignment scaffolding for g30; pole/knot coordinates omitted)
    g30: BSplineCurve PolesCount=5 KnotsCount=3 Degree=3 IsPeriodic=0
    g31: GeomPoint [constr] X=175.531 Y=838.896 Z=0
    g32: GeomPoint [constr] X=165.058 Y=242.363 Z=0
    g33: GeomPoint [constr] X=0 Y=39.215 Z=0
    g34: ArcOfCircle CenterX=435.196 CenterY=4779.1 CenterZ=0 NormalX=0 NormalY=0 NormalZ=1 AngleXU=0 Radius=90 StartAngle=1.5708 EndAngle=3.14159
    g35: GeomPoint [constr] X=345.196 Y=4869.1 Z=0
  constraints (38):
    c: Vertical(g1)
    c: Horizontal(g2)
    c: Coincident(g2,g3)
    c: Vertical(g3)
    c: Coincident(g3,g4)
    c: Coincident(g4,g1)
    c: Horizontal(g4)
    c: Coincident(g5,g1)
    c: Horizontal(g5)
    c: Horizontal(g6)
    c: Coincident(g7,g5)
    c: Coincident(g7,g6)
    c: Vertical(g7)
    c: DistanceX(g35,g2) = 100
    c: Vertical(g8)
    c: Vertical(g0)
    c: Coincident(g17,g0)
    c: Weight(g9) = 1
    c: Equal(g9, g10-g16) x7
    c: Coincident(g17,g8)
    c: InternalAlignment(g9-g16 -> g17) x8
    c: InternalAlignment(g18-g23 -> g17) x6
    c: Coincident(g24,g6)
    c: Vertical(g24)
    c: Coincident(g30,g24)
    c: Weight(g25) = 1
    c: Equal(g25, g26-g29) x4
    c: Coincident(g30,g8)
    c: InternalAlignment(g25-g29 -> g30) x5
    c: InternalAlignment(g31,g30)
    c: InternalAlignment(g32,g30)
    c: InternalAlignment(g33,g30)
    c: Coincident(g8,g-1)
    c: PointOnObject(g35,g2)
    c: PointOnObject(g35,g0)
    c: Tangent(g2,g34) = 1.5708
    c: Tangent(g0,g34) = 1.5708
    c: Radius(g34) = 90
FEATURE [Part::Revolution] Revolve
  Angle = 360
  Axis = (0,0,1)
  Base = (0,0,0)
  FaceMakerClass = Part::FaceMakerBullseye
  Solid = true
  Source = -> Sketch001
  Symmetric = false
  material = 176
FEATURE [Part::Cylinder] Cylinder
  Angle = 360
  AttacherType = Attacher::AttachEngine3D
  FirstAngle = 0
  Height = 200
  Placement = pos=(474,0,4850) rot=(0,0,1;0rad)
  Radius = 60
  SecondAngle = 0
FEATURE [Part::Cut] Cut
  Base = -> Revolve
  Tool = -> Cylinder
FEATURE [App::Part] Bool_Cut
  Group = -> [Sketch001,Revolve,Cylinder,Cut]
  Origin = -> Origin004
FEATURE [App::Part] worldVOL
  Group = -> [GDMLBox_WorldBox,Bool_Cut]
  Origin = -> Origin
